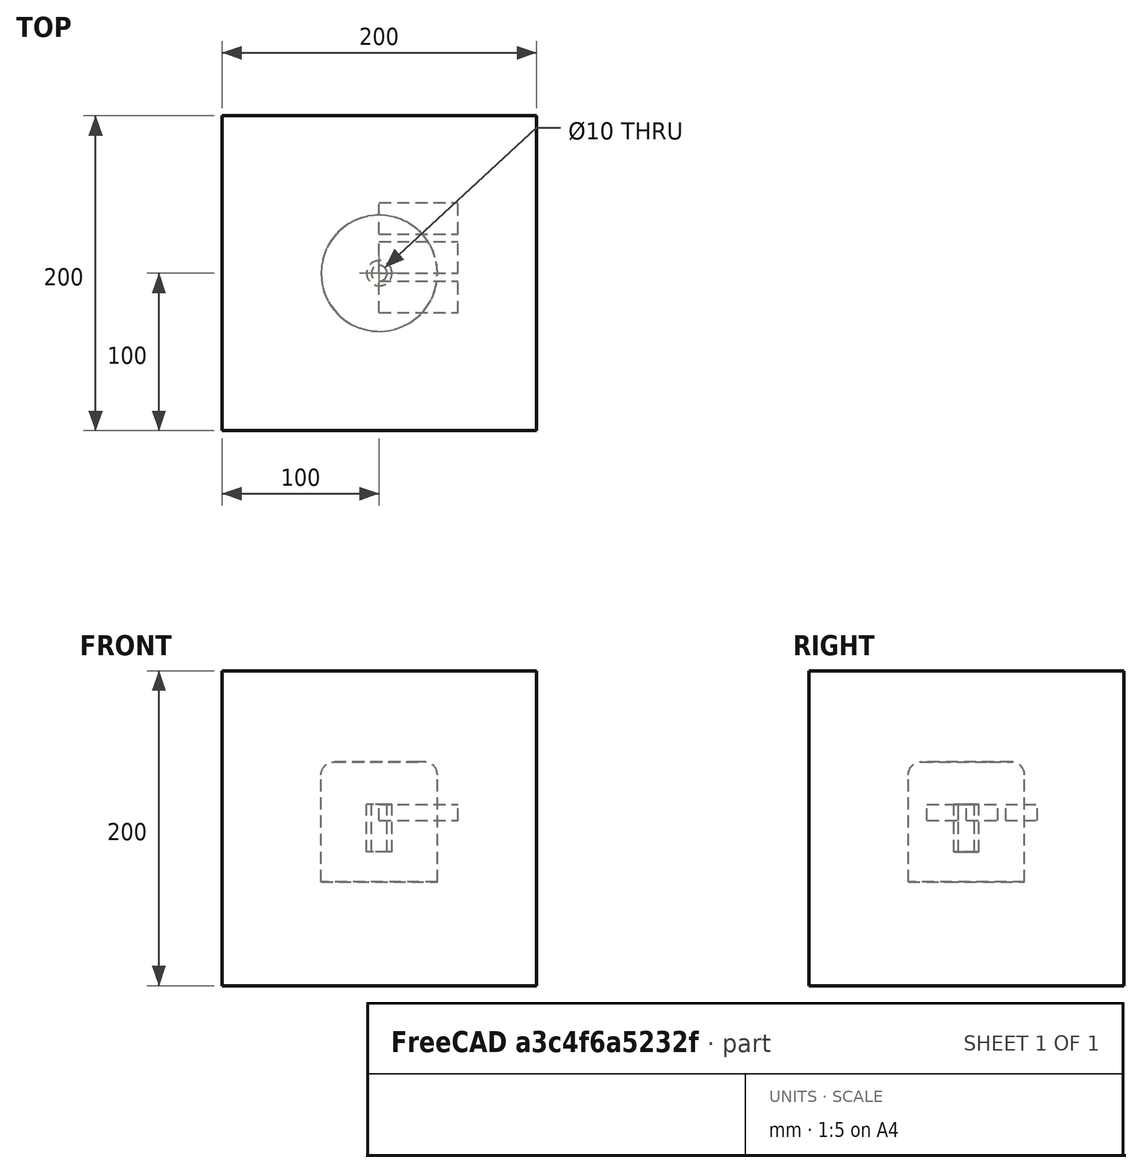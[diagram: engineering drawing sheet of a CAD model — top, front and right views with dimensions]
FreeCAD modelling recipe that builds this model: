
FCSTD DOCUMENT  (FreeCAD 0.21R33694 (Git))
Label: assemblyTest-A
License: All rights reserved
LicenseURL: http://en.wikipedia.org/wiki/All_rights_reserved
objects: App::DocumentObjectGroupPython×1254, Part::FeaturePython×5, App::Part×5, Part::Box×3, Part::Fuse×2
note: 10 computed .brp shape members not serialized (recipe doc carries the construction recipe); baked Part::Feature solids carry a one-line shape summary decoded from their .brp

FEATURE [App::DocumentObjectGroupPython] HALFPI  # scripted group (container) (typed FeaturePython)
  name = HALFPI
  value = pi/2.
FEATURE [App::DocumentObjectGroupPython] PI  # scripted group (container) (typed FeaturePython)
  name = PI
  value = 1.*pi
FEATURE [App::DocumentObjectGroupPython] TWOPI  # scripted group (container) (typed FeaturePython)
  name = TWOPI
  value = 2.*pi
FEATURE [App::DocumentObjectGroupPython] Variables  # scripted group (container) (typed FeaturePython)
FEATURE [App::DocumentObjectGroupPython] Quantities  # scripted group (container) (typed FeaturePython)
FEATURE [App::DocumentObjectGroupPython] Isotopes  # scripted group (container) (typed FeaturePython)
FEATURE [App::DocumentObjectGroupPython] Elements  # scripted group (container) (typed FeaturePython)
FEATURE [App::DocumentObjectGroupPython] G4Isotopes  # scripted group (container) (typed FeaturePython)
FEATURE [App::DocumentObjectGroupPython] H_element  # scripted group (container) (typed FeaturePython)
  Z = 1
  atom_value = 1.008
  formula = H
  name = H_element
FEATURE [App::DocumentObjectGroupPython] He_element  # scripted group (container) (typed FeaturePython)
  Z = 2
  atom_value = 4.0026
  formula = He
  name = He_element
FEATURE [App::DocumentObjectGroupPython] Li_element  # scripted group (container) (typed FeaturePython)
  Z = 3
  atom_value = 6.94
  formula = Li
  name = Li_element
FEATURE [App::DocumentObjectGroupPython] Be_element  # scripted group (container) (typed FeaturePython)
  Z = 4
  atom_value = 9.01218
  formula = Be
  name = Be_element
FEATURE [App::DocumentObjectGroupPython] B_element  # scripted group (container) (typed FeaturePython)
  Z = 5
  atom_value = 10.81
  formula = B
  name = B_element
FEATURE [App::DocumentObjectGroupPython] C_element  # scripted group (container) (typed FeaturePython)
  Z = 6
  atom_value = 12.011
  formula = C
  name = C_element
FEATURE [App::DocumentObjectGroupPython] N_element  # scripted group (container) (typed FeaturePython)
  Z = 7
  atom_value = 14.007
  formula = N
  name = N_element
FEATURE [App::DocumentObjectGroupPython] O_element  # scripted group (container) (typed FeaturePython)
  Z = 8
  atom_value = 15.999
  formula = O
  name = O_element
FEATURE [App::DocumentObjectGroupPython] F_element  # scripted group (container) (typed FeaturePython)
  Z = 9
  atom_value = 18.9984
  formula = F
  name = F_element
FEATURE [App::DocumentObjectGroupPython] Ne_element  # scripted group (container) (typed FeaturePython)
  Z = 10
  atom_value = 20.1797
  formula = Ne
  name = Ne_element
FEATURE [App::DocumentObjectGroupPython] Na_element  # scripted group (container) (typed FeaturePython)
  Z = 11
  atom_value = 22.9898
  formula = Na
  name = Na_element
FEATURE [App::DocumentObjectGroupPython] Mg_element  # scripted group (container) (typed FeaturePython)
  Z = 12
  atom_value = 24.305
  formula = Mg
  name = Mg_element
FEATURE [App::DocumentObjectGroupPython] Al_element  # scripted group (container) (typed FeaturePython)
  Z = 13
  atom_value = 26.9815
  formula = Al
  name = Al_element
FEATURE [App::DocumentObjectGroupPython] Si_element  # scripted group (container) (typed FeaturePython)
  Z = 14
  atom_value = 28.085
  formula = Si
  name = Si_element
FEATURE [App::DocumentObjectGroupPython] P_element  # scripted group (container) (typed FeaturePython)
  Z = 15
  atom_value = 30.9738
  formula = P
  name = P_element
FEATURE [App::DocumentObjectGroupPython] S_element  # scripted group (container) (typed FeaturePython)
  Z = 16
  atom_value = 32.06
  formula = S
  name = S_element
FEATURE [App::DocumentObjectGroupPython] Cl_element  # scripted group (container) (typed FeaturePython)
  Z = 17
  atom_value = 35.45
  formula = Cl
  name = Cl_element
FEATURE [App::DocumentObjectGroupPython] Ar_element  # scripted group (container) (typed FeaturePython)
  Z = 18
  atom_value = 39.95
  formula = Ar
  name = Ar_element
FEATURE [App::DocumentObjectGroupPython] K_element  # scripted group (container) (typed FeaturePython)
  Z = 19
  atom_value = 39.0983
  formula = K
  name = K_element
FEATURE [App::DocumentObjectGroupPython] Ca_element  # scripted group (container) (typed FeaturePython)
  Z = 20
  atom_value = 40.078
  formula = Ca
  name = Ca_element
FEATURE [App::DocumentObjectGroupPython] Sc_element  # scripted group (container) (typed FeaturePython)
  Z = 21
  atom_value = 44.9559
  formula = Sc
  name = Sc_element
FEATURE [App::DocumentObjectGroupPython] Ti_element  # scripted group (container) (typed FeaturePython)
  Z = 22
  atom_value = 47.867
  formula = Ti
  name = Ti_element
FEATURE [App::DocumentObjectGroupPython] V_element  # scripted group (container) (typed FeaturePython)
  Z = 23
  atom_value = 50.9415
  formula = V
  name = V_element
FEATURE [App::DocumentObjectGroupPython] Cr_element  # scripted group (container) (typed FeaturePython)
  Z = 24
  atom_value = 51.9961
  formula = Cr
  name = Cr_element
FEATURE [App::DocumentObjectGroupPython] Mn_element  # scripted group (container) (typed FeaturePython)
  Z = 25
  atom_value = 54.938
  formula = Mn
  name = Mn_element
FEATURE [App::DocumentObjectGroupPython] Fe_element  # scripted group (container) (typed FeaturePython)
  Z = 26
  atom_value = 55.845
  formula = Fe
  name = Fe_element
FEATURE [App::DocumentObjectGroupPython] Co_element  # scripted group (container) (typed FeaturePython)
  Z = 27
  atom_value = 58.9332
  formula = Co
  name = Co_element
FEATURE [App::DocumentObjectGroupPython] Ni_element  # scripted group (container) (typed FeaturePython)
  Z = 28
  atom_value = 58.6934
  formula = Ni
  name = Ni_element
FEATURE [App::DocumentObjectGroupPython] Cu_element  # scripted group (container) (typed FeaturePython)
  Z = 29
  atom_value = 63.546
  formula = Cu
  name = Cu_element
FEATURE [App::DocumentObjectGroupPython] Zn_element  # scripted group (container) (typed FeaturePython)
  Z = 30
  atom_value = 65.38
  formula = Zn
  name = Zn_element
FEATURE [App::DocumentObjectGroupPython] Ga_element  # scripted group (container) (typed FeaturePython)
  Z = 31
  atom_value = 69.723
  formula = Ga
  name = Ga_element
FEATURE [App::DocumentObjectGroupPython] Ge_element  # scripted group (container) (typed FeaturePython)
  Z = 32
  atom_value = 72.63
  formula = Ge
  name = Ge_element
FEATURE [App::DocumentObjectGroupPython] As_element  # scripted group (container) (typed FeaturePython)
  Z = 33
  atom_value = 74.9216
  formula = As
  name = As_element
FEATURE [App::DocumentObjectGroupPython] Se_element  # scripted group (container) (typed FeaturePython)
  Z = 34
  atom_value = 78.971
  formula = Se
  name = Se_element
FEATURE [App::DocumentObjectGroupPython] Br_element  # scripted group (container) (typed FeaturePython)
  Z = 35
  atom_value = 79.904
  formula = Br
  name = Br_element
FEATURE [App::DocumentObjectGroupPython] Kr_element  # scripted group (container) (typed FeaturePython)
  Z = 36
  atom_value = 83.798
  formula = Kr
  name = Kr_element
FEATURE [App::DocumentObjectGroupPython] Rb_element  # scripted group (container) (typed FeaturePython)
  Z = 37
  atom_value = 85.4678
  formula = Rb
  name = Rb_element
FEATURE [App::DocumentObjectGroupPython] Sr_element  # scripted group (container) (typed FeaturePython)
  Z = 38
  atom_value = 87.62
  formula = Sr
  name = Sr_element
FEATURE [App::DocumentObjectGroupPython] Y_element  # scripted group (container) (typed FeaturePython)
  Z = 39
  atom_value = 88.9058
  formula = Y
  name = Y_element
FEATURE [App::DocumentObjectGroupPython] Zr_element  # scripted group (container) (typed FeaturePython)
  Z = 40
  atom_value = 91.224
  formula = Zr
  name = Zr_element
FEATURE [App::DocumentObjectGroupPython] Nb_element  # scripted group (container) (typed FeaturePython)
  Z = 41
  atom_value = 92.9064
  formula = Nb
  name = Nb_element
FEATURE [App::DocumentObjectGroupPython] Mo_element  # scripted group (container) (typed FeaturePython)
  Z = 42
  atom_value = 95.95
  formula = Mo
  name = Mo_element
FEATURE [App::DocumentObjectGroupPython] Tc_element  # scripted group (container) (typed FeaturePython)
  Z = 43
  atom_value = 97
  formula = Tc
  name = Tc_element
FEATURE [App::DocumentObjectGroupPython] Ru_element  # scripted group (container) (typed FeaturePython)
  Z = 44
  atom_value = 101.07
  formula = Ru
  name = Ru_element
FEATURE [App::DocumentObjectGroupPython] Rh_element  # scripted group (container) (typed FeaturePython)
  Z = 45
  atom_value = 102.905
  formula = Rh
  name = Rh_element
FEATURE [App::DocumentObjectGroupPython] Pd_element  # scripted group (container) (typed FeaturePython)
  Z = 46
  atom_value = 106.42
  formula = Pd
  name = Pd_element
FEATURE [App::DocumentObjectGroupPython] Ag_element  # scripted group (container) (typed FeaturePython)
  Z = 47
  atom_value = 107.868
  formula = Ag
  name = Ag_element
FEATURE [App::DocumentObjectGroupPython] Cd_element  # scripted group (container) (typed FeaturePython)
  Z = 48
  atom_value = 112.414
  formula = Cd
  name = Cd_element
FEATURE [App::DocumentObjectGroupPython] In_element  # scripted group (container) (typed FeaturePython)
  Z = 49
  atom_value = 114.818
  formula = In
  name = In_element
FEATURE [App::DocumentObjectGroupPython] Sn_element  # scripted group (container) (typed FeaturePython)
  Z = 50
  atom_value = 118.71
  formula = Sn
  name = Sn_element
FEATURE [App::DocumentObjectGroupPython] Sb_element  # scripted group (container) (typed FeaturePython)
  Z = 51
  atom_value = 121.76
  formula = Sb
  name = Sb_element
FEATURE [App::DocumentObjectGroupPython] Te_element  # scripted group (container) (typed FeaturePython)
  Z = 52
  atom_value = 127.6
  formula = Te
  name = Te_element
FEATURE [App::DocumentObjectGroupPython] I_element  # scripted group (container) (typed FeaturePython)
  Z = 53
  atom_value = 126.904
  formula = I
  name = I_element
FEATURE [App::DocumentObjectGroupPython] Xe_element  # scripted group (container) (typed FeaturePython)
  Z = 54
  atom_value = 131.293
  formula = Xe
  name = Xe_element
FEATURE [App::DocumentObjectGroupPython] Cs_element  # scripted group (container) (typed FeaturePython)
  Z = 55
  atom_value = 132.905
  formula = Cs
  name = Cs_element
FEATURE [App::DocumentObjectGroupPython] Ba_element  # scripted group (container) (typed FeaturePython)
  Z = 56
  atom_value = 137.327
  formula = Ba
  name = Ba_element
FEATURE [App::DocumentObjectGroupPython] La_element  # scripted group (container) (typed FeaturePython)
  Z = 57
  atom_value = 138.905
  formula = La
  name = La_element
FEATURE [App::DocumentObjectGroupPython] Ce_element  # scripted group (container) (typed FeaturePython)
  Z = 58
  atom_value = 140.116
  formula = Ce
  name = Ce_element
FEATURE [App::DocumentObjectGroupPython] Pr_element  # scripted group (container) (typed FeaturePython)
  Z = 59
  atom_value = 140.908
  formula = Pr
  name = Pr_element
FEATURE [App::DocumentObjectGroupPython] Nd_element  # scripted group (container) (typed FeaturePython)
  Z = 60
  atom_value = 144.242
  formula = Nd
  name = Nd_element
FEATURE [App::DocumentObjectGroupPython] Pm_element  # scripted group (container) (typed FeaturePython)
  Z = 61
  atom_value = 145
  formula = Pm
  name = Pm_element
FEATURE [App::DocumentObjectGroupPython] Sm_element  # scripted group (container) (typed FeaturePython)
  Z = 62
  atom_value = 150.36
  formula = Sm
  name = Sm_element
FEATURE [App::DocumentObjectGroupPython] Eu_element  # scripted group (container) (typed FeaturePython)
  Z = 63
  atom_value = 151.964
  formula = Eu
  name = Eu_element
FEATURE [App::DocumentObjectGroupPython] Gd_element  # scripted group (container) (typed FeaturePython)
  Z = 64
  atom_value = 157.25
  formula = Gd
  name = Gd_element
FEATURE [App::DocumentObjectGroupPython] Tb_element  # scripted group (container) (typed FeaturePython)
  Z = 65
  atom_value = 158.925
  formula = Tb
  name = Tb_element
FEATURE [App::DocumentObjectGroupPython] Dy_element  # scripted group (container) (typed FeaturePython)
  Z = 66
  atom_value = 162.5
  formula = Dy
  name = Dy_element
FEATURE [App::DocumentObjectGroupPython] Ho_element  # scripted group (container) (typed FeaturePython)
  Z = 67
  atom_value = 164.93
  formula = Ho
  name = Ho_element
FEATURE [App::DocumentObjectGroupPython] Er_element  # scripted group (container) (typed FeaturePython)
  Z = 68
  atom_value = 167.259
  formula = Er
  name = Er_element
FEATURE [App::DocumentObjectGroupPython] Tm_element  # scripted group (container) (typed FeaturePython)
  Z = 69
  atom_value = 168.934
  formula = Tm
  name = Tm_element
FEATURE [App::DocumentObjectGroupPython] Yb_element  # scripted group (container) (typed FeaturePython)
  Z = 70
  atom_value = 173.045
  formula = Yb
  name = Yb_element
FEATURE [App::DocumentObjectGroupPython] Lu_element  # scripted group (container) (typed FeaturePython)
  Z = 71
  atom_value = 174.967
  formula = Lu
  name = Lu_element
FEATURE [App::DocumentObjectGroupPython] Hf_element  # scripted group (container) (typed FeaturePython)
  Z = 72
  atom_value = 178.49
  formula = Hf
  name = Hf_element
FEATURE [App::DocumentObjectGroupPython] Ta_element  # scripted group (container) (typed FeaturePython)
  Z = 73
  atom_value = 180.948
  formula = Ta
  name = Ta_element
FEATURE [App::DocumentObjectGroupPython] W_element  # scripted group (container) (typed FeaturePython)
  Z = 74
  atom_value = 183.84
  formula = W
  name = W_element
FEATURE [App::DocumentObjectGroupPython] Re_element  # scripted group (container) (typed FeaturePython)
  Z = 75
  atom_value = 186.207
  formula = Re
  name = Re_element
FEATURE [App::DocumentObjectGroupPython] Os_element  # scripted group (container) (typed FeaturePython)
  Z = 76
  atom_value = 190.23
  formula = Os
  name = Os_element
FEATURE [App::DocumentObjectGroupPython] Ir_element  # scripted group (container) (typed FeaturePython)
  Z = 77
  atom_value = 192.217
  formula = Ir
  name = Ir_element
FEATURE [App::DocumentObjectGroupPython] Pt_element  # scripted group (container) (typed FeaturePython)
  Z = 78
  atom_value = 195.084
  formula = Pt
  name = Pt_element
FEATURE [App::DocumentObjectGroupPython] Au_element  # scripted group (container) (typed FeaturePython)
  Z = 79
  atom_value = 196.967
  formula = Au
  name = Au_element
FEATURE [App::DocumentObjectGroupPython] Hg_element  # scripted group (container) (typed FeaturePython)
  Z = 80
  atom_value = 200.592
  formula = Hg
  name = Hg_element
FEATURE [App::DocumentObjectGroupPython] Tl_element  # scripted group (container) (typed FeaturePython)
  Z = 81
  atom_value = 204.38
  formula = Tl
  name = Tl_element
FEATURE [App::DocumentObjectGroupPython] Pb_element  # scripted group (container) (typed FeaturePython)
  Z = 82
  atom_value = 207.2
  formula = Pb
  name = Pb_element
FEATURE [App::DocumentObjectGroupPython] Bi_element  # scripted group (container) (typed FeaturePython)
  Z = 83
  atom_value = 208.98
  formula = Bi
  name = Bi_element
FEATURE [App::DocumentObjectGroupPython] Po_element  # scripted group (container) (typed FeaturePython)
  Z = 84
  atom_value = 209
  formula = Po
  name = Po_element
FEATURE [App::DocumentObjectGroupPython] At_element  # scripted group (container) (typed FeaturePython)
  Z = 85
  atom_value = 210
  formula = At
  name = At_element
FEATURE [App::DocumentObjectGroupPython] Rn_element  # scripted group (container) (typed FeaturePython)
  Z = 86
  atom_value = 222
  formula = Rn
  name = Rn_element
FEATURE [App::DocumentObjectGroupPython] Fr_element  # scripted group (container) (typed FeaturePython)
  Z = 87
  atom_value = 223
  formula = Fr
  name = Fr_element
FEATURE [App::DocumentObjectGroupPython] Ra_element  # scripted group (container) (typed FeaturePython)
  Z = 88
  atom_value = 226
  formula = Ra
  name = Ra_element
FEATURE [App::DocumentObjectGroupPython] Ac_element  # scripted group (container) (typed FeaturePython)
  Z = 89
  atom_value = 227
  formula = Ac
  name = Ac_element
FEATURE [App::DocumentObjectGroupPython] Th_element  # scripted group (container) (typed FeaturePython)
  Z = 90
  atom_value = 232.038
  formula = Th
  name = Th_element
FEATURE [App::DocumentObjectGroupPython] Pa_element  # scripted group (container) (typed FeaturePython)
  Z = 91
  atom_value = 231.036
  formula = Pa
  name = Pa_element
FEATURE [App::DocumentObjectGroupPython] U_element  # scripted group (container) (typed FeaturePython)
  Z = 92
  atom_value = 238.029
  formula = U
  name = U_element
FEATURE [App::DocumentObjectGroupPython] Np_element  # scripted group (container) (typed FeaturePython)
  Z = 93
  atom_value = 237
  formula = Np
  name = Np_element
FEATURE [App::DocumentObjectGroupPython] Pu_element  # scripted group (container) (typed FeaturePython)
  Z = 94
  atom_value = 244
  formula = Pu
  name = Pu_element
FEATURE [App::DocumentObjectGroupPython] Am_element  # scripted group (container) (typed FeaturePython)
  Z = 95
  atom_value = 243
  formula = Am
  name = Am_element
FEATURE [App::DocumentObjectGroupPython] Cm_element  # scripted group (container) (typed FeaturePython)
  Z = 96
  atom_value = 247
  formula = Cm
  name = Cm_element
FEATURE [App::DocumentObjectGroupPython] Bk_element  # scripted group (container) (typed FeaturePython)
  Z = 97
  atom_value = 247
  formula = Bk
  name = Bk_element
FEATURE [App::DocumentObjectGroupPython] Cf_element  # scripted group (container) (typed FeaturePython)
  Z = 98
  atom_value = 251
  formula = Cf
  name = Cf_element
FEATURE [App::DocumentObjectGroupPython] G4Elements  # scripted group (container) (typed FeaturePython)
  Group = -> [H_element,He_element,Li_element,Be_element,B_element,C_element,N_element,O_element,F_element,Ne_element,Na_element,Mg_element,Al_element,Si_element,P_element,S_element,Cl_element,Ar_element,K_element,Ca_element,Sc_element,Ti_element,V_element,Cr_element,Mn_element,Fe_element,Co_element,Ni_element,Cu_element,Zn_element,Ga_element,Ge_element,As_element,Se_element,Br_element,Kr_element,Rb_element,+61 more]
FEATURE [Part::FeaturePython] GDMLBox_WorldBox  # WARN: FeaturePython — macro-defined, semantics opaque (R4)
  lunit = 2
  material = 5
  x = 200
  y = 200
  z = 200
FEATURE [App::DocumentObjectGroupPython] HALFPI001  # scripted group (container) (typed FeaturePython)
  name = HALFPI
  value = pi/2.
FEATURE [App::DocumentObjectGroupPython] PI001  # scripted group (container) (typed FeaturePython)
  name = PI
  value = 1.*pi
FEATURE [App::DocumentObjectGroupPython] TWOPI001  # scripted group (container) (typed FeaturePython)
  name = TWOPI
  value = 2.*pi
FEATURE [App::DocumentObjectGroupPython] HALFPI001001  # scripted group (container) (typed FeaturePython)
  name = HALFPI001
  value = pi/2.
FEATURE [App::DocumentObjectGroupPython] PI001001  # scripted group (container) (typed FeaturePython)
  name = PI001
  value = 1.*pi
FEATURE [App::DocumentObjectGroupPython] TWOPI001001  # scripted group (container) (typed FeaturePython)
  name = TWOPI001
  value = 2.*pi
FEATURE [App::DocumentObjectGroupPython] Constants  # scripted group (container) (typed FeaturePython)
  Group = -> [HALFPI,PI,TWOPI,HALFPI001,PI001,TWOPI001,HALFPI001001,PI001001,TWOPI001001]
FEATURE [Part::FeaturePython] GDMLTorus_Torus  # WARN: FeaturePython — macro-defined, semantics opaque (R4)
  aunit = deg
  deltaphi = 360
  lunit = 2
  material = 0
  rmax = 8
  rmin = 0
  rtor = 28.9
  startphi = 0
FEATURE [Part::FeaturePython] GDMLTube_Tube  # WARN: FeaturePython — macro-defined, semantics opaque (R4)
  aunit = 1
  deltaphi = 360
  lunit = 2
  material = 0
  rmax = 28.9
  rmin = 0
  startphi = 0
  z = 16
FEATURE [Part::FeaturePython] GDMLTube_Tube001  label="GDMLTube_T_1"  # WARN: FeaturePython — macro-defined, semantics opaque (R4)
  Placement = pos=(0,0,-34) rot=(0,0,-1;0.349066rad)
  aunit = 1
  deltaphi = 360
  lunit = 2
  material = 0
  rmax = 36.9
  rmin = 0
  startphi = 0
  z = 68
FEATURE [Part::Fuse] Union
  Base = -> GDMLTorus_Torus
  Placement = pos=(0,0,0) rot=(0,0,1;0.523599rad)
  Tool = -> GDMLTube_Tube
FEATURE [Part::Fuse] Union001  label="U1"
  Base = -> Union
  Placement = pos=(0,0,34) rot=(0,0,1;0rad)
  Tool = -> GDMLTube_Tube001
  material = 211
FEATURE [App::Part] Bool_Union001  label="Detector"
  Group = -> [GDMLTorus_Torus,GDMLTube_Tube,Union,GDMLTube_Tube001,Union001]
  Origin = -> Origin005
FEATURE [Part::FeaturePython] GDMLTube_Tube002  # WARN: FeaturePython — macro-defined, semantics opaque (R4)
  aunit = 1
  deltaphi = 360
  lunit = 2
  material = 109
  rmax = 8
  rmin = 5
  startphi = 0
  z = 30
FEATURE [App::Part] LV_Tube  label="Tube"
  Group = -> [GDMLTube_Tube002]
  Origin = -> Origin006
  Placement = pos=(57,0,0) rot=(0,1,0;1.5708rad)
FEATURE [App::Part] Part  label="DetectorAssembly"
  Group = -> [Bool_Union001,LV_Tube]
  Origin = -> Origin007
FEATURE [Part::Box] Box  label="Cube"
  AttacherType = Attacher::AttachEngine3D
  Height = 10
  Length = 50
  Placement = pos=(0,0,5) rot=(0,0,1;0rad)
  Width = 20
  material = 441
FEATURE [Part::Box] Box001  label="Cube001"
  AttacherType = Attacher::AttachEngine3D
  Height = 10
  Length = 50
  Placement = pos=(0,25,5) rot=(0,0,1;0rad)
  Width = 20
  material = 441
FEATURE [Part::Box] Box002  label="Cube002"
  AttacherType = Attacher::AttachEngine3D
  Height = 10
  Length = 50
  Placement = pos=(0,-25,5) rot=(0,0,1;0rad)
  Width = 20
  material = 261
FEATURE [App::Part] Part001  label="shieldAssembly"
  Group = -> [Box,Box001,Box002]
  Origin = -> Origin008
  Placement = pos=(0,0,58) rot=(0,0,1;0rad)
FEATURE [App::Part] worldVOL
  Group = -> [GDMLBox_WorldBox,Part,Part001]
  Origin = -> Origin
FEATURE [App::DocumentObjectGroupPython] H_element553  label="H_element : 0.246"  # scripted group (container) (typed FeaturePython)
  n = 0.101327
FEATURE [App::DocumentObjectGroupPython] C_element593  label="C_element : 0.974"  # scripted group (container) (typed FeaturePython)
  n = 0.7755
FEATURE [App::DocumentObjectGroupPython] N_element273  label="N_element : 0.828"  # scripted group (container) (typed FeaturePython)
  n = 0.035057
FEATURE [App::DocumentObjectGroupPython] O_element521  label="O_element : 0.966"  # scripted group (container) (typed FeaturePython)
  n = 0.0523159
FEATURE [App::DocumentObjectGroupPython] F_element077  label="F_element : 0.727"  # scripted group (container) (typed FeaturePython)
  n = 0.017422
FEATURE [App::DocumentObjectGroupPython] Ca_element057  label="Ca_element : 0.240"  # scripted group (container) (typed FeaturePython)
  n = 0.018378
FEATURE [App::DocumentObjectGroupPython] G4_A_150_TISSUE  label="G4_A-150_TISSUE"  # scripted group (container) (typed FeaturePython)
  Dunit = g/cm3
  Dvalue = 1.127
  Group = -> [H_element553,C_element593,N_element273,O_element521,F_element077,Ca_element057]
  conduct = 2
  density = 1
  expand = 3
  formula = G4_A-150_TISSUE
  name = G4_A-150_TISSUE
  specific = 4
FEATURE [App::DocumentObjectGroupPython] C_element594  label="C_element : 390"  # scripted group (container) (typed FeaturePython)
  n = 3
  ref = C_element
FEATURE [App::DocumentObjectGroupPython] H_element554  label="H_element : 358"  # scripted group (container) (typed FeaturePython)
  n = 6
  ref = H_element
FEATURE [App::DocumentObjectGroupPython] O_element522  label="O_element : 335"  # scripted group (container) (typed FeaturePython)
  n = 1
  ref = O_element
FEATURE [App::DocumentObjectGroupPython] G4_ACETONE  # scripted group (container) (typed FeaturePython)
  Dunit = g/cm3
  Dvalue = 0.7899
  Group = -> [C_element594,H_element554,O_element522]
  conduct = 2
  density = 1
  expand = 3
  formula = G4_ACETONE
  name = G4_ACETONE
  specific = 4
FEATURE [App::DocumentObjectGroupPython] C_element595  label="C_element : 391"  # scripted group (container) (typed FeaturePython)
  n = 2
  ref = C_element
FEATURE [App::DocumentObjectGroupPython] H_element555  label="H_element : 359"  # scripted group (container) (typed FeaturePython)
  n = 2
  ref = H_element
FEATURE [App::DocumentObjectGroupPython] G4_ACETYLENE  # scripted group (container) (typed FeaturePython)
  Dunit = g/cm3
  Dvalue = 0.0010967
  Group = -> [C_element595,H_element555]
  conduct = 2
  density = 1
  expand = 3
  formula = G4_ACETYLENE
  name = G4_ACETYLENE
  specific = 4
FEATURE [App::DocumentObjectGroupPython] C_element596  label="C_element : 392"  # scripted group (container) (typed FeaturePython)
  n = 5
  ref = C_element
FEATURE [App::DocumentObjectGroupPython] H_element556  label="H_element : 360"  # scripted group (container) (typed FeaturePython)
  n = 5
  ref = H_element
FEATURE [App::DocumentObjectGroupPython] N_element274  label="N_element : 154"  # scripted group (container) (typed FeaturePython)
  n = 5
  ref = N_element
FEATURE [App::DocumentObjectGroupPython] G4_ADENINE  # scripted group (container) (typed FeaturePython)
  Dunit = g/cm3
  Dvalue = 1.6
  Group = -> [C_element596,H_element556,N_element274]
  conduct = 2
  density = 1
  expand = 3
  formula = G4_ADENINE
  name = G4_ADENINE
  specific = 4
FEATURE [App::DocumentObjectGroupPython] H_element557  label="H_element : 0.247"  # scripted group (container) (typed FeaturePython)
  n = 0.114
FEATURE [App::DocumentObjectGroupPython] C_element597  label="C_element : 0.975"  # scripted group (container) (typed FeaturePython)
  n = 0.598
FEATURE [App::DocumentObjectGroupPython] N_element275  label="N_element : 0.829"  # scripted group (container) (typed FeaturePython)
  n = 0.007
FEATURE [App::DocumentObjectGroupPython] O_element523  label="O_element : 0.967"  # scripted group (container) (typed FeaturePython)
  n = 0.278
FEATURE [App::DocumentObjectGroupPython] Na_element081  label="Na_element : 0.142"  # scripted group (container) (typed FeaturePython)
  n = 0.001
FEATURE [App::DocumentObjectGroupPython] S_element093  label="S_element : 0.065"  # scripted group (container) (typed FeaturePython)
  n = 0.001
FEATURE [App::DocumentObjectGroupPython] Cl_element121  label="Cl_element : 0.627"  # scripted group (container) (typed FeaturePython)
  n = 0.001
FEATURE [App::DocumentObjectGroupPython] G4_ADIPOSE_TISSUE_ICRP  # scripted group (container) (typed FeaturePython)
  Dunit = g/cm3
  Dvalue = 0.95
  Group = -> [H_element557,C_element597,N_element275,O_element523,Na_element081,S_element093,Cl_element121]
  conduct = 2
  density = 1
  expand = 3
  formula = G4_ADIPOSE_TISSUE_ICRP
  name = G4_ADIPOSE_TISSUE_ICRP
  specific = 4
FEATURE [App::DocumentObjectGroupPython] C_element598  label="C_element : 0.976"  # scripted group (container) (typed FeaturePython)
  n = 0.000124
FEATURE [App::DocumentObjectGroupPython] N_element276  label="N_element : 0.830"  # scripted group (container) (typed FeaturePython)
  n = 0.755268
FEATURE [App::DocumentObjectGroupPython] O_element524  label="O_element : 0.968"  # scripted group (container) (typed FeaturePython)
  n = 0.231781
FEATURE [App::DocumentObjectGroupPython] Ar_element009  label="Ar_element : 0.016"  # scripted group (container) (typed FeaturePython)
  n = 0.012827
FEATURE [App::DocumentObjectGroupPython] G4_AIR  # scripted group (container) (typed FeaturePython)
  Dunit = g/cm3
  Dvalue = 0.00120479
  Group = -> [C_element598,N_element276,O_element524,Ar_element009]
  conduct = 2
  density = 1
  expand = 3
  formula = G4_AIR
  name = G4_AIR
  specific = 4
FEATURE [App::DocumentObjectGroupPython] C_element599  label="C_element : 393"  # scripted group (container) (typed FeaturePython)
  n = 3
  ref = C_element
FEATURE [App::DocumentObjectGroupPython] H_element558  label="H_element : 361"  # scripted group (container) (typed FeaturePython)
  n = 7
  ref = H_element
FEATURE [App::DocumentObjectGroupPython] N_element277  label="N_element : 155"  # scripted group (container) (typed FeaturePython)
  n = 1
  ref = N_element
FEATURE [App::DocumentObjectGroupPython] O_element525  label="O_element : 336"  # scripted group (container) (typed FeaturePython)
  n = 2
  ref = O_element
FEATURE [App::DocumentObjectGroupPython] G4_ALANINE  # scripted group (container) (typed FeaturePython)
  Dunit = g/cm3
  Dvalue = 1.42
  Group = -> [C_element599,H_element558,N_element277,O_element525]
  conduct = 2
  density = 1
  expand = 3
  formula = G4_ALANINE
  name = G4_ALANINE
  specific = 4
FEATURE [App::DocumentObjectGroupPython] Al_element017  label="Al_element : 007"  # scripted group (container) (typed FeaturePython)
  n = 2
  ref = Al_element
FEATURE [App::DocumentObjectGroupPython] O_element526  label="O_element : 337"  # scripted group (container) (typed FeaturePython)
  n = 3
  ref = O_element
FEATURE [App::DocumentObjectGroupPython] G4_ALUMINUM_OXIDE  # scripted group (container) (typed FeaturePython)
  Dunit = g/cm3
  Dvalue = 3.97
  Group = -> [Al_element017,O_element526]
  conduct = 2
  density = 1
  expand = 3
  formula = G4_ALUMINUM_OXIDE
  name = G4_ALUMINUM_OXIDE
  specific = 4
FEATURE [App::DocumentObjectGroupPython] H_element559  label="H_element : 0.248"  # scripted group (container) (typed FeaturePython)
  n = 0.10593
FEATURE [App::DocumentObjectGroupPython] C_element600  label="C_element : 0.977"  # scripted group (container) (typed FeaturePython)
  n = 0.788974
FEATURE [App::DocumentObjectGroupPython] O_element527  label="O_element : 0.969"  # scripted group (container) (typed FeaturePython)
  n = 0.105096
FEATURE [App::DocumentObjectGroupPython] G4_AMBER  # scripted group (container) (typed FeaturePython)
  Dunit = g/cm3
  Dvalue = 1.1
  Group = -> [H_element559,C_element600,O_element527]
  conduct = 2
  density = 1
  expand = 3
  formula = G4_AMBER
  name = G4_AMBER
  specific = 4
FEATURE [App::DocumentObjectGroupPython] N_element278  label="N_element : 156"  # scripted group (container) (typed FeaturePython)
  n = 1
  ref = N_element
FEATURE [App::DocumentObjectGroupPython] H_element560  label="H_element : 362"  # scripted group (container) (typed FeaturePython)
  n = 3
  ref = H_element
FEATURE [App::DocumentObjectGroupPython] G4_AMMONIA  # scripted group (container) (typed FeaturePython)
  Dunit = g/cm3
  Dvalue = 0.000826019
  Group = -> [N_element278,H_element560]
  conduct = 2
  density = 1
  expand = 3
  formula = G4_AMMONIA
  name = G4_AMMONIA
  specific = 4
FEATURE [App::DocumentObjectGroupPython] C_element601  label="C_element : 394"  # scripted group (container) (typed FeaturePython)
  n = 6
  ref = C_element
FEATURE [App::DocumentObjectGroupPython] H_element561  label="H_element : 363"  # scripted group (container) (typed FeaturePython)
  n = 7
  ref = H_element
FEATURE [App::DocumentObjectGroupPython] N_element279  label="N_element : 157"  # scripted group (container) (typed FeaturePython)
  n = 1
  ref = N_element
FEATURE [App::DocumentObjectGroupPython] G4_ANILINE  # scripted group (container) (typed FeaturePython)
  Dunit = g/cm3
  Dvalue = 1.0235
  Group = -> [C_element601,H_element561,N_element279]
  conduct = 2
  density = 1
  expand = 3
  formula = G4_ANILINE
  name = G4_ANILINE
  specific = 4
FEATURE [App::DocumentObjectGroupPython] C_element602  label="C_element : 395"  # scripted group (container) (typed FeaturePython)
  n = 14
  ref = C_element
FEATURE [App::DocumentObjectGroupPython] H_element562  label="H_element : 364"  # scripted group (container) (typed FeaturePython)
  n = 10
  ref = H_element
FEATURE [App::DocumentObjectGroupPython] G4_ANTHRACENE  # scripted group (container) (typed FeaturePython)
  Dunit = g/cm3
  Dvalue = 1.283
  Group = -> [C_element602,H_element562]
  conduct = 2
  density = 1
  expand = 3
  formula = G4_ANTHRACENE
  name = G4_ANTHRACENE
  specific = 4
FEATURE [App::DocumentObjectGroupPython] H_element563  label="H_element : 0.249"  # scripted group (container) (typed FeaturePython)
  n = 0.0654709
FEATURE [App::DocumentObjectGroupPython] C_element603  label="C_element : 0.978"  # scripted group (container) (typed FeaturePython)
  n = 0.536944
FEATURE [App::DocumentObjectGroupPython] N_element280  label="N_element : 0.831"  # scripted group (container) (typed FeaturePython)
  n = 0.0215
FEATURE [App::DocumentObjectGroupPython] O_element528  label="O_element : 0.970"  # scripted group (container) (typed FeaturePython)
  n = 0.032085
FEATURE [App::DocumentObjectGroupPython] F_element078  label="F_element : 0.728"  # scripted group (container) (typed FeaturePython)
  n = 0.167411
FEATURE [App::DocumentObjectGroupPython] Ca_element058  label="Ca_element : 0.241"  # scripted group (container) (typed FeaturePython)
  n = 0.176589
FEATURE [App::DocumentObjectGroupPython] G4_B_100_BONE  label="G4_B-100_BONE"  # scripted group (container) (typed FeaturePython)
  Dunit = g/cm3
  Dvalue = 1.45
  Group = -> [H_element563,C_element603,N_element280,O_element528,F_element078,Ca_element058]
  conduct = 2
  density = 1
  expand = 3
  formula = G4_B-100_BONE
  name = G4_B-100_BONE
  specific = 4
FEATURE [App::DocumentObjectGroupPython] H_element564  label="H_element : 0.250"  # scripted group (container) (typed FeaturePython)
  n = 0.057441
FEATURE [App::DocumentObjectGroupPython] C_element604  label="C_element : 0.979"  # scripted group (container) (typed FeaturePython)
  n = 0.774591
FEATURE [App::DocumentObjectGroupPython] O_element529  label="O_element : 0.971"  # scripted group (container) (typed FeaturePython)
  n = 0.167968
FEATURE [App::DocumentObjectGroupPython] G4_BAKELITE  # scripted group (container) (typed FeaturePython)
  Dunit = g/cm3
  Dvalue = 1.25
  Group = -> [H_element564,C_element604,O_element529]
  conduct = 2
  density = 1
  expand = 3
  formula = G4_BAKELITE
  name = G4_BAKELITE
  specific = 4
FEATURE [App::DocumentObjectGroupPython] Ba_element013  label="Ba_element : 012"  # scripted group (container) (typed FeaturePython)
  n = 1
  ref = Ba_element
FEATURE [App::DocumentObjectGroupPython] F_element079  label="F_element : 037"  # scripted group (container) (typed FeaturePython)
  n = 2
  ref = F_element
FEATURE [App::DocumentObjectGroupPython] G4_BARIUM_FLUORIDE  # scripted group (container) (typed FeaturePython)
  Dunit = g/cm3
  Dvalue = 4.89
  Group = -> [Ba_element013,F_element079]
  conduct = 2
  density = 1
  expand = 3
  formula = G4_BARIUM_FLUORIDE
  name = G4_BARIUM_FLUORIDE
  specific = 4
FEATURE [App::DocumentObjectGroupPython] Ba_element014  label="Ba_element : 013"  # scripted group (container) (typed FeaturePython)
  n = 1
  ref = Ba_element
FEATURE [App::DocumentObjectGroupPython] S_element094  label="S_element : 028"  # scripted group (container) (typed FeaturePython)
  n = 1
  ref = S_element
FEATURE [App::DocumentObjectGroupPython] O_element530  label="O_element : 338"  # scripted group (container) (typed FeaturePython)
  n = 4
  ref = O_element
FEATURE [App::DocumentObjectGroupPython] G4_BARIUM_SULFATE  # scripted group (container) (typed FeaturePython)
  Dunit = g/cm3
  Dvalue = 4.5
  Group = -> [Ba_element014,S_element094,O_element530]
  conduct = 2
  density = 1
  expand = 3
  formula = G4_BARIUM_SULFATE
  name = G4_BARIUM_SULFATE
  specific = 4
FEATURE [App::DocumentObjectGroupPython] C_element605  label="C_element : 396"  # scripted group (container) (typed FeaturePython)
  n = 6
  ref = C_element
FEATURE [App::DocumentObjectGroupPython] H_element565  label="H_element : 365"  # scripted group (container) (typed FeaturePython)
  n = 6
  ref = H_element
FEATURE [App::DocumentObjectGroupPython] G4_BENZENE  # scripted group (container) (typed FeaturePython)
  Dunit = g/cm3
  Dvalue = 0.87865
  Group = -> [C_element605,H_element565]
  conduct = 2
  density = 1
  expand = 3
  formula = G4_BENZENE
  name = G4_BENZENE
  specific = 4
FEATURE [App::DocumentObjectGroupPython] Be_element009  label="Be_element : 008"  # scripted group (container) (typed FeaturePython)
  n = 1
  ref = Be_element
FEATURE [App::DocumentObjectGroupPython] O_element531  label="O_element : 339"  # scripted group (container) (typed FeaturePython)
  n = 1
  ref = O_element
FEATURE [App::DocumentObjectGroupPython] G4_BERYLLIUM_OXIDE  # scripted group (container) (typed FeaturePython)
  Dunit = g/cm3
  Dvalue = 3.01
  Group = -> [Be_element009,O_element531]
  conduct = 2
  density = 1
  expand = 3
  formula = G4_BERYLLIUM_OXIDE
  name = G4_BERYLLIUM_OXIDE
  specific = 4
FEATURE [App::DocumentObjectGroupPython] Bi_element009  label="Bi_element : 009"  # scripted group (container) (typed FeaturePython)
  n = 4
  ref = Bi_element
FEATURE [App::DocumentObjectGroupPython] Ge_element009  label="Ge_element : 008"  # scripted group (container) (typed FeaturePython)
  n = 3
  ref = Ge_element
FEATURE [App::DocumentObjectGroupPython] O_element532  label="O_element : 340"  # scripted group (container) (typed FeaturePython)
  n = 12
  ref = O_element
FEATURE [App::DocumentObjectGroupPython] G4_BGO  # scripted group (container) (typed FeaturePython)
  Dunit = g/cm3
  Dvalue = 7.13
  Group = -> [Bi_element009,Ge_element009,O_element532]
  conduct = 2
  density = 1
  expand = 3
  formula = G4_BGO
  name = G4_BGO
  specific = 4
FEATURE [App::DocumentObjectGroupPython] H_element566  label="H_element : 0.251"  # scripted group (container) (typed FeaturePython)
  n = 0.102
FEATURE [App::DocumentObjectGroupPython] C_element606  label="C_element : 0.980"  # scripted group (container) (typed FeaturePython)
  n = 0.11
FEATURE [App::DocumentObjectGroupPython] N_element281  label="N_element : 0.832"  # scripted group (container) (typed FeaturePython)
  n = 0.033
FEATURE [App::DocumentObjectGroupPython] O_element533  label="O_element : 0.972"  # scripted group (container) (typed FeaturePython)
  n = 0.745
FEATURE [App::DocumentObjectGroupPython] Na_element082  label="Na_element : 0.143"  # scripted group (container) (typed FeaturePython)
  n = 0.001
FEATURE [App::DocumentObjectGroupPython] P_element077  label="P_element : 0.138"  # scripted group (container) (typed FeaturePython)
  n = 0.001
FEATURE [App::DocumentObjectGroupPython] S_element095  label="S_element : 0.066"  # scripted group (container) (typed FeaturePython)
  n = 0.002
FEATURE [App::DocumentObjectGroupPython] Cl_element122  label="Cl_element : 0.628"  # scripted group (container) (typed FeaturePython)
  n = 0.003
FEATURE [App::DocumentObjectGroupPython] K_element053  label="K_element : 0.044"  # scripted group (container) (typed FeaturePython)
  n = 0.002
FEATURE [App::DocumentObjectGroupPython] Fe_element033  label="Fe_element : 0.021"  # scripted group (container) (typed FeaturePython)
  n = 0.001
FEATURE [App::DocumentObjectGroupPython] G4_BLOOD_ICRP  # scripted group (container) (typed FeaturePython)
  Dunit = g/cm3
  Dvalue = 1.06
  Group = -> [H_element566,C_element606,N_element281,O_element533,Na_element082,P_element077,S_element095,Cl_element122,K_element053,Fe_element033]
  conduct = 2
  density = 1
  expand = 3
  formula = G4_BLOOD_ICRP
  name = G4_BLOOD_ICRP
  specific = 4
FEATURE [App::DocumentObjectGroupPython] H_element567  label="H_element : 0.252"  # scripted group (container) (typed FeaturePython)
  n = 0.064
FEATURE [App::DocumentObjectGroupPython] C_element607  label="C_element : 0.981"  # scripted group (container) (typed FeaturePython)
  n = 0.278
FEATURE [App::DocumentObjectGroupPython] N_element282  label="N_element : 0.833"  # scripted group (container) (typed FeaturePython)
  n = 0.027
FEATURE [App::DocumentObjectGroupPython] O_element534  label="O_element : 0.973"  # scripted group (container) (typed FeaturePython)
  n = 0.41
FEATURE [App::DocumentObjectGroupPython] Mg_element045  label="Mg_element : 0.150"  # scripted group (container) (typed FeaturePython)
  n = 0.002
FEATURE [App::DocumentObjectGroupPython] P_element078  label="P_element : 0.139"  # scripted group (container) (typed FeaturePython)
  n = 0.07
FEATURE [App::DocumentObjectGroupPython] S_element096  label="S_element : 0.067"  # scripted group (container) (typed FeaturePython)
  n = 0.002
FEATURE [App::DocumentObjectGroupPython] Ca_element059  label="Ca_element : 0.242"  # scripted group (container) (typed FeaturePython)
  n = 0.147
FEATURE [App::DocumentObjectGroupPython] G4_BONE_COMPACT_ICRU  # scripted group (container) (typed FeaturePython)
  Dunit = g/cm3
  Dvalue = 1.85
  Group = -> [H_element567,C_element607,N_element282,O_element534,Mg_element045,P_element078,S_element096,Ca_element059]
  conduct = 2
  density = 1
  expand = 3
  formula = G4_BONE_COMPACT_ICRU
  name = G4_BONE_COMPACT_ICRU
  specific = 4
FEATURE [App::DocumentObjectGroupPython] H_element568  label="H_element : 0.253"  # scripted group (container) (typed FeaturePython)
  n = 0.034
FEATURE [App::DocumentObjectGroupPython] C_element608  label="C_element : 0.982"  # scripted group (container) (typed FeaturePython)
  n = 0.155
FEATURE [App::DocumentObjectGroupPython] N_element283  label="N_element : 0.834"  # scripted group (container) (typed FeaturePython)
  n = 0.042
FEATURE [App::DocumentObjectGroupPython] O_element535  label="O_element : 0.974"  # scripted group (container) (typed FeaturePython)
  n = 0.435
FEATURE [App::DocumentObjectGroupPython] Na_element083  label="Na_element : 0.144"  # scripted group (container) (typed FeaturePython)
  n = 0.001
FEATURE [App::DocumentObjectGroupPython] Mg_element046  label="Mg_element : 0.151"  # scripted group (container) (typed FeaturePython)
  n = 0.002
FEATURE [App::DocumentObjectGroupPython] P_element079  label="P_element : 0.140"  # scripted group (container) (typed FeaturePython)
  n = 0.103
FEATURE [App::DocumentObjectGroupPython] S_element097  label="S_element : 0.068"  # scripted group (container) (typed FeaturePython)
  n = 0.003
FEATURE [App::DocumentObjectGroupPython] Ca_element060  label="Ca_element : 0.243"  # scripted group (container) (typed FeaturePython)
  n = 0.225
FEATURE [App::DocumentObjectGroupPython] G4_BONE_CORTICAL_ICRP  # scripted group (container) (typed FeaturePython)
  Dunit = g/cm3
  Dvalue = 1.92
  Group = -> [H_element568,C_element608,N_element283,O_element535,Na_element083,Mg_element046,P_element079,S_element097,Ca_element060]
  conduct = 2
  density = 1
  expand = 3
  formula = G4_BONE_CORTICAL_ICRP
  name = G4_BONE_CORTICAL_ICRP
  specific = 4
FEATURE [App::DocumentObjectGroupPython] B_element029  label="B_element : 023"  # scripted group (container) (typed FeaturePython)
  n = 4
  ref = B_element
FEATURE [App::DocumentObjectGroupPython] C_element609  label="C_element : 397"  # scripted group (container) (typed FeaturePython)
  n = 1
  ref = C_element
FEATURE [App::DocumentObjectGroupPython] G4_BORON_CARBIDE  # scripted group (container) (typed FeaturePython)
  Dunit = g/cm3
  Dvalue = 2.52
  Group = -> [B_element029,C_element609]
  conduct = 2
  density = 1
  expand = 3
  formula = G4_BORON_CARBIDE
  name = G4_BORON_CARBIDE
  specific = 4
FEATURE [App::DocumentObjectGroupPython] B_element030  label="B_element : 024"  # scripted group (container) (typed FeaturePython)
  n = 2
  ref = B_element
FEATURE [App::DocumentObjectGroupPython] O_element536  label="O_element : 341"  # scripted group (container) (typed FeaturePython)
  n = 3
  ref = O_element
FEATURE [App::DocumentObjectGroupPython] G4_BORON_OXIDE  # scripted group (container) (typed FeaturePython)
  Dunit = g/cm3
  Dvalue = 1.812
  Group = -> [B_element030,O_element536]
  conduct = 2
  density = 1
  expand = 3
  formula = G4_BORON_OXIDE
  name = G4_BORON_OXIDE
  specific = 4
FEATURE [App::DocumentObjectGroupPython] H_element569  label="H_element : 0.254"  # scripted group (container) (typed FeaturePython)
  n = 0.107
FEATURE [App::DocumentObjectGroupPython] C_element610  label="C_element : 0.983"  # scripted group (container) (typed FeaturePython)
  n = 0.145
FEATURE [App::DocumentObjectGroupPython] N_element284  label="N_element : 0.835"  # scripted group (container) (typed FeaturePython)
  n = 0.022
FEATURE [App::DocumentObjectGroupPython] O_element537  label="O_element : 0.975"  # scripted group (container) (typed FeaturePython)
  n = 0.712
FEATURE [App::DocumentObjectGroupPython] Na_element084  label="Na_element : 0.145"  # scripted group (container) (typed FeaturePython)
  n = 0.002
FEATURE [App::DocumentObjectGroupPython] P_element080  label="P_element : 0.141"  # scripted group (container) (typed FeaturePython)
  n = 0.004
FEATURE [App::DocumentObjectGroupPython] S_element098  label="S_element : 0.069"  # scripted group (container) (typed FeaturePython)
  n = 0.002
FEATURE [App::DocumentObjectGroupPython] Cl_element123  label="Cl_element : 0.629"  # scripted group (container) (typed FeaturePython)
  n = 0.003
FEATURE [App::DocumentObjectGroupPython] K_element054  label="K_element : 0.045"  # scripted group (container) (typed FeaturePython)
  n = 0.003
FEATURE [App::DocumentObjectGroupPython] G4_BRAIN_ICRP  # scripted group (container) (typed FeaturePython)
  Dunit = g/cm3
  Dvalue = 1.04
  Group = -> [H_element569,C_element610,N_element284,O_element537,Na_element084,P_element080,S_element098,Cl_element123,K_element054]
  conduct = 2
  density = 1
  expand = 3
  formula = G4_BRAIN_ICRP
  name = G4_BRAIN_ICRP
  specific = 4
FEATURE [App::DocumentObjectGroupPython] C_element611  label="C_element : 398"  # scripted group (container) (typed FeaturePython)
  n = 4
  ref = C_element
FEATURE [App::DocumentObjectGroupPython] H_element570  label="H_element : 366"  # scripted group (container) (typed FeaturePython)
  n = 10
  ref = H_element
FEATURE [App::DocumentObjectGroupPython] G4_BUTANE  # scripted group (container) (typed FeaturePython)
  Dunit = g/cm3
  Dvalue = 0.00249343
  Group = -> [C_element611,H_element570]
  conduct = 2
  density = 1
  expand = 3
  formula = G4_BUTANE
  name = G4_BUTANE
  specific = 4
FEATURE [App::DocumentObjectGroupPython] C_element612  label="C_element : 399"  # scripted group (container) (typed FeaturePython)
  n = 4
  ref = C_element
FEATURE [App::DocumentObjectGroupPython] H_element571  label="H_element : 367"  # scripted group (container) (typed FeaturePython)
  n = 10
  ref = H_element
FEATURE [App::DocumentObjectGroupPython] O_element538  label="O_element : 342"  # scripted group (container) (typed FeaturePython)
  n = 1
  ref = O_element
FEATURE [App::DocumentObjectGroupPython] G4_N_BUTYL_ALCOHOL  label="G4_N-BUTYL_ALCOHOL"  # scripted group (container) (typed FeaturePython)
  Dunit = g/cm3
  Dvalue = 0.8098
  Group = -> [C_element612,H_element571,O_element538]
  conduct = 2
  density = 1
  expand = 3
  formula = G4_N-BUTYL_ALCOHOL
  name = G4_N-BUTYL_ALCOHOL
  specific = 4
FEATURE [App::DocumentObjectGroupPython] H_element572  label="H_element : 0.255"  # scripted group (container) (typed FeaturePython)
  n = 0.02468
FEATURE [App::DocumentObjectGroupPython] C_element613  label="C_element : 0.984"  # scripted group (container) (typed FeaturePython)
  n = 0.501611
FEATURE [App::DocumentObjectGroupPython] O_element539  label="O_element : 0.976"  # scripted group (container) (typed FeaturePython)
  n = 0.004527
FEATURE [App::DocumentObjectGroupPython] F_element080  label="F_element : 0.729"  # scripted group (container) (typed FeaturePython)
  n = 0.465209
FEATURE [App::DocumentObjectGroupPython] Si_element029  label="Si_element : 0.390"  # scripted group (container) (typed FeaturePython)
  n = 0.003973
FEATURE [App::DocumentObjectGroupPython] G4_C_552  label="G4_C-552"  # scripted group (container) (typed FeaturePython)
  Dunit = g/cm3
  Dvalue = 1.76
  Group = -> [H_element572,C_element613,O_element539,F_element080,Si_element029]
  conduct = 2
  density = 1
  expand = 3
  formula = G4_C-552
  name = G4_C-552
  specific = 4
FEATURE [App::DocumentObjectGroupPython] Cd_element013  label="Cd_element : 012"  # scripted group (container) (typed FeaturePython)
  n = 1
  ref = Cd_element
FEATURE [App::DocumentObjectGroupPython] Te_element009  label="Te_element : 008"  # scripted group (container) (typed FeaturePython)
  n = 1
  ref = Te_element
FEATURE [App::DocumentObjectGroupPython] G4_CADMIUM_TELLURIDE  # scripted group (container) (typed FeaturePython)
  Dunit = g/cm3
  Dvalue = 6.2
  Group = -> [Cd_element013,Te_element009]
  conduct = 2
  density = 1
  expand = 3
  formula = G4_CADMIUM_TELLURIDE
  name = G4_CADMIUM_TELLURIDE
  specific = 4
FEATURE [App::DocumentObjectGroupPython] Cd_element014  label="Cd_element : 013"  # scripted group (container) (typed FeaturePython)
  n = 1
  ref = Cd_element
FEATURE [App::DocumentObjectGroupPython] W_element021  label="W_element : 020"  # scripted group (container) (typed FeaturePython)
  n = 1
  ref = W_element
FEATURE [App::DocumentObjectGroupPython] O_element540  label="O_element : 343"  # scripted group (container) (typed FeaturePython)
  n = 4
  ref = O_element
FEATURE [App::DocumentObjectGroupPython] G4_CADMIUM_TUNGSTATE  # scripted group (container) (typed FeaturePython)
  Dunit = g/cm3
  Dvalue = 7.9
  Group = -> [Cd_element014,W_element021,O_element540]
  conduct = 2
  density = 1
  expand = 3
  formula = G4_CADMIUM_TUNGSTATE
  name = G4_CADMIUM_TUNGSTATE
  specific = 4
FEATURE [App::DocumentObjectGroupPython] Ca_element061  label="Ca_element : 028"  # scripted group (container) (typed FeaturePython)
  n = 1
  ref = Ca_element
FEATURE [App::DocumentObjectGroupPython] C_element614  label="C_element : 400"  # scripted group (container) (typed FeaturePython)
  n = 1
  ref = C_element
FEATURE [App::DocumentObjectGroupPython] O_element541  label="O_element : 344"  # scripted group (container) (typed FeaturePython)
  n = 3
  ref = O_element
FEATURE [App::DocumentObjectGroupPython] G4_CALCIUM_CARBONATE  # scripted group (container) (typed FeaturePython)
  Dunit = g/cm3
  Dvalue = 2.8
  Group = -> [Ca_element061,C_element614,O_element541]
  conduct = 2
  density = 1
  expand = 3
  formula = G4_CALCIUM_CARBONATE
  name = G4_CALCIUM_CARBONATE
  specific = 4
FEATURE [App::DocumentObjectGroupPython] Ca_element062  label="Ca_element : 029"  # scripted group (container) (typed FeaturePython)
  n = 1
  ref = Ca_element
FEATURE [App::DocumentObjectGroupPython] F_element081  label="F_element : 038"  # scripted group (container) (typed FeaturePython)
  n = 2
  ref = F_element
FEATURE [App::DocumentObjectGroupPython] G4_CALCIUM_FLUORIDE  # scripted group (container) (typed FeaturePython)
  Dunit = g/cm3
  Dvalue = 3.18
  Group = -> [Ca_element062,F_element081]
  conduct = 2
  density = 1
  expand = 3
  formula = G4_CALCIUM_FLUORIDE
  name = G4_CALCIUM_FLUORIDE
  specific = 4
FEATURE [App::DocumentObjectGroupPython] Ca_element063  label="Ca_element : 030"  # scripted group (container) (typed FeaturePython)
  n = 1
  ref = Ca_element
FEATURE [App::DocumentObjectGroupPython] O_element542  label="O_element : 345"  # scripted group (container) (typed FeaturePython)
  n = 1
  ref = O_element
FEATURE [App::DocumentObjectGroupPython] G4_CALCIUM_OXIDE  # scripted group (container) (typed FeaturePython)
  Dunit = g/cm3
  Dvalue = 3.3
  Group = -> [Ca_element063,O_element542]
  conduct = 2
  density = 1
  expand = 3
  formula = G4_CALCIUM_OXIDE
  name = G4_CALCIUM_OXIDE
  specific = 4
FEATURE [App::DocumentObjectGroupPython] Ca_element064  label="Ca_element : 031"  # scripted group (container) (typed FeaturePython)
  n = 1
  ref = Ca_element
FEATURE [App::DocumentObjectGroupPython] S_element099  label="S_element : 029"  # scripted group (container) (typed FeaturePython)
  n = 1
  ref = S_element
FEATURE [App::DocumentObjectGroupPython] O_element543  label="O_element : 346"  # scripted group (container) (typed FeaturePython)
  n = 4
  ref = O_element
FEATURE [App::DocumentObjectGroupPython] G4_CALCIUM_SULFATE  # scripted group (container) (typed FeaturePython)
  Dunit = g/cm3
  Dvalue = 2.96
  Group = -> [Ca_element064,S_element099,O_element543]
  conduct = 2
  density = 1
  expand = 3
  formula = G4_CALCIUM_SULFATE
  name = G4_CALCIUM_SULFATE
  specific = 4
FEATURE [App::DocumentObjectGroupPython] Ca_element065  label="Ca_element : 032"  # scripted group (container) (typed FeaturePython)
  n = 1
  ref = Ca_element
FEATURE [App::DocumentObjectGroupPython] W_element022  label="W_element : 021"  # scripted group (container) (typed FeaturePython)
  n = 1
  ref = W_element
FEATURE [App::DocumentObjectGroupPython] O_element544  label="O_element : 347"  # scripted group (container) (typed FeaturePython)
  n = 4
  ref = O_element
FEATURE [App::DocumentObjectGroupPython] G4_CALCIUM_TUNGSTATE  # scripted group (container) (typed FeaturePython)
  Dunit = g/cm3
  Dvalue = 6.062
  Group = -> [Ca_element065,W_element022,O_element544]
  conduct = 2
  density = 1
  expand = 3
  formula = G4_CALCIUM_TUNGSTATE
  name = G4_CALCIUM_TUNGSTATE
  specific = 4
FEATURE [App::DocumentObjectGroupPython] C_element615  label="C_element : 401"  # scripted group (container) (typed FeaturePython)
  n = 1
  ref = C_element
FEATURE [App::DocumentObjectGroupPython] O_element545  label="O_element : 348"  # scripted group (container) (typed FeaturePython)
  n = 2
  ref = O_element
FEATURE [App::DocumentObjectGroupPython] G4_CARBON_DIOXIDE  # scripted group (container) (typed FeaturePython)
  Dunit = g/cm3
  Dvalue = 0.00184212
  Group = -> [C_element615,O_element545]
  conduct = 2
  density = 1
  expand = 3
  formula = G4_CARBON_DIOXIDE
  name = G4_CARBON_DIOXIDE
  specific = 4
FEATURE [App::DocumentObjectGroupPython] C_element616  label="C_element : 402"  # scripted group (container) (typed FeaturePython)
  n = 1
  ref = C_element
FEATURE [App::DocumentObjectGroupPython] Cl_element124  label="Cl_element : 061"  # scripted group (container) (typed FeaturePython)
  n = 4
  ref = Cl_element
FEATURE [App::DocumentObjectGroupPython] G4_CARBON_TETRACHLORIDE  # scripted group (container) (typed FeaturePython)
  Dunit = g/cm3
  Dvalue = 1.594
  Group = -> [C_element616,Cl_element124]
  conduct = 2
  density = 1
  expand = 3
  formula = G4_CARBON_TETRACHLORIDE
  name = G4_CARBON_TETRACHLORIDE
  specific = 4
FEATURE [App::DocumentObjectGroupPython] C_element617  label="C_element : 403"  # scripted group (container) (typed FeaturePython)
  n = 6
  ref = C_element
FEATURE [App::DocumentObjectGroupPython] H_element573  label="H_element : 368"  # scripted group (container) (typed FeaturePython)
  n = 10
  ref = H_element
FEATURE [App::DocumentObjectGroupPython] O_element546  label="O_element : 349"  # scripted group (container) (typed FeaturePython)
  n = 5
  ref = O_element
FEATURE [App::DocumentObjectGroupPython] G4_CELLULOSE_CELLOPHANE  # scripted group (container) (typed FeaturePython)
  Dunit = g/cm3
  Dvalue = 1.42
  Group = -> [C_element617,H_element573,O_element546]
  conduct = 2
  density = 1
  expand = 3
  formula = G4_CELLULOSE_CELLOPHANE
  name = G4_CELLULOSE_CELLOPHANE
  specific = 4
FEATURE [App::DocumentObjectGroupPython] H_element574  label="H_element : 0.256"  # scripted group (container) (typed FeaturePython)
  n = 0.067125
FEATURE [App::DocumentObjectGroupPython] C_element618  label="C_element : 0.985"  # scripted group (container) (typed FeaturePython)
  n = 0.545403
FEATURE [App::DocumentObjectGroupPython] O_element547  label="O_element : 0.977"  # scripted group (container) (typed FeaturePython)
  n = 0.387472
FEATURE [App::DocumentObjectGroupPython] G4_CELLULOSE_BUTYRATE  # scripted group (container) (typed FeaturePython)
  Dunit = g/cm3
  Dvalue = 1.2
  Group = -> [H_element574,C_element618,O_element547]
  conduct = 2
  density = 1
  expand = 3
  formula = G4_CELLULOSE_BUTYRATE
  name = G4_CELLULOSE_BUTYRATE
  specific = 4
FEATURE [App::DocumentObjectGroupPython] H_element575  label="H_element : 0.257"  # scripted group (container) (typed FeaturePython)
  n = 0.029216
FEATURE [App::DocumentObjectGroupPython] C_element619  label="C_element : 0.986"  # scripted group (container) (typed FeaturePython)
  n = 0.271296
FEATURE [App::DocumentObjectGroupPython] N_element285  label="N_element : 0.836"  # scripted group (container) (typed FeaturePython)
  n = 0.121276
FEATURE [App::DocumentObjectGroupPython] O_element548  label="O_element : 0.978"  # scripted group (container) (typed FeaturePython)
  n = 0.578212
FEATURE [App::DocumentObjectGroupPython] G4_CELLULOSE_NITRATE  # scripted group (container) (typed FeaturePython)
  Dunit = g/cm3
  Dvalue = 1.49
  Group = -> [H_element575,C_element619,N_element285,O_element548]
  conduct = 2
  density = 1
  expand = 3
  formula = G4_CELLULOSE_NITRATE
  name = G4_CELLULOSE_NITRATE
  specific = 4
FEATURE [App::DocumentObjectGroupPython] H_element576  label="H_element : 0.258"  # scripted group (container) (typed FeaturePython)
  n = 0.107596
FEATURE [App::DocumentObjectGroupPython] N_element286  label="N_element : 0.837"  # scripted group (container) (typed FeaturePython)
  n = 0.0008
FEATURE [App::DocumentObjectGroupPython] O_element549  label="O_element : 0.979"  # scripted group (container) (typed FeaturePython)
  n = 0.874976
FEATURE [App::DocumentObjectGroupPython] S_element100  label="S_element : 0.070"  # scripted group (container) (typed FeaturePython)
  n = 0.014627
FEATURE [App::DocumentObjectGroupPython] Ce_element009  label="Ce_element : 0.005"  # scripted group (container) (typed FeaturePython)
  n = 0.002001
FEATURE [App::DocumentObjectGroupPython] G4_CERIC_SULFATE  # scripted group (container) (typed FeaturePython)
  Dunit = g/cm3
  Dvalue = 1.03
  Group = -> [H_element576,N_element286,O_element549,S_element100,Ce_element009]
  conduct = 2
  density = 1
  expand = 3
  formula = G4_CERIC_SULFATE
  name = G4_CERIC_SULFATE
  specific = 4
FEATURE [App::DocumentObjectGroupPython] Cs_element013  label="Cs_element : 012"  # scripted group (container) (typed FeaturePython)
  n = 1
  ref = Cs_element
FEATURE [App::DocumentObjectGroupPython] F_element082  label="F_element : 039"  # scripted group (container) (typed FeaturePython)
  n = 1
  ref = F_element
FEATURE [App::DocumentObjectGroupPython] G4_CESIUM_FLUORIDE  # scripted group (container) (typed FeaturePython)
  Dunit = g/cm3
  Dvalue = 4.115
  Group = -> [Cs_element013,F_element082]
  conduct = 2
  density = 1
  expand = 3
  formula = G4_CESIUM_FLUORIDE
  name = G4_CESIUM_FLUORIDE
  specific = 4
FEATURE [App::DocumentObjectGroupPython] Cs_element014  label="Cs_element : 013"  # scripted group (container) (typed FeaturePython)
  n = 1
  ref = Cs_element
FEATURE [App::DocumentObjectGroupPython] I_element041  label="I_element : 026"  # scripted group (container) (typed FeaturePython)
  n = 1
  ref = I_element
FEATURE [App::DocumentObjectGroupPython] G4_CESIUM_IODIDE  # scripted group (container) (typed FeaturePython)
  Dunit = g/cm3
  Dvalue = 4.51
  Group = -> [Cs_element014,I_element041]
  conduct = 2
  density = 1
  expand = 3
  formula = G4_CESIUM_IODIDE
  name = G4_CESIUM_IODIDE
  specific = 4
FEATURE [App::DocumentObjectGroupPython] C_element620  label="C_element : 404"  # scripted group (container) (typed FeaturePython)
  n = 6
  ref = C_element
FEATURE [App::DocumentObjectGroupPython] H_element577  label="H_element : 369"  # scripted group (container) (typed FeaturePython)
  n = 5
  ref = H_element
FEATURE [App::DocumentObjectGroupPython] Cl_element125  label="Cl_element : 062"  # scripted group (container) (typed FeaturePython)
  n = 1
  ref = Cl_element
FEATURE [App::DocumentObjectGroupPython] G4_CHLOROBENZENE  # scripted group (container) (typed FeaturePython)
  Dunit = g/cm3
  Dvalue = 1.1058
  Group = -> [C_element620,H_element577,Cl_element125]
  conduct = 2
  density = 1
  expand = 3
  formula = G4_CHLOROBENZENE
  name = G4_CHLOROBENZENE
  specific = 4
FEATURE [App::DocumentObjectGroupPython] C_element621  label="C_element : 405"  # scripted group (container) (typed FeaturePython)
  n = 1
  ref = C_element
FEATURE [App::DocumentObjectGroupPython] H_element578  label="H_element : 370"  # scripted group (container) (typed FeaturePython)
  n = 1
  ref = H_element
FEATURE [App::DocumentObjectGroupPython] Cl_element126  label="Cl_element : 063"  # scripted group (container) (typed FeaturePython)
  n = 3
  ref = Cl_element
FEATURE [App::DocumentObjectGroupPython] G4_CHLOROFORM  # scripted group (container) (typed FeaturePython)
  Dunit = g/cm3
  Dvalue = 1.4832
  Group = -> [C_element621,H_element578,Cl_element126]
  conduct = 2
  density = 1
  expand = 3
  formula = G4_CHLOROFORM
  name = G4_CHLOROFORM
  specific = 4
FEATURE [App::DocumentObjectGroupPython] H_element579  label="H_element : 0.259"  # scripted group (container) (typed FeaturePython)
  n = 0.01
FEATURE [App::DocumentObjectGroupPython] C_element622  label="C_element : 0.987"  # scripted group (container) (typed FeaturePython)
  n = 0.001
FEATURE [App::DocumentObjectGroupPython] O_element550  label="O_element : 0.980"  # scripted group (container) (typed FeaturePython)
  n = 0.529107
FEATURE [App::DocumentObjectGroupPython] Na_element085  label="Na_element : 0.146"  # scripted group (container) (typed FeaturePython)
  n = 0.016
FEATURE [App::DocumentObjectGroupPython] Mg_element047  label="Mg_element : 0.152"  # scripted group (container) (typed FeaturePython)
  n = 0.002
FEATURE [App::DocumentObjectGroupPython] Al_element018  label="Al_element : 0.039"  # scripted group (container) (typed FeaturePython)
  n = 0.033872
FEATURE [App::DocumentObjectGroupPython] Si_element030  label="Si_element : 0.391"  # scripted group (container) (typed FeaturePython)
  n = 0.337021
FEATURE [App::DocumentObjectGroupPython] K_element055  label="K_element : 0.046"  # scripted group (container) (typed FeaturePython)
  n = 0.013
FEATURE [App::DocumentObjectGroupPython] Ca_element066  label="Ca_element : 0.244"  # scripted group (container) (typed FeaturePython)
  n = 0.044
FEATURE [App::DocumentObjectGroupPython] Fe_element034  label="Fe_element : 0.022"  # scripted group (container) (typed FeaturePython)
  n = 0.014
FEATURE [App::DocumentObjectGroupPython] G4_CONCRETE  # scripted group (container) (typed FeaturePython)
  Dunit = g/cm3
  Dvalue = 2.3
  Group = -> [H_element579,C_element622,O_element550,Na_element085,Mg_element047,Al_element018,Si_element030,K_element055,Ca_element066,Fe_element034]
  conduct = 2
  density = 1
  expand = 3
  formula = G4_CONCRETE
  name = G4_CONCRETE
  specific = 4
FEATURE [App::DocumentObjectGroupPython] C_element623  label="C_element : 406"  # scripted group (container) (typed FeaturePython)
  n = 6
  ref = C_element
FEATURE [App::DocumentObjectGroupPython] H_element580  label="H_element : 371"  # scripted group (container) (typed FeaturePython)
  n = 12
  ref = H_element
FEATURE [App::DocumentObjectGroupPython] G4_CYCLOHEXANE  # scripted group (container) (typed FeaturePython)
  Dunit = g/cm3
  Dvalue = 0.779
  Group = -> [C_element623,H_element580]
  conduct = 2
  density = 1
  expand = 3
  formula = G4_CYCLOHEXANE
  name = G4_CYCLOHEXANE
  specific = 4
FEATURE [App::DocumentObjectGroupPython] C_element624  label="C_element : 407"  # scripted group (container) (typed FeaturePython)
  n = 6
  ref = C_element
FEATURE [App::DocumentObjectGroupPython] H_element581  label="H_element : 372"  # scripted group (container) (typed FeaturePython)
  n = 4
  ref = H_element
FEATURE [App::DocumentObjectGroupPython] Cl_element127  label="Cl_element : 064"  # scripted group (container) (typed FeaturePython)
  n = 2
  ref = Cl_element
FEATURE [App::DocumentObjectGroupPython] G4_1_2_DICHLOROBENZENE  label="G4_1.2-DICHLOROBENZENE"  # scripted group (container) (typed FeaturePython)
  Dunit = g/cm3
  Dvalue = 1.3048
  Group = -> [C_element624,H_element581,Cl_element127]
  conduct = 2
  density = 1
  expand = 3
  formula = G4_1.2-DICHLOROBENZENE
  name = G4_1.2-DICHLOROBENZENE
  specific = 4
FEATURE [App::DocumentObjectGroupPython] C_element625  label="C_element : 408"  # scripted group (container) (typed FeaturePython)
  n = 4
  ref = C_element
FEATURE [App::DocumentObjectGroupPython] H_element582  label="H_element : 373"  # scripted group (container) (typed FeaturePython)
  n = 8
  ref = H_element
FEATURE [App::DocumentObjectGroupPython] O_element551  label="O_element : 350"  # scripted group (container) (typed FeaturePython)
  n = 1
  ref = O_element
FEATURE [App::DocumentObjectGroupPython] Cl_element128  label="Cl_element : 065"  # scripted group (container) (typed FeaturePython)
  n = 2
  ref = Cl_element
FEATURE [App::DocumentObjectGroupPython] G4_DICHLORODIETHYL_ETHER  # scripted group (container) (typed FeaturePython)
  Dunit = g/cm3
  Dvalue = 1.2199
  Group = -> [C_element625,H_element582,O_element551,Cl_element128]
  conduct = 2
  density = 1
  expand = 3
  formula = G4_DICHLORODIETHYL_ETHER
  name = G4_DICHLORODIETHYL_ETHER
  specific = 4
FEATURE [App::DocumentObjectGroupPython] C_element626  label="C_element : 409"  # scripted group (container) (typed FeaturePython)
  n = 2
  ref = C_element
FEATURE [App::DocumentObjectGroupPython] H_element583  label="H_element : 374"  # scripted group (container) (typed FeaturePython)
  n = 4
  ref = H_element
FEATURE [App::DocumentObjectGroupPython] Cl_element129  label="Cl_element : 066"  # scripted group (container) (typed FeaturePython)
  n = 2
  ref = Cl_element
FEATURE [App::DocumentObjectGroupPython] G4_1_2_DICHLOROETHANE  label="G4_1.2-DICHLOROETHANE"  # scripted group (container) (typed FeaturePython)
  Dunit = g/cm3
  Dvalue = 1.2351
  Group = -> [C_element626,H_element583,Cl_element129]
  conduct = 2
  density = 1
  expand = 3
  formula = G4_1.2-DICHLOROETHANE
  name = G4_1.2-DICHLOROETHANE
  specific = 4
FEATURE [App::DocumentObjectGroupPython] C_element627  label="C_element : 410"  # scripted group (container) (typed FeaturePython)
  n = 4
  ref = C_element
FEATURE [App::DocumentObjectGroupPython] H_element584  label="H_element : 375"  # scripted group (container) (typed FeaturePython)
  n = 10
  ref = H_element
FEATURE [App::DocumentObjectGroupPython] O_element552  label="O_element : 351"  # scripted group (container) (typed FeaturePython)
  n = 1
  ref = O_element
FEATURE [App::DocumentObjectGroupPython] G4_DIETHYL_ETHER  # scripted group (container) (typed FeaturePython)
  Dunit = g/cm3
  Dvalue = 0.71378
  Group = -> [C_element627,H_element584,O_element552]
  conduct = 2
  density = 1
  expand = 3
  formula = G4_DIETHYL_ETHER
  name = G4_DIETHYL_ETHER
  specific = 4
FEATURE [App::DocumentObjectGroupPython] C_element628  label="C_element : 411"  # scripted group (container) (typed FeaturePython)
  n = 3
  ref = C_element
FEATURE [App::DocumentObjectGroupPython] H_element585  label="H_element : 376"  # scripted group (container) (typed FeaturePython)
  n = 7
  ref = H_element
FEATURE [App::DocumentObjectGroupPython] N_element287  label="N_element : 158"  # scripted group (container) (typed FeaturePython)
  n = 1
  ref = N_element
FEATURE [App::DocumentObjectGroupPython] O_element553  label="O_element : 352"  # scripted group (container) (typed FeaturePython)
  n = 1
  ref = O_element
FEATURE [App::DocumentObjectGroupPython] G4_N_N_DIMETHYL_FORMAMIDE  label="G4_N.N-DIMETHYL_FORMAMIDE"  # scripted group (container) (typed FeaturePython)
  Dunit = g/cm3
  Dvalue = 0.9487
  Group = -> [C_element628,H_element585,N_element287,O_element553]
  conduct = 2
  density = 1
  expand = 3
  formula = G4_N.N-DIMETHYL_FORMAMIDE
  name = G4_N.N-DIMETHYL_FORMAMIDE
  specific = 4
FEATURE [App::DocumentObjectGroupPython] C_element629  label="C_element : 412"  # scripted group (container) (typed FeaturePython)
  n = 2
  ref = C_element
FEATURE [App::DocumentObjectGroupPython] H_element586  label="H_element : 377"  # scripted group (container) (typed FeaturePython)
  n = 6
  ref = H_element
FEATURE [App::DocumentObjectGroupPython] O_element554  label="O_element : 353"  # scripted group (container) (typed FeaturePython)
  n = 1
  ref = O_element
FEATURE [App::DocumentObjectGroupPython] S_element101  label="S_element : 030"  # scripted group (container) (typed FeaturePython)
  n = 1
  ref = S_element
FEATURE [App::DocumentObjectGroupPython] G4_DIMETHYL_SULFOXIDE  # scripted group (container) (typed FeaturePython)
  Dunit = g/cm3
  Dvalue = 1.1014
  Group = -> [C_element629,H_element586,O_element554,S_element101]
  conduct = 2
  density = 1
  expand = 3
  formula = G4_DIMETHYL_SULFOXIDE
  name = G4_DIMETHYL_SULFOXIDE
  specific = 4
FEATURE [App::DocumentObjectGroupPython] C_element630  label="C_element : 413"  # scripted group (container) (typed FeaturePython)
  n = 2
  ref = C_element
FEATURE [App::DocumentObjectGroupPython] H_element587  label="H_element : 378"  # scripted group (container) (typed FeaturePython)
  n = 6
  ref = H_element
FEATURE [App::DocumentObjectGroupPython] G4_ETHANE  # scripted group (container) (typed FeaturePython)
  Dunit = g/cm3
  Dvalue = 0.00125324
  Group = -> [C_element630,H_element587]
  conduct = 2
  density = 1
  expand = 3
  formula = G4_ETHANE
  name = G4_ETHANE
  specific = 4
FEATURE [App::DocumentObjectGroupPython] C_element631  label="C_element : 414"  # scripted group (container) (typed FeaturePython)
  n = 2
  ref = C_element
FEATURE [App::DocumentObjectGroupPython] H_element588  label="H_element : 379"  # scripted group (container) (typed FeaturePython)
  n = 6
  ref = H_element
FEATURE [App::DocumentObjectGroupPython] O_element555  label="O_element : 354"  # scripted group (container) (typed FeaturePython)
  n = 1
  ref = O_element
FEATURE [App::DocumentObjectGroupPython] G4_ETHYL_ALCOHOL  # scripted group (container) (typed FeaturePython)
  Dunit = g/cm3
  Dvalue = 0.7893
  Group = -> [C_element631,H_element588,O_element555]
  conduct = 2
  density = 1
  expand = 3
  formula = G4_ETHYL_ALCOHOL
  name = G4_ETHYL_ALCOHOL
  specific = 4
FEATURE [App::DocumentObjectGroupPython] H_element589  label="H_element : 0.260"  # scripted group (container) (typed FeaturePython)
  n = 0.090027
FEATURE [App::DocumentObjectGroupPython] C_element632  label="C_element : 0.988"  # scripted group (container) (typed FeaturePython)
  n = 0.585182
FEATURE [App::DocumentObjectGroupPython] O_element556  label="O_element : 0.981"  # scripted group (container) (typed FeaturePython)
  n = 0.324791
FEATURE [App::DocumentObjectGroupPython] G4_ETHYL_CELLULOSE  # scripted group (container) (typed FeaturePython)
  Dunit = g/cm3
  Dvalue = 1.13
  Group = -> [H_element589,C_element632,O_element556]
  conduct = 2
  density = 1
  expand = 3
  formula = G4_ETHYL_CELLULOSE
  name = G4_ETHYL_CELLULOSE
  specific = 4
FEATURE [App::DocumentObjectGroupPython] C_element633  label="C_element : 415"  # scripted group (container) (typed FeaturePython)
  n = 2
  ref = C_element
FEATURE [App::DocumentObjectGroupPython] H_element590  label="H_element : 380"  # scripted group (container) (typed FeaturePython)
  n = 4
  ref = H_element
FEATURE [App::DocumentObjectGroupPython] G4_ETHYLENE  # scripted group (container) (typed FeaturePython)
  Dunit = g/cm3
  Dvalue = 0.00117497
  Group = -> [C_element633,H_element590]
  conduct = 2
  density = 1
  expand = 3
  formula = G4_ETHYLENE
  name = G4_ETHYLENE
  specific = 4
FEATURE [App::DocumentObjectGroupPython] H_element591  label="H_element : 0.261"  # scripted group (container) (typed FeaturePython)
  n = 0.096
FEATURE [App::DocumentObjectGroupPython] C_element634  label="C_element : 0.989"  # scripted group (container) (typed FeaturePython)
  n = 0.195
FEATURE [App::DocumentObjectGroupPython] N_element288  label="N_element : 0.838"  # scripted group (container) (typed FeaturePython)
  n = 0.057
FEATURE [App::DocumentObjectGroupPython] O_element557  label="O_element : 0.982"  # scripted group (container) (typed FeaturePython)
  n = 0.646
FEATURE [App::DocumentObjectGroupPython] Na_element086  label="Na_element : 0.147"  # scripted group (container) (typed FeaturePython)
  n = 0.001
FEATURE [App::DocumentObjectGroupPython] P_element081  label="P_element : 0.142"  # scripted group (container) (typed FeaturePython)
  n = 0.001
FEATURE [App::DocumentObjectGroupPython] S_element102  label="S_element : 0.071"  # scripted group (container) (typed FeaturePython)
  n = 0.003
FEATURE [App::DocumentObjectGroupPython] Cl_element130  label="Cl_element : 0.630"  # scripted group (container) (typed FeaturePython)
  n = 0.001
FEATURE [App::DocumentObjectGroupPython] G4_EYE_LENS_ICRP  # scripted group (container) (typed FeaturePython)
  Dunit = g/cm3
  Dvalue = 1.07
  Group = -> [H_element591,C_element634,N_element288,O_element557,Na_element086,P_element081,S_element102,Cl_element130]
  conduct = 2
  density = 1
  expand = 3
  formula = G4_EYE_LENS_ICRP
  name = G4_EYE_LENS_ICRP
  specific = 4
FEATURE [App::DocumentObjectGroupPython] Fe_element035  label="Fe_element : 017"  # scripted group (container) (typed FeaturePython)
  n = 2
  ref = Fe_element
FEATURE [App::DocumentObjectGroupPython] O_element558  label="O_element : 355"  # scripted group (container) (typed FeaturePython)
  n = 3
  ref = O_element
FEATURE [App::DocumentObjectGroupPython] G4_FERRIC_OXIDE  # scripted group (container) (typed FeaturePython)
  Dunit = g/cm3
  Dvalue = 5.2
  Group = -> [Fe_element035,O_element558]
  conduct = 2
  density = 1
  expand = 3
  formula = G4_FERRIC_OXIDE
  name = G4_FERRIC_OXIDE
  specific = 4
FEATURE [App::DocumentObjectGroupPython] Fe_element036  label="Fe_element : 018"  # scripted group (container) (typed FeaturePython)
  n = 1
  ref = Fe_element
FEATURE [App::DocumentObjectGroupPython] B_element031  label="B_element : 025"  # scripted group (container) (typed FeaturePython)
  n = 1
  ref = B_element
FEATURE [App::DocumentObjectGroupPython] G4_FERROBORIDE  # scripted group (container) (typed FeaturePython)
  Dunit = g/cm3
  Dvalue = 7.15
  Group = -> [Fe_element036,B_element031]
  conduct = 2
  density = 1
  expand = 3
  formula = G4_FERROBORIDE
  name = G4_FERROBORIDE
  specific = 4
FEATURE [App::DocumentObjectGroupPython] Fe_element037  label="Fe_element : 019"  # scripted group (container) (typed FeaturePython)
  n = 1
  ref = Fe_element
FEATURE [App::DocumentObjectGroupPython] O_element559  label="O_element : 356"  # scripted group (container) (typed FeaturePython)
  n = 1
  ref = O_element
FEATURE [App::DocumentObjectGroupPython] G4_FERROUS_OXIDE  # scripted group (container) (typed FeaturePython)
  Dunit = g/cm3
  Dvalue = 5.7
  Group = -> [Fe_element037,O_element559]
  conduct = 2
  density = 1
  expand = 3
  formula = G4_FERROUS_OXIDE
  name = G4_FERROUS_OXIDE
  specific = 4
FEATURE [App::DocumentObjectGroupPython] H_element592  label="H_element : 0.262"  # scripted group (container) (typed FeaturePython)
  n = 0.108259
FEATURE [App::DocumentObjectGroupPython] N_element289  label="N_element : 0.839"  # scripted group (container) (typed FeaturePython)
  n = 2.7e-05
FEATURE [App::DocumentObjectGroupPython] O_element560  label="O_element : 0.983"  # scripted group (container) (typed FeaturePython)
  n = 0.878636
FEATURE [App::DocumentObjectGroupPython] Na_element087  label="Na_element : 0.148"  # scripted group (container) (typed FeaturePython)
  n = 2.2e-05
FEATURE [App::DocumentObjectGroupPython] S_element103  label="S_element : 0.072"  # scripted group (container) (typed FeaturePython)
  n = 0.012968
FEATURE [App::DocumentObjectGroupPython] Cl_element131  label="Cl_element : 0.631"  # scripted group (container) (typed FeaturePython)
  n = 3.4e-05
FEATURE [App::DocumentObjectGroupPython] Fe_element038  label="Fe_element : 0.023"  # scripted group (container) (typed FeaturePython)
  n = 5.4e-05
FEATURE [App::DocumentObjectGroupPython] G4_FERROUS_SULFATE  # scripted group (container) (typed FeaturePython)
  Dunit = g/cm3
  Dvalue = 1.024
  Group = -> [H_element592,N_element289,O_element560,Na_element087,S_element103,Cl_element131,Fe_element038]
  conduct = 2
  density = 1
  expand = 3
  formula = G4_FERROUS_SULFATE
  name = G4_FERROUS_SULFATE
  specific = 4
FEATURE [App::DocumentObjectGroupPython] C_element635  label="C_element : 0.990"  # scripted group (container) (typed FeaturePython)
  n = 0.099335
FEATURE [App::DocumentObjectGroupPython] F_element083  label="F_element : 0.730"  # scripted group (container) (typed FeaturePython)
  n = 0.314247
FEATURE [App::DocumentObjectGroupPython] Cl_element132  label="Cl_element : 0.632"  # scripted group (container) (typed FeaturePython)
  n = 0.586418
FEATURE [App::DocumentObjectGroupPython] G4_FREON_12  label="G4_FREON-12"  # scripted group (container) (typed FeaturePython)
  Dunit = g/cm3
  Dvalue = 1.12
  Group = -> [C_element635,F_element083,Cl_element132]
  conduct = 2
  density = 1
  expand = 3
  formula = G4_FREON-12
  name = G4_FREON-12
  specific = 4
FEATURE [App::DocumentObjectGroupPython] C_element636  label="C_element : 0.991"  # scripted group (container) (typed FeaturePython)
  n = 0.057245
FEATURE [App::DocumentObjectGroupPython] F_element084  label="F_element : 0.731"  # scripted group (container) (typed FeaturePython)
  n = 0.181096
FEATURE [App::DocumentObjectGroupPython] Br_element029  label="Br_element : 0.769"  # scripted group (container) (typed FeaturePython)
  n = 0.761659
FEATURE [App::DocumentObjectGroupPython] G4_FREON_12B2  label="G4_FREON-12B2"  # scripted group (container) (typed FeaturePython)
  Dunit = g/cm3
  Dvalue = 1.8
  Group = -> [C_element636,F_element084,Br_element029]
  conduct = 2
  density = 1
  expand = 3
  formula = G4_FREON-12B2
  name = G4_FREON-12B2
  specific = 4
FEATURE [App::DocumentObjectGroupPython] C_element637  label="C_element : 0.992"  # scripted group (container) (typed FeaturePython)
  n = 0.114983
FEATURE [App::DocumentObjectGroupPython] F_element085  label="F_element : 0.732"  # scripted group (container) (typed FeaturePython)
  n = 0.545621
FEATURE [App::DocumentObjectGroupPython] Cl_element133  label="Cl_element : 0.633"  # scripted group (container) (typed FeaturePython)
  n = 0.339396
FEATURE [App::DocumentObjectGroupPython] G4_FREON_13  label="G4_FREON-13"  # scripted group (container) (typed FeaturePython)
  Dunit = g/cm3
  Dvalue = 0.95
  Group = -> [C_element637,F_element085,Cl_element133]
  conduct = 2
  density = 1
  expand = 3
  formula = G4_FREON-13
  name = G4_FREON-13
  specific = 4
FEATURE [App::DocumentObjectGroupPython] C_element638  label="C_element : 416"  # scripted group (container) (typed FeaturePython)
  n = 1
  ref = C_element
FEATURE [App::DocumentObjectGroupPython] F_element086  label="F_element : 040"  # scripted group (container) (typed FeaturePython)
  n = 3
  ref = F_element
FEATURE [App::DocumentObjectGroupPython] Br_element030  label="Br_element : 016"  # scripted group (container) (typed FeaturePython)
  n = 1
  ref = Br_element
FEATURE [App::DocumentObjectGroupPython] G4_FREON_13B1  label="G4_FREON-13B1"  # scripted group (container) (typed FeaturePython)
  Dunit = g/cm3
  Dvalue = 1.5
  Group = -> [C_element638,F_element086,Br_element030]
  conduct = 2
  density = 1
  expand = 3
  formula = G4_FREON-13B1
  name = G4_FREON-13B1
  specific = 4
FEATURE [App::DocumentObjectGroupPython] C_element639  label="C_element : 0.993"  # scripted group (container) (typed FeaturePython)
  n = 0.061309
FEATURE [App::DocumentObjectGroupPython] F_element087  label="F_element : 0.733"  # scripted group (container) (typed FeaturePython)
  n = 0.290924
FEATURE [App::DocumentObjectGroupPython] I_element042  label="I_element : 0.657"  # scripted group (container) (typed FeaturePython)
  n = 0.647767
FEATURE [App::DocumentObjectGroupPython] G4_FREON_13I1  label="G4_FREON-13I1"  # scripted group (container) (typed FeaturePython)
  Dunit = g/cm3
  Dvalue = 1.8
  Group = -> [C_element639,F_element087,I_element042]
  conduct = 2
  density = 1
  expand = 3
  formula = G4_FREON-13I1
  name = G4_FREON-13I1
  specific = 4
FEATURE [App::DocumentObjectGroupPython] Gd_element009  label="Gd_element : 007"  # scripted group (container) (typed FeaturePython)
  n = 2
  ref = Gd_element
FEATURE [App::DocumentObjectGroupPython] O_element561  label="O_element : 357"  # scripted group (container) (typed FeaturePython)
  n = 2
  ref = O_element
FEATURE [App::DocumentObjectGroupPython] S_element104  label="S_element : 031"  # scripted group (container) (typed FeaturePython)
  n = 1
  ref = S_element
FEATURE [App::DocumentObjectGroupPython] G4_GADOLINIUM_OXYSULFIDE  # scripted group (container) (typed FeaturePython)
  Dunit = g/cm3
  Dvalue = 7.44
  Group = -> [Gd_element009,O_element561,S_element104]
  conduct = 2
  density = 1
  expand = 3
  formula = G4_GADOLINIUM_OXYSULFIDE
  name = G4_GADOLINIUM_OXYSULFIDE
  specific = 4
FEATURE [App::DocumentObjectGroupPython] Ga_element009  label="Ga_element : 008"  # scripted group (container) (typed FeaturePython)
  n = 1
  ref = Ga_element
FEATURE [App::DocumentObjectGroupPython] As_element013  label="As_element : 008"  # scripted group (container) (typed FeaturePython)
  n = 1
  ref = As_element
FEATURE [App::DocumentObjectGroupPython] G4_GALLIUM_ARSENIDE  # scripted group (container) (typed FeaturePython)
  Dunit = g/cm3
  Dvalue = 5.31
  Group = -> [Ga_element009,As_element013]
  conduct = 2
  density = 1
  expand = 3
  formula = G4_GALLIUM_ARSENIDE
  name = G4_GALLIUM_ARSENIDE
  specific = 4
FEATURE [App::DocumentObjectGroupPython] H_element593  label="H_element : 0.263"  # scripted group (container) (typed FeaturePython)
  n = 0.08118
FEATURE [App::DocumentObjectGroupPython] C_element640  label="C_element : 0.994"  # scripted group (container) (typed FeaturePython)
  n = 0.41606
FEATURE [App::DocumentObjectGroupPython] N_element290  label="N_element : 0.840"  # scripted group (container) (typed FeaturePython)
  n = 0.11124
FEATURE [App::DocumentObjectGroupPython] O_element562  label="O_element : 0.984"  # scripted group (container) (typed FeaturePython)
  n = 0.38064
FEATURE [App::DocumentObjectGroupPython] S_element105  label="S_element : 0.073"  # scripted group (container) (typed FeaturePython)
  n = 0.01088
FEATURE [App::DocumentObjectGroupPython] G4_GEL_PHOTO_EMULSION  # scripted group (container) (typed FeaturePython)
  Dunit = g/cm3
  Dvalue = 1.2914
  Group = -> [H_element593,C_element640,N_element290,O_element562,S_element105]
  conduct = 2
  density = 1
  expand = 3
  formula = G4_GEL_PHOTO_EMULSION
  name = G4_GEL_PHOTO_EMULSION
  specific = 4
FEATURE [App::DocumentObjectGroupPython] B_element032  label="B_element : 0.043"  # scripted group (container) (typed FeaturePython)
  n = 0.0400639
FEATURE [App::DocumentObjectGroupPython] O_element563  label="O_element : 0.985"  # scripted group (container) (typed FeaturePython)
  n = 0.539561
FEATURE [App::DocumentObjectGroupPython] Na_element088  label="Na_element : 0.149"  # scripted group (container) (typed FeaturePython)
  n = 0.0281909
FEATURE [App::DocumentObjectGroupPython] Al_element019  label="Al_element : 0.040"  # scripted group (container) (typed FeaturePython)
  n = 0.011644
FEATURE [App::DocumentObjectGroupPython] Si_element031  label="Si_element : 0.392"  # scripted group (container) (typed FeaturePython)
  n = 0.377219
FEATURE [App::DocumentObjectGroupPython] K_element056  label="K_element : 0.047"  # scripted group (container) (typed FeaturePython)
  n = 0.00332099
FEATURE [App::DocumentObjectGroupPython] G4_Pyrex_Glass  # scripted group (container) (typed FeaturePython)
  Dunit = g/cm3
  Dvalue = 2.23
  Group = -> [B_element032,O_element563,Na_element088,Al_element019,Si_element031,K_element056]
  conduct = 2
  density = 1
  expand = 3
  formula = G4_Pyrex_Glass
  name = G4_Pyrex_Glass
  specific = 4
FEATURE [App::DocumentObjectGroupPython] O_element564  label="O_element : 0.986"  # scripted group (container) (typed FeaturePython)
  n = 0.156453
FEATURE [App::DocumentObjectGroupPython] Si_element032  label="Si_element : 0.393"  # scripted group (container) (typed FeaturePython)
  n = 0.080866
FEATURE [App::DocumentObjectGroupPython] Ti_element017  label="Ti_element : 0.019"  # scripted group (container) (typed FeaturePython)
  n = 0.008092
FEATURE [App::DocumentObjectGroupPython] As_element014  label="As_element : 0.006"  # scripted group (container) (typed FeaturePython)
  n = 0.002651
FEATURE [App::DocumentObjectGroupPython] Pb_element025  label="Pb_element : 0.933"  # scripted group (container) (typed FeaturePython)
  n = 0.751938
FEATURE [App::DocumentObjectGroupPython] G4_GLASS_LEAD  # scripted group (container) (typed FeaturePython)
  Dunit = g/cm3
  Dvalue = 6.22
  Group = -> [O_element564,Si_element032,Ti_element017,As_element014,Pb_element025]
  conduct = 2
  density = 1
  expand = 3
  formula = G4_GLASS_LEAD
  name = G4_GLASS_LEAD
  specific = 4
FEATURE [App::DocumentObjectGroupPython] O_element565  label="O_element : 0.987"  # scripted group (container) (typed FeaturePython)
  n = 0.4598
FEATURE [App::DocumentObjectGroupPython] Na_element089  label="Na_element : 0.150"  # scripted group (container) (typed FeaturePython)
  n = 0.0964411
FEATURE [App::DocumentObjectGroupPython] Si_element033  label="Si_element : 0.394"  # scripted group (container) (typed FeaturePython)
  n = 0.336553
FEATURE [App::DocumentObjectGroupPython] Ca_element067  label="Ca_element : 0.245"  # scripted group (container) (typed FeaturePython)
  n = 0.107205
FEATURE [App::DocumentObjectGroupPython] G4_GLASS_PLATE  # scripted group (container) (typed FeaturePython)
  Dunit = g/cm3
  Dvalue = 2.4
  Group = -> [O_element565,Na_element089,Si_element033,Ca_element067]
  conduct = 2
  density = 1
  expand = 3
  formula = G4_GLASS_PLATE
  name = G4_GLASS_PLATE
  specific = 4
FEATURE [App::DocumentObjectGroupPython] C_element641  label="C_element : 417"  # scripted group (container) (typed FeaturePython)
  n = 5
  ref = C_element
FEATURE [App::DocumentObjectGroupPython] H_element594  label="H_element : 381"  # scripted group (container) (typed FeaturePython)
  n = 10
  ref = H_element
FEATURE [App::DocumentObjectGroupPython] N_element291  label="N_element : 159"  # scripted group (container) (typed FeaturePython)
  n = 2
  ref = N_element
FEATURE [App::DocumentObjectGroupPython] O_element566  label="O_element : 358"  # scripted group (container) (typed FeaturePython)
  n = 3
  ref = O_element
FEATURE [App::DocumentObjectGroupPython] G4_GLUTAMINE  # scripted group (container) (typed FeaturePython)
  Dunit = g/cm3
  Dvalue = 1.46
  Group = -> [C_element641,H_element594,N_element291,O_element566]
  conduct = 2
  density = 1
  expand = 3
  formula = G4_GLUTAMINE
  name = G4_GLUTAMINE
  specific = 4
FEATURE [App::DocumentObjectGroupPython] C_element642  label="C_element : 418"  # scripted group (container) (typed FeaturePython)
  n = 3
  ref = C_element
FEATURE [App::DocumentObjectGroupPython] H_element595  label="H_element : 382"  # scripted group (container) (typed FeaturePython)
  n = 8
  ref = H_element
FEATURE [App::DocumentObjectGroupPython] O_element567  label="O_element : 359"  # scripted group (container) (typed FeaturePython)
  n = 3
  ref = O_element
FEATURE [App::DocumentObjectGroupPython] G4_GLYCEROL  # scripted group (container) (typed FeaturePython)
  Dunit = g/cm3
  Dvalue = 1.2613
  Group = -> [C_element642,H_element595,O_element567]
  conduct = 2
  density = 1
  expand = 3
  formula = G4_GLYCEROL
  name = G4_GLYCEROL
  specific = 4
FEATURE [App::DocumentObjectGroupPython] C_element643  label="C_element : 419"  # scripted group (container) (typed FeaturePython)
  n = 5
  ref = C_element
FEATURE [App::DocumentObjectGroupPython] H_element596  label="H_element : 383"  # scripted group (container) (typed FeaturePython)
  n = 5
  ref = H_element
FEATURE [App::DocumentObjectGroupPython] N_element292  label="N_element : 160"  # scripted group (container) (typed FeaturePython)
  n = 5
  ref = N_element
FEATURE [App::DocumentObjectGroupPython] O_element568  label="O_element : 360"  # scripted group (container) (typed FeaturePython)
  n = 1
  ref = O_element
FEATURE [App::DocumentObjectGroupPython] G4_GUANINE  # scripted group (container) (typed FeaturePython)
  Dunit = g/cm3
  Dvalue = 2.2
  Group = -> [C_element643,H_element596,N_element292,O_element568]
  conduct = 2
  density = 1
  expand = 3
  formula = G4_GUANINE
  name = G4_GUANINE
  specific = 4
FEATURE [App::DocumentObjectGroupPython] Ca_element068  label="Ca_element : 033"  # scripted group (container) (typed FeaturePython)
  n = 1
  ref = Ca_element
FEATURE [App::DocumentObjectGroupPython] S_element106  label="S_element : 032"  # scripted group (container) (typed FeaturePython)
  n = 1
  ref = S_element
FEATURE [App::DocumentObjectGroupPython] O_element569  label="O_element : 361"  # scripted group (container) (typed FeaturePython)
  n = 6
  ref = O_element
FEATURE [App::DocumentObjectGroupPython] H_element597  label="H_element : 384"  # scripted group (container) (typed FeaturePython)
  n = 4
  ref = H_element
FEATURE [App::DocumentObjectGroupPython] G4_GYPSUM  # scripted group (container) (typed FeaturePython)
  Dunit = g/cm3
  Dvalue = 2.32
  Group = -> [Ca_element068,S_element106,O_element569,H_element597]
  conduct = 2
  density = 1
  expand = 3
  formula = G4_GYPSUM
  name = G4_GYPSUM
  specific = 4
FEATURE [App::DocumentObjectGroupPython] C_element644  label="C_element : 420"  # scripted group (container) (typed FeaturePython)
  n = 7
  ref = C_element
FEATURE [App::DocumentObjectGroupPython] H_element598  label="H_element : 385"  # scripted group (container) (typed FeaturePython)
  n = 16
  ref = H_element
FEATURE [App::DocumentObjectGroupPython] G4_N_HEPTANE  label="G4_N-HEPTANE"  # scripted group (container) (typed FeaturePython)
  Dunit = g/cm3
  Dvalue = 0.68376
  Group = -> [C_element644,H_element598]
  conduct = 2
  density = 1
  expand = 3
  formula = G4_N-HEPTANE
  name = G4_N-HEPTANE
  specific = 4
FEATURE [App::DocumentObjectGroupPython] C_element645  label="C_element : 421"  # scripted group (container) (typed FeaturePython)
  n = 6
  ref = C_element
FEATURE [App::DocumentObjectGroupPython] H_element599  label="H_element : 386"  # scripted group (container) (typed FeaturePython)
  n = 14
  ref = H_element
FEATURE [App::DocumentObjectGroupPython] G4_N_HEXANE  label="G4_N-HEXANE"  # scripted group (container) (typed FeaturePython)
  Dunit = g/cm3
  Dvalue = 0.6603
  Group = -> [C_element645,H_element599]
  conduct = 2
  density = 1
  expand = 3
  formula = G4_N-HEXANE
  name = G4_N-HEXANE
  specific = 4
FEATURE [App::DocumentObjectGroupPython] C_element646  label="C_element : 422"  # scripted group (container) (typed FeaturePython)
  n = 22
  ref = C_element
FEATURE [App::DocumentObjectGroupPython] H_element600  label="H_element : 387"  # scripted group (container) (typed FeaturePython)
  n = 10
  ref = H_element
FEATURE [App::DocumentObjectGroupPython] N_element293  label="N_element : 161"  # scripted group (container) (typed FeaturePython)
  n = 2
  ref = N_element
FEATURE [App::DocumentObjectGroupPython] O_element570  label="O_element : 362"  # scripted group (container) (typed FeaturePython)
  n = 5
  ref = O_element
FEATURE [App::DocumentObjectGroupPython] G4_KAPTON  # scripted group (container) (typed FeaturePython)
  Dunit = g/cm3
  Dvalue = 1.42
  Group = -> [C_element646,H_element600,N_element293,O_element570]
  conduct = 2
  density = 1
  expand = 3
  formula = G4_KAPTON
  name = G4_KAPTON
  specific = 4
FEATURE [App::DocumentObjectGroupPython] La_element013  label="La_element : 011"  # scripted group (container) (typed FeaturePython)
  n = 1
  ref = La_element
FEATURE [App::DocumentObjectGroupPython] Br_element031  label="Br_element : 017"  # scripted group (container) (typed FeaturePython)
  n = 1
  ref = Br_element
FEATURE [App::DocumentObjectGroupPython] O_element571  label="O_element : 363"  # scripted group (container) (typed FeaturePython)
  n = 1
  ref = O_element
FEATURE [App::DocumentObjectGroupPython] G4_LANTHANUM_OXYBROMIDE  # scripted group (container) (typed FeaturePython)
  Dunit = g/cm3
  Dvalue = 6.28
  Group = -> [La_element013,Br_element031,O_element571]
  conduct = 2
  density = 1
  expand = 3
  formula = G4_LANTHANUM_OXYBROMIDE
  name = G4_LANTHANUM_OXYBROMIDE
  specific = 4
FEATURE [App::DocumentObjectGroupPython] La_element014  label="La_element : 012"  # scripted group (container) (typed FeaturePython)
  n = 2
  ref = La_element
FEATURE [App::DocumentObjectGroupPython] O_element572  label="O_element : 364"  # scripted group (container) (typed FeaturePython)
  n = 2
  ref = O_element
FEATURE [App::DocumentObjectGroupPython] S_element107  label="S_element : 033"  # scripted group (container) (typed FeaturePython)
  n = 1
  ref = S_element
FEATURE [App::DocumentObjectGroupPython] G4_LANTHANUM_OXYSULFIDE  # scripted group (container) (typed FeaturePython)
  Dunit = g/cm3
  Dvalue = 5.86
  Group = -> [La_element014,O_element572,S_element107]
  conduct = 2
  density = 1
  expand = 3
  formula = G4_LANTHANUM_OXYSULFIDE
  name = G4_LANTHANUM_OXYSULFIDE
  specific = 4
FEATURE [App::DocumentObjectGroupPython] O_element573  label="O_element : 0.988"  # scripted group (container) (typed FeaturePython)
  n = 0.071682
FEATURE [App::DocumentObjectGroupPython] Pb_element026  label="Pb_element : 0.934"  # scripted group (container) (typed FeaturePython)
  n = 0.928318
FEATURE [App::DocumentObjectGroupPython] G4_LEAD_OXIDE  # scripted group (container) (typed FeaturePython)
  Dunit = g/cm3
  Dvalue = 9.53
  Group = -> [O_element573,Pb_element026]
  conduct = 2
  density = 1
  expand = 3
  formula = G4_LEAD_OXIDE
  name = G4_LEAD_OXIDE
  specific = 4
FEATURE [App::DocumentObjectGroupPython] Li_element033  label="Li_element : 031"  # scripted group (container) (typed FeaturePython)
  n = 1
  ref = Li_element
FEATURE [App::DocumentObjectGroupPython] N_element294  label="N_element : 162"  # scripted group (container) (typed FeaturePython)
  n = 1
  ref = N_element
FEATURE [App::DocumentObjectGroupPython] H_element601  label="H_element : 388"  # scripted group (container) (typed FeaturePython)
  n = 2
  ref = H_element
FEATURE [App::DocumentObjectGroupPython] G4_LITHIUM_AMIDE  # scripted group (container) (typed FeaturePython)
  Dunit = g/cm3
  Dvalue = 1.178
  Group = -> [Li_element033,N_element294,H_element601]
  conduct = 2
  density = 1
  expand = 3
  formula = G4_LITHIUM_AMIDE
  name = G4_LITHIUM_AMIDE
  specific = 4
FEATURE [App::DocumentObjectGroupPython] Li_element034  label="Li_element : 032"  # scripted group (container) (typed FeaturePython)
  n = 2
  ref = Li_element
FEATURE [App::DocumentObjectGroupPython] C_element647  label="C_element : 423"  # scripted group (container) (typed FeaturePython)
  n = 1
  ref = C_element
FEATURE [App::DocumentObjectGroupPython] O_element574  label="O_element : 365"  # scripted group (container) (typed FeaturePython)
  n = 3
  ref = O_element
FEATURE [App::DocumentObjectGroupPython] G4_LITHIUM_CARBONATE  # scripted group (container) (typed FeaturePython)
  Dunit = g/cm3
  Dvalue = 2.11
  Group = -> [Li_element034,C_element647,O_element574]
  conduct = 2
  density = 1
  expand = 3
  formula = G4_LITHIUM_CARBONATE
  name = G4_LITHIUM_CARBONATE
  specific = 4
FEATURE [App::DocumentObjectGroupPython] Li_element035  label="Li_element : 033"  # scripted group (container) (typed FeaturePython)
  n = 1
  ref = Li_element
FEATURE [App::DocumentObjectGroupPython] F_element088  label="F_element : 041"  # scripted group (container) (typed FeaturePython)
  n = 1
  ref = F_element
FEATURE [App::DocumentObjectGroupPython] G4_LITHIUM_FLUORIDE  # scripted group (container) (typed FeaturePython)
  Dunit = g/cm3
  Dvalue = 2.635
  Group = -> [Li_element035,F_element088]
  conduct = 2
  density = 1
  expand = 3
  formula = G4_LITHIUM_FLUORIDE
  name = G4_LITHIUM_FLUORIDE
  specific = 4
FEATURE [App::DocumentObjectGroupPython] Li_element036  label="Li_element : 034"  # scripted group (container) (typed FeaturePython)
  n = 1
  ref = Li_element
FEATURE [App::DocumentObjectGroupPython] H_element602  label="H_element : 389"  # scripted group (container) (typed FeaturePython)
  n = 1
  ref = H_element
FEATURE [App::DocumentObjectGroupPython] G4_LITHIUM_HYDRIDE  # scripted group (container) (typed FeaturePython)
  Dunit = g/cm3
  Dvalue = 0.82
  Group = -> [Li_element036,H_element602]
  conduct = 2
  density = 1
  expand = 3
  formula = G4_LITHIUM_HYDRIDE
  name = G4_LITHIUM_HYDRIDE
  specific = 4
FEATURE [App::DocumentObjectGroupPython] Li_element037  label="Li_element : 035"  # scripted group (container) (typed FeaturePython)
  n = 1
  ref = Li_element
FEATURE [App::DocumentObjectGroupPython] I_element043  label="I_element : 027"  # scripted group (container) (typed FeaturePython)
  n = 1
  ref = I_element
FEATURE [App::DocumentObjectGroupPython] G4_LITHIUM_IODIDE  # scripted group (container) (typed FeaturePython)
  Dunit = g/cm3
  Dvalue = 3.494
  Group = -> [Li_element037,I_element043]
  conduct = 2
  density = 1
  expand = 3
  formula = G4_LITHIUM_IODIDE
  name = G4_LITHIUM_IODIDE
  specific = 4
FEATURE [App::DocumentObjectGroupPython] Li_element038  label="Li_element : 036"  # scripted group (container) (typed FeaturePython)
  n = 2
  ref = Li_element
FEATURE [App::DocumentObjectGroupPython] O_element575  label="O_element : 366"  # scripted group (container) (typed FeaturePython)
  n = 1
  ref = O_element
FEATURE [App::DocumentObjectGroupPython] G4_LITHIUM_OXIDE  # scripted group (container) (typed FeaturePython)
  Dunit = g/cm3
  Dvalue = 2.013
  Group = -> [Li_element038,O_element575]
  conduct = 2
  density = 1
  expand = 3
  formula = G4_LITHIUM_OXIDE
  name = G4_LITHIUM_OXIDE
  specific = 4
FEATURE [App::DocumentObjectGroupPython] Li_element039  label="Li_element : 037"  # scripted group (container) (typed FeaturePython)
  n = 2
  ref = Li_element
FEATURE [App::DocumentObjectGroupPython] B_element033  label="B_element : 026"  # scripted group (container) (typed FeaturePython)
  n = 4
  ref = B_element
FEATURE [App::DocumentObjectGroupPython] O_element576  label="O_element : 367"  # scripted group (container) (typed FeaturePython)
  n = 7
  ref = O_element
FEATURE [App::DocumentObjectGroupPython] G4_LITHIUM_TETRABORATE  # scripted group (container) (typed FeaturePython)
  Dunit = g/cm3
  Dvalue = 2.44
  Group = -> [Li_element039,B_element033,O_element576]
  conduct = 2
  density = 1
  expand = 3
  formula = G4_LITHIUM_TETRABORATE
  name = G4_LITHIUM_TETRABORATE
  specific = 4
FEATURE [App::DocumentObjectGroupPython] H_element603  label="H_element : 0.264"  # scripted group (container) (typed FeaturePython)
  n = 0.105
FEATURE [App::DocumentObjectGroupPython] C_element648  label="C_element : 0.995"  # scripted group (container) (typed FeaturePython)
  n = 0.083
FEATURE [App::DocumentObjectGroupPython] N_element295  label="N_element : 0.841"  # scripted group (container) (typed FeaturePython)
  n = 0.023
FEATURE [App::DocumentObjectGroupPython] O_element577  label="O_element : 0.989"  # scripted group (container) (typed FeaturePython)
  n = 0.779
FEATURE [App::DocumentObjectGroupPython] Na_element090  label="Na_element : 0.151"  # scripted group (container) (typed FeaturePython)
  n = 0.002
FEATURE [App::DocumentObjectGroupPython] P_element082  label="P_element : 0.143"  # scripted group (container) (typed FeaturePython)
  n = 0.001
FEATURE [App::DocumentObjectGroupPython] S_element108  label="S_element : 0.074"  # scripted group (container) (typed FeaturePython)
  n = 0.002
FEATURE [App::DocumentObjectGroupPython] Cl_element134  label="Cl_element : 0.634"  # scripted group (container) (typed FeaturePython)
  n = 0.003
FEATURE [App::DocumentObjectGroupPython] K_element057  label="K_element : 0.048"  # scripted group (container) (typed FeaturePython)
  n = 0.002
FEATURE [App::DocumentObjectGroupPython] G4_LUNG_ICRP  # scripted group (container) (typed FeaturePython)
  Dunit = g/cm3
  Dvalue = 1.04
  Group = -> [H_element603,C_element648,N_element295,O_element577,Na_element090,P_element082,S_element108,Cl_element134,K_element057]
  conduct = 2
  density = 1
  expand = 3
  formula = G4_LUNG_ICRP
  name = G4_LUNG_ICRP
  specific = 4
FEATURE [App::DocumentObjectGroupPython] H_element604  label="H_element : 0.265"  # scripted group (container) (typed FeaturePython)
  n = 0.114318
FEATURE [App::DocumentObjectGroupPython] C_element649  label="C_element : 0.996"  # scripted group (container) (typed FeaturePython)
  n = 0.655824
FEATURE [App::DocumentObjectGroupPython] O_element578  label="O_element : 0.990"  # scripted group (container) (typed FeaturePython)
  n = 0.0921831
FEATURE [App::DocumentObjectGroupPython] Mg_element048  label="Mg_element : 0.153"  # scripted group (container) (typed FeaturePython)
  n = 0.134792
FEATURE [App::DocumentObjectGroupPython] Ca_element069  label="Ca_element : 0.246"  # scripted group (container) (typed FeaturePython)
  n = 0.002883
FEATURE [App::DocumentObjectGroupPython] G4_M3_WAX  # scripted group (container) (typed FeaturePython)
  Dunit = g/cm3
  Dvalue = 1.05
  Group = -> [H_element604,C_element649,O_element578,Mg_element048,Ca_element069]
  conduct = 2
  density = 1
  expand = 3
  formula = G4_M3_WAX
  name = G4_M3_WAX
  specific = 4
FEATURE [App::DocumentObjectGroupPython] Mg_element049  label="Mg_element : 020"  # scripted group (container) (typed FeaturePython)
  n = 1
  ref = Mg_element
FEATURE [App::DocumentObjectGroupPython] C_element650  label="C_element : 424"  # scripted group (container) (typed FeaturePython)
  n = 1
  ref = C_element
FEATURE [App::DocumentObjectGroupPython] O_element579  label="O_element : 368"  # scripted group (container) (typed FeaturePython)
  n = 3
  ref = O_element
FEATURE [App::DocumentObjectGroupPython] G4_MAGNESIUM_CARBONATE  # scripted group (container) (typed FeaturePython)
  Dunit = g/cm3
  Dvalue = 2.958
  Group = -> [Mg_element049,C_element650,O_element579]
  conduct = 2
  density = 1
  expand = 3
  formula = G4_MAGNESIUM_CARBONATE
  name = G4_MAGNESIUM_CARBONATE
  specific = 4
FEATURE [App::DocumentObjectGroupPython] Mg_element050  label="Mg_element : 021"  # scripted group (container) (typed FeaturePython)
  n = 1
  ref = Mg_element
FEATURE [App::DocumentObjectGroupPython] F_element089  label="F_element : 042"  # scripted group (container) (typed FeaturePython)
  n = 2
  ref = F_element
FEATURE [App::DocumentObjectGroupPython] G4_MAGNESIUM_FLUORIDE  # scripted group (container) (typed FeaturePython)
  Dunit = g/cm3
  Dvalue = 3
  Group = -> [Mg_element050,F_element089]
  conduct = 2
  density = 1
  expand = 3
  formula = G4_MAGNESIUM_FLUORIDE
  name = G4_MAGNESIUM_FLUORIDE
  specific = 4
FEATURE [App::DocumentObjectGroupPython] Mg_element051  label="Mg_element : 022"  # scripted group (container) (typed FeaturePython)
  n = 1
  ref = Mg_element
FEATURE [App::DocumentObjectGroupPython] O_element580  label="O_element : 369"  # scripted group (container) (typed FeaturePython)
  n = 1
  ref = O_element
FEATURE [App::DocumentObjectGroupPython] G4_MAGNESIUM_OXIDE  # scripted group (container) (typed FeaturePython)
  Dunit = g/cm3
  Dvalue = 3.58
  Group = -> [Mg_element051,O_element580]
  conduct = 2
  density = 1
  expand = 3
  formula = G4_MAGNESIUM_OXIDE
  name = G4_MAGNESIUM_OXIDE
  specific = 4
FEATURE [App::DocumentObjectGroupPython] Mg_element052  label="Mg_element : 023"  # scripted group (container) (typed FeaturePython)
  n = 1
  ref = Mg_element
FEATURE [App::DocumentObjectGroupPython] B_element034  label="B_element : 027"  # scripted group (container) (typed FeaturePython)
  n = 4
  ref = B_element
FEATURE [App::DocumentObjectGroupPython] O_element581  label="O_element : 370"  # scripted group (container) (typed FeaturePython)
  n = 7
  ref = O_element
FEATURE [App::DocumentObjectGroupPython] G4_MAGNESIUM_TETRABORATE  # scripted group (container) (typed FeaturePython)
  Dunit = g/cm3
  Dvalue = 2.53
  Group = -> [Mg_element052,B_element034,O_element581]
  conduct = 2
  density = 1
  expand = 3
  formula = G4_MAGNESIUM_TETRABORATE
  name = G4_MAGNESIUM_TETRABORATE
  specific = 4
FEATURE [App::DocumentObjectGroupPython] Hg_element009  label="Hg_element : 008"  # scripted group (container) (typed FeaturePython)
  n = 1
  ref = Hg_element
FEATURE [App::DocumentObjectGroupPython] I_element044  label="I_element : 028"  # scripted group (container) (typed FeaturePython)
  n = 2
  ref = I_element
FEATURE [App::DocumentObjectGroupPython] G4_MERCURIC_IODIDE  # scripted group (container) (typed FeaturePython)
  Dunit = g/cm3
  Dvalue = 6.36
  Group = -> [Hg_element009,I_element044]
  conduct = 2
  density = 1
  expand = 3
  formula = G4_MERCURIC_IODIDE
  name = G4_MERCURIC_IODIDE
  specific = 4
FEATURE [App::DocumentObjectGroupPython] C_element651  label="C_element : 425"  # scripted group (container) (typed FeaturePython)
  n = 1
  ref = C_element
FEATURE [App::DocumentObjectGroupPython] H_element605  label="H_element : 390"  # scripted group (container) (typed FeaturePython)
  n = 4
  ref = H_element
FEATURE [App::DocumentObjectGroupPython] G4_METHANE  # scripted group (container) (typed FeaturePython)
  Dunit = g/cm3
  Dvalue = 0.000667151
  Group = -> [C_element651,H_element605]
  conduct = 2
  density = 1
  expand = 3
  formula = G4_METHANE
  name = G4_METHANE
  specific = 4
FEATURE [App::DocumentObjectGroupPython] C_element652  label="C_element : 426"  # scripted group (container) (typed FeaturePython)
  n = 1
  ref = C_element
FEATURE [App::DocumentObjectGroupPython] H_element606  label="H_element : 391"  # scripted group (container) (typed FeaturePython)
  n = 4
  ref = H_element
FEATURE [App::DocumentObjectGroupPython] O_element582  label="O_element : 371"  # scripted group (container) (typed FeaturePython)
  n = 1
  ref = O_element
FEATURE [App::DocumentObjectGroupPython] G4_METHANOL  # scripted group (container) (typed FeaturePython)
  Dunit = g/cm3
  Dvalue = 0.7914
  Group = -> [C_element652,H_element606,O_element582]
  conduct = 2
  density = 1
  expand = 3
  formula = G4_METHANOL
  name = G4_METHANOL
  specific = 4
FEATURE [App::DocumentObjectGroupPython] H_element607  label="H_element : 0.266"  # scripted group (container) (typed FeaturePython)
  n = 0.13404
FEATURE [App::DocumentObjectGroupPython] C_element653  label="C_element : 0.997"  # scripted group (container) (typed FeaturePython)
  n = 0.77796
FEATURE [App::DocumentObjectGroupPython] O_element583  label="O_element : 0.991"  # scripted group (container) (typed FeaturePython)
  n = 0.03502
FEATURE [App::DocumentObjectGroupPython] Mg_element053  label="Mg_element : 0.154"  # scripted group (container) (typed FeaturePython)
  n = 0.038594
FEATURE [App::DocumentObjectGroupPython] Ti_element018  label="Ti_element : 0.020"  # scripted group (container) (typed FeaturePython)
  n = 0.014386
FEATURE [App::DocumentObjectGroupPython] G4_MIX_D_WAX  # scripted group (container) (typed FeaturePython)
  Dunit = g/cm3
  Dvalue = 0.99
  Group = -> [H_element607,C_element653,O_element583,Mg_element053,Ti_element018]
  conduct = 2
  density = 1
  expand = 3
  formula = G4_MIX_D_WAX
  name = G4_MIX_D_WAX
  specific = 4
FEATURE [App::DocumentObjectGroupPython] H_element608  label="H_element : 0.267"  # scripted group (container) (typed FeaturePython)
  n = 0.081192
FEATURE [App::DocumentObjectGroupPython] C_element654  label="C_element : 0.998"  # scripted group (container) (typed FeaturePython)
  n = 0.583442
FEATURE [App::DocumentObjectGroupPython] N_element296  label="N_element : 0.842"  # scripted group (container) (typed FeaturePython)
  n = 0.017798
FEATURE [App::DocumentObjectGroupPython] O_element584  label="O_element : 0.992"  # scripted group (container) (typed FeaturePython)
  n = 0.186381
FEATURE [App::DocumentObjectGroupPython] Mg_element054  label="Mg_element : 0.155"  # scripted group (container) (typed FeaturePython)
  n = 0.130287
FEATURE [App::DocumentObjectGroupPython] Cl_element135  label="Cl_element : 0.635"  # scripted group (container) (typed FeaturePython)
  n = 0.0009
FEATURE [App::DocumentObjectGroupPython] G4_MS20_TISSUE  # scripted group (container) (typed FeaturePython)
  Dunit = g/cm3
  Dvalue = 1
  Group = -> [H_element608,C_element654,N_element296,O_element584,Mg_element054,Cl_element135]
  conduct = 2
  density = 1
  expand = 3
  formula = G4_MS20_TISSUE
  name = G4_MS20_TISSUE
  specific = 4
FEATURE [App::DocumentObjectGroupPython] H_element609  label="H_element : 0.268"  # scripted group (container) (typed FeaturePython)
  n = 0.102
FEATURE [App::DocumentObjectGroupPython] C_element655  label="C_element : 0.999"  # scripted group (container) (typed FeaturePython)
  n = 0.143
FEATURE [App::DocumentObjectGroupPython] N_element297  label="N_element : 0.843"  # scripted group (container) (typed FeaturePython)
  n = 0.034
FEATURE [App::DocumentObjectGroupPython] O_element585  label="O_element : 0.993"  # scripted group (container) (typed FeaturePython)
  n = 0.71
FEATURE [App::DocumentObjectGroupPython] Na_element091  label="Na_element : 0.152"  # scripted group (container) (typed FeaturePython)
  n = 0.001
FEATURE [App::DocumentObjectGroupPython] P_element083  label="P_element : 0.144"  # scripted group (container) (typed FeaturePython)
  n = 0.002
FEATURE [App::DocumentObjectGroupPython] S_element109  label="S_element : 0.075"  # scripted group (container) (typed FeaturePython)
  n = 0.003
FEATURE [App::DocumentObjectGroupPython] Cl_element136  label="Cl_element : 0.636"  # scripted group (container) (typed FeaturePython)
  n = 0.001
FEATURE [App::DocumentObjectGroupPython] K_element058  label="K_element : 0.049"  # scripted group (container) (typed FeaturePython)
  n = 0.004
FEATURE [App::DocumentObjectGroupPython] G4_MUSCLE_SKELETAL_ICRP  # scripted group (container) (typed FeaturePython)
  Dunit = g/cm3
  Dvalue = 1.05
  Group = -> [H_element609,C_element655,N_element297,O_element585,Na_element091,P_element083,S_element109,Cl_element136,K_element058]
  conduct = 2
  density = 1
  expand = 3
  formula = G4_MUSCLE_SKELETAL_ICRP
  name = G4_MUSCLE_SKELETAL_ICRP
  specific = 4
FEATURE [App::DocumentObjectGroupPython] H_element610  label="H_element : 0.269"  # scripted group (container) (typed FeaturePython)
  n = 0.102102
FEATURE [App::DocumentObjectGroupPython] C_element656  label="C_element : 0.1000"  # scripted group (container) (typed FeaturePython)
  n = 0.123123
FEATURE [App::DocumentObjectGroupPython] N_element298  label="N_element : 0.844"  # scripted group (container) (typed FeaturePython)
  n = 0.035035
FEATURE [App::DocumentObjectGroupPython] O_element586  label="O_element : 0.994"  # scripted group (container) (typed FeaturePython)
  n = 0.72973
FEATURE [App::DocumentObjectGroupPython] Na_element092  label="Na_element : 0.153"  # scripted group (container) (typed FeaturePython)
  n = 0.001001
FEATURE [App::DocumentObjectGroupPython] P_element084  label="P_element : 0.145"  # scripted group (container) (typed FeaturePython)
  n = 0.002002
FEATURE [App::DocumentObjectGroupPython] S_element110  label="S_element : 0.076"  # scripted group (container) (typed FeaturePython)
  n = 0.004004
FEATURE [App::DocumentObjectGroupPython] K_element059  label="K_element : 0.050"  # scripted group (container) (typed FeaturePython)
  n = 0.003003
FEATURE [App::DocumentObjectGroupPython] G4_MUSCLE_STRIATED_ICRU  # scripted group (container) (typed FeaturePython)
  Dunit = g/cm3
  Dvalue = 1.04
  Group = -> [H_element610,C_element656,N_element298,O_element586,Na_element092,P_element084,S_element110,K_element059]
  conduct = 2
  density = 1
  expand = 3
  formula = G4_MUSCLE_STRIATED_ICRU
  name = G4_MUSCLE_STRIATED_ICRU
  specific = 4
FEATURE [App::DocumentObjectGroupPython] H_element611  label="H_element : 0.270"  # scripted group (container) (typed FeaturePython)
  n = 0.0982341
FEATURE [App::DocumentObjectGroupPython] C_element657  label="C_element : 0.1001"  # scripted group (container) (typed FeaturePython)
  n = 0.156214
FEATURE [App::DocumentObjectGroupPython] N_element299  label="N_element : 0.845"  # scripted group (container) (typed FeaturePython)
  n = 0.035451
FEATURE [App::DocumentObjectGroupPython] O_element587  label="O_element : 0.995"  # scripted group (container) (typed FeaturePython)
  n = 0.710101
FEATURE [App::DocumentObjectGroupPython] G4_MUSCLE_WITH_SUCROSE  # scripted group (container) (typed FeaturePython)
  Dunit = g/cm3
  Dvalue = 1.11
  Group = -> [H_element611,C_element657,N_element299,O_element587]
  conduct = 2
  density = 1
  expand = 3
  formula = G4_MUSCLE_WITH_SUCROSE
  name = G4_MUSCLE_WITH_SUCROSE
  specific = 4
FEATURE [App::DocumentObjectGroupPython] H_element612  label="H_element : 0.271"  # scripted group (container) (typed FeaturePython)
  n = 0.101969
FEATURE [App::DocumentObjectGroupPython] C_element658  label="C_element : 0.1002"  # scripted group (container) (typed FeaturePython)
  n = 0.120058
FEATURE [App::DocumentObjectGroupPython] N_element300  label="N_element : 0.846"  # scripted group (container) (typed FeaturePython)
  n = 0.035451
FEATURE [App::DocumentObjectGroupPython] O_element588  label="O_element : 0.996"  # scripted group (container) (typed FeaturePython)
  n = 0.742522
FEATURE [App::DocumentObjectGroupPython] G4_MUSCLE_WITHOUT_SUCROSE  # scripted group (container) (typed FeaturePython)
  Dunit = g/cm3
  Dvalue = 1.07
  Group = -> [H_element612,C_element658,N_element300,O_element588]
  conduct = 2
  density = 1
  expand = 3
  formula = G4_MUSCLE_WITHOUT_SUCROSE
  name = G4_MUSCLE_WITHOUT_SUCROSE
  specific = 4
FEATURE [App::DocumentObjectGroupPython] C_element659  label="C_element : 427"  # scripted group (container) (typed FeaturePython)
  n = 10
  ref = C_element
FEATURE [App::DocumentObjectGroupPython] H_element613  label="H_element : 392"  # scripted group (container) (typed FeaturePython)
  n = 8
  ref = H_element
FEATURE [App::DocumentObjectGroupPython] G4_NAPHTHALENE  # scripted group (container) (typed FeaturePython)
  Dunit = g/cm3
  Dvalue = 1.145
  Group = -> [C_element659,H_element613]
  conduct = 2
  density = 1
  expand = 3
  formula = G4_NAPHTHALENE
  name = G4_NAPHTHALENE
  specific = 4
FEATURE [App::DocumentObjectGroupPython] C_element660  label="C_element : 428"  # scripted group (container) (typed FeaturePython)
  n = 6
  ref = C_element
FEATURE [App::DocumentObjectGroupPython] H_element614  label="H_element : 393"  # scripted group (container) (typed FeaturePython)
  n = 5
  ref = H_element
FEATURE [App::DocumentObjectGroupPython] N_element301  label="N_element : 163"  # scripted group (container) (typed FeaturePython)
  n = 1
  ref = N_element
FEATURE [App::DocumentObjectGroupPython] O_element589  label="O_element : 372"  # scripted group (container) (typed FeaturePython)
  n = 2
  ref = O_element
FEATURE [App::DocumentObjectGroupPython] G4_NITROBENZENE  # scripted group (container) (typed FeaturePython)
  Dunit = g/cm3
  Dvalue = 1.19867
  Group = -> [C_element660,H_element614,N_element301,O_element589]
  conduct = 2
  density = 1
  expand = 3
  formula = G4_NITROBENZENE
  name = G4_NITROBENZENE
  specific = 4
FEATURE [App::DocumentObjectGroupPython] N_element302  label="N_element : 164"  # scripted group (container) (typed FeaturePython)
  n = 2
  ref = N_element
FEATURE [App::DocumentObjectGroupPython] O_element590  label="O_element : 373"  # scripted group (container) (typed FeaturePython)
  n = 1
  ref = O_element
FEATURE [App::DocumentObjectGroupPython] G4_NITROUS_OXIDE  # scripted group (container) (typed FeaturePython)
  Dunit = g/cm3
  Dvalue = 0.00183094
  Group = -> [N_element302,O_element590]
  conduct = 2
  density = 1
  expand = 3
  formula = G4_NITROUS_OXIDE
  name = G4_NITROUS_OXIDE
  specific = 4
FEATURE [App::DocumentObjectGroupPython] H_element615  label="H_element : 0.272"  # scripted group (container) (typed FeaturePython)
  n = 0.103509
FEATURE [App::DocumentObjectGroupPython] C_element661  label="C_element : 0.1003"  # scripted group (container) (typed FeaturePython)
  n = 0.648416
FEATURE [App::DocumentObjectGroupPython] N_element303  label="N_element : 0.847"  # scripted group (container) (typed FeaturePython)
  n = 0.0995361
FEATURE [App::DocumentObjectGroupPython] O_element591  label="O_element : 0.997"  # scripted group (container) (typed FeaturePython)
  n = 0.148539
FEATURE [App::DocumentObjectGroupPython] G4_NYLON_8062  label="G4_NYLON-8062"  # scripted group (container) (typed FeaturePython)
  Dunit = g/cm3
  Dvalue = 1.08
  Group = -> [H_element615,C_element661,N_element303,O_element591]
  conduct = 2
  density = 1
  expand = 3
  formula = G4_NYLON-8062
  name = G4_NYLON-8062
  specific = 4
FEATURE [App::DocumentObjectGroupPython] C_element662  label="C_element : 429"  # scripted group (container) (typed FeaturePython)
  n = 6
  ref = C_element
FEATURE [App::DocumentObjectGroupPython] H_element616  label="H_element : 394"  # scripted group (container) (typed FeaturePython)
  n = 11
  ref = H_element
FEATURE [App::DocumentObjectGroupPython] N_element304  label="N_element : 165"  # scripted group (container) (typed FeaturePython)
  n = 1
  ref = N_element
FEATURE [App::DocumentObjectGroupPython] O_element592  label="O_element : 374"  # scripted group (container) (typed FeaturePython)
  n = 1
  ref = O_element
FEATURE [App::DocumentObjectGroupPython] G4_NYLON_6_6  label="G4_NYLON-6-6"  # scripted group (container) (typed FeaturePython)
  Dunit = g/cm3
  Dvalue = 1.14
  Group = -> [C_element662,H_element616,N_element304,O_element592]
  conduct = 2
  density = 1
  expand = 3
  formula = G4_NYLON-6-6
  name = G4_NYLON-6-6
  specific = 4
FEATURE [App::DocumentObjectGroupPython] H_element617  label="H_element : 0.273"  # scripted group (container) (typed FeaturePython)
  n = 0.107062
FEATURE [App::DocumentObjectGroupPython] C_element663  label="C_element : 0.1004"  # scripted group (container) (typed FeaturePython)
  n = 0.680449
FEATURE [App::DocumentObjectGroupPython] N_element305  label="N_element : 0.848"  # scripted group (container) (typed FeaturePython)
  n = 0.099189
FEATURE [App::DocumentObjectGroupPython] O_element593  label="O_element : 0.998"  # scripted group (container) (typed FeaturePython)
  n = 0.1133
FEATURE [App::DocumentObjectGroupPython] G4_NYLON_6_10  label="G4_NYLON-6-10"  # scripted group (container) (typed FeaturePython)
  Dunit = g/cm3
  Dvalue = 1.14
  Group = -> [H_element617,C_element663,N_element305,O_element593]
  conduct = 2
  density = 1
  expand = 3
  formula = G4_NYLON-6-10
  name = G4_NYLON-6-10
  specific = 4
FEATURE [App::DocumentObjectGroupPython] H_element618  label="H_element : 0.274"  # scripted group (container) (typed FeaturePython)
  n = 0.115476
FEATURE [App::DocumentObjectGroupPython] C_element664  label="C_element : 0.1005"  # scripted group (container) (typed FeaturePython)
  n = 0.720818
FEATURE [App::DocumentObjectGroupPython] N_element306  label="N_element : 0.849"  # scripted group (container) (typed FeaturePython)
  n = 0.0764169
FEATURE [App::DocumentObjectGroupPython] O_element594  label="O_element : 0.999"  # scripted group (container) (typed FeaturePython)
  n = 0.0872889
FEATURE [App::DocumentObjectGroupPython] G4_NYLON_11_RILSAN  label="G4_NYLON-11_RILSAN"  # scripted group (container) (typed FeaturePython)
  Dunit = g/cm3
  Dvalue = 1.425
  Group = -> [H_element618,C_element664,N_element306,O_element594]
  conduct = 2
  density = 1
  expand = 3
  formula = G4_NYLON-11_RILSAN
  name = G4_NYLON-11_RILSAN
  specific = 4
FEATURE [App::DocumentObjectGroupPython] C_element665  label="C_element : 430"  # scripted group (container) (typed FeaturePython)
  n = 8
  ref = C_element
FEATURE [App::DocumentObjectGroupPython] H_element619  label="H_element : 395"  # scripted group (container) (typed FeaturePython)
  n = 18
  ref = H_element
FEATURE [App::DocumentObjectGroupPython] G4_OCTANE  # scripted group (container) (typed FeaturePython)
  Dunit = g/cm3
  Dvalue = 0.7026
  Group = -> [C_element665,H_element619]
  conduct = 2
  density = 1
  expand = 3
  formula = G4_OCTANE
  name = G4_OCTANE
  specific = 4
FEATURE [App::DocumentObjectGroupPython] C_element666  label="C_element : 431"  # scripted group (container) (typed FeaturePython)
  n = 25
  ref = C_element
FEATURE [App::DocumentObjectGroupPython] H_element620  label="H_element : 396"  # scripted group (container) (typed FeaturePython)
  n = 52
  ref = H_element
FEATURE [App::DocumentObjectGroupPython] G4_PARAFFIN  # scripted group (container) (typed FeaturePython)
  Dunit = g/cm3
  Dvalue = 0.93
  Group = -> [C_element666,H_element620]
  conduct = 2
  density = 1
  expand = 3
  formula = G4_PARAFFIN
  name = G4_PARAFFIN
  specific = 4
FEATURE [App::DocumentObjectGroupPython] C_element667  label="C_element : 432"  # scripted group (container) (typed FeaturePython)
  n = 5
  ref = C_element
FEATURE [App::DocumentObjectGroupPython] H_element621  label="H_element : 397"  # scripted group (container) (typed FeaturePython)
  n = 12
  ref = H_element
FEATURE [App::DocumentObjectGroupPython] G4_N_PENTANE  label="G4_N-PENTANE"  # scripted group (container) (typed FeaturePython)
  Dunit = g/cm3
  Dvalue = 0.6262
  Group = -> [C_element667,H_element621]
  conduct = 2
  density = 1
  expand = 3
  formula = G4_N-PENTANE
  name = G4_N-PENTANE
  specific = 4
FEATURE [App::DocumentObjectGroupPython] H_element622  label="H_element : 0.275"  # scripted group (container) (typed FeaturePython)
  n = 0.0141
FEATURE [App::DocumentObjectGroupPython] C_element668  label="C_element : 0.1006"  # scripted group (container) (typed FeaturePython)
  n = 0.072261
FEATURE [App::DocumentObjectGroupPython] N_element307  label="N_element : 0.850"  # scripted group (container) (typed FeaturePython)
  n = 0.01932
FEATURE [App::DocumentObjectGroupPython] O_element595  label="O_element : 0.1000"  # scripted group (container) (typed FeaturePython)
  n = 0.066101
FEATURE [App::DocumentObjectGroupPython] S_element111  label="S_element : 0.077"  # scripted group (container) (typed FeaturePython)
  n = 0.00189
FEATURE [App::DocumentObjectGroupPython] Br_element032  label="Br_element : 0.770"  # scripted group (container) (typed FeaturePython)
  n = 0.349103
FEATURE [App::DocumentObjectGroupPython] Ag_element025  label="Ag_element : 0.579"  # scripted group (container) (typed FeaturePython)
  n = 0.474105
FEATURE [App::DocumentObjectGroupPython] I_element045  label="I_element : 0.658"  # scripted group (container) (typed FeaturePython)
  n = 0.00312
FEATURE [App::DocumentObjectGroupPython] G4_PHOTO_EMULSION  # scripted group (container) (typed FeaturePython)
  Dunit = g/cm3
  Dvalue = 3.815
  Group = -> [H_element622,C_element668,N_element307,O_element595,S_element111,Br_element032,Ag_element025,I_element045]
  conduct = 2
  density = 1
  expand = 3
  formula = G4_PHOTO_EMULSION
  name = G4_PHOTO_EMULSION
  specific = 4
FEATURE [App::DocumentObjectGroupPython] C_element669  label="C_element : 433"  # scripted group (container) (typed FeaturePython)
  n = 9
  ref = C_element
FEATURE [App::DocumentObjectGroupPython] H_element623  label="H_element : 398"  # scripted group (container) (typed FeaturePython)
  n = 10
  ref = H_element
FEATURE [App::DocumentObjectGroupPython] G4_PLASTIC_SC_VINYLTOLUENE  # scripted group (container) (typed FeaturePython)
  Dunit = g/cm3
  Dvalue = 1.032
  Group = -> [C_element669,H_element623]
  conduct = 2
  density = 1
  expand = 3
  formula = G4_PLASTIC_SC_VINYLTOLUENE
  name = G4_PLASTIC_SC_VINYLTOLUENE
  specific = 4
FEATURE [App::DocumentObjectGroupPython] Pu_element009  label="Pu_element : 008"  # scripted group (container) (typed FeaturePython)
  n = 1
  ref = Pu_element
FEATURE [App::DocumentObjectGroupPython] O_element596  label="O_element : 375"  # scripted group (container) (typed FeaturePython)
  n = 2
  ref = O_element
FEATURE [App::DocumentObjectGroupPython] G4_PLUTONIUM_DIOXIDE  # scripted group (container) (typed FeaturePython)
  Dunit = g/cm3
  Dvalue = 11.46
  Group = -> [Pu_element009,O_element596]
  conduct = 2
  density = 1
  expand = 3
  formula = G4_PLUTONIUM_DIOXIDE
  name = G4_PLUTONIUM_DIOXIDE
  specific = 4
FEATURE [App::DocumentObjectGroupPython] C_element670  label="C_element : 434"  # scripted group (container) (typed FeaturePython)
  n = 3
  ref = C_element
FEATURE [App::DocumentObjectGroupPython] H_element624  label="H_element : 399"  # scripted group (container) (typed FeaturePython)
  n = 3
  ref = H_element
FEATURE [App::DocumentObjectGroupPython] N_element308  label="N_element : 166"  # scripted group (container) (typed FeaturePython)
  n = 1
  ref = N_element
FEATURE [App::DocumentObjectGroupPython] G4_POLYACRYLONITRILE  # scripted group (container) (typed FeaturePython)
  Dunit = g/cm3
  Dvalue = 1.17
  Group = -> [C_element670,H_element624,N_element308]
  conduct = 2
  density = 1
  expand = 3
  formula = G4_POLYACRYLONITRILE
  name = G4_POLYACRYLONITRILE
  specific = 4
FEATURE [App::DocumentObjectGroupPython] C_element671  label="C_element : 435"  # scripted group (container) (typed FeaturePython)
  n = 16
  ref = C_element
FEATURE [App::DocumentObjectGroupPython] H_element625  label="H_element : 400"  # scripted group (container) (typed FeaturePython)
  n = 14
  ref = H_element
FEATURE [App::DocumentObjectGroupPython] O_element597  label="O_element : 376"  # scripted group (container) (typed FeaturePython)
  n = 3
  ref = O_element
FEATURE [App::DocumentObjectGroupPython] G4_POLYCARBONATE  # scripted group (container) (typed FeaturePython)
  Dunit = g/cm3
  Dvalue = 1.2
  Group = -> [C_element671,H_element625,O_element597]
  conduct = 2
  density = 1
  expand = 3
  formula = G4_POLYCARBONATE
  name = G4_POLYCARBONATE
  specific = 4
FEATURE [App::DocumentObjectGroupPython] C_element672  label="C_element : 436"  # scripted group (container) (typed FeaturePython)
  n = 8
  ref = C_element
FEATURE [App::DocumentObjectGroupPython] H_element626  label="H_element : 401"  # scripted group (container) (typed FeaturePython)
  n = 7
  ref = H_element
FEATURE [App::DocumentObjectGroupPython] Cl_element137  label="Cl_element : 067"  # scripted group (container) (typed FeaturePython)
  n = 1
  ref = Cl_element
FEATURE [App::DocumentObjectGroupPython] G4_POLYCHLOROSTYRENE  # scripted group (container) (typed FeaturePython)
  Dunit = g/cm3
  Dvalue = 1.3
  Group = -> [C_element672,H_element626,Cl_element137]
  conduct = 2
  density = 1
  expand = 3
  formula = G4_POLYCHLOROSTYRENE
  name = G4_POLYCHLOROSTYRENE
  specific = 4
FEATURE [App::DocumentObjectGroupPython] C_element673  label="C_element : 437"  # scripted group (container) (typed FeaturePython)
  n = 1
  ref = C_element
FEATURE [App::DocumentObjectGroupPython] H_element627  label="H_element : 402"  # scripted group (container) (typed FeaturePython)
  n = 2
  ref = H_element
FEATURE [App::DocumentObjectGroupPython] G4_POLYETHYLENE  # scripted group (container) (typed FeaturePython)
  Dunit = g/cm3
  Dvalue = 0.94
  Group = -> [C_element673,H_element627]
  conduct = 2
  density = 1
  expand = 3
  formula = G4_POLYETHYLENE
  name = G4_POLYETHYLENE
  specific = 4
FEATURE [App::DocumentObjectGroupPython] C_element674  label="C_element : 438"  # scripted group (container) (typed FeaturePython)
  n = 10
  ref = C_element
FEATURE [App::DocumentObjectGroupPython] H_element628  label="H_element : 403"  # scripted group (container) (typed FeaturePython)
  n = 8
  ref = H_element
FEATURE [App::DocumentObjectGroupPython] O_element598  label="O_element : 377"  # scripted group (container) (typed FeaturePython)
  n = 4
  ref = O_element
FEATURE [App::DocumentObjectGroupPython] G4_MYLAR  # scripted group (container) (typed FeaturePython)
  Dunit = g/cm3
  Dvalue = 1.4
  Group = -> [C_element674,H_element628,O_element598]
  conduct = 2
  density = 1
  expand = 3
  formula = G4_MYLAR
  name = G4_MYLAR
  specific = 4
FEATURE [App::DocumentObjectGroupPython] C_element675  label="C_element : 439"  # scripted group (container) (typed FeaturePython)
  n = 5
  ref = C_element
FEATURE [App::DocumentObjectGroupPython] H_element629  label="H_element : 404"  # scripted group (container) (typed FeaturePython)
  n = 8
  ref = H_element
FEATURE [App::DocumentObjectGroupPython] O_element599  label="O_element : 378"  # scripted group (container) (typed FeaturePython)
  n = 2
  ref = O_element
FEATURE [App::DocumentObjectGroupPython] G4_PLEXIGLASS  # scripted group (container) (typed FeaturePython)
  Dunit = g/cm3
  Dvalue = 1.19
  Group = -> [C_element675,H_element629,O_element599]
  conduct = 2
  density = 1
  expand = 3
  formula = G4_PLEXIGLASS
  name = G4_PLEXIGLASS
  specific = 4
FEATURE [App::DocumentObjectGroupPython] C_element676  label="C_element : 440"  # scripted group (container) (typed FeaturePython)
  n = 1
  ref = C_element
FEATURE [App::DocumentObjectGroupPython] H_element630  label="H_element : 405"  # scripted group (container) (typed FeaturePython)
  n = 2
  ref = H_element
FEATURE [App::DocumentObjectGroupPython] O_element600  label="O_element : 379"  # scripted group (container) (typed FeaturePython)
  n = 1
  ref = O_element
FEATURE [App::DocumentObjectGroupPython] G4_POLYOXYMETHYLENE  # scripted group (container) (typed FeaturePython)
  Dunit = g/cm3
  Dvalue = 1.425
  Group = -> [C_element676,H_element630,O_element600]
  conduct = 2
  density = 1
  expand = 3
  formula = G4_POLYOXYMETHYLENE
  name = G4_POLYOXYMETHYLENE
  specific = 4
FEATURE [App::DocumentObjectGroupPython] C_element677  label="C_element : 441"  # scripted group (container) (typed FeaturePython)
  n = 2
  ref = C_element
FEATURE [App::DocumentObjectGroupPython] H_element631  label="H_element : 406"  # scripted group (container) (typed FeaturePython)
  n = 4
  ref = H_element
FEATURE [App::DocumentObjectGroupPython] G4_POLYPROPYLENE  # scripted group (container) (typed FeaturePython)
  Dunit = g/cm3
  Dvalue = 0.9
  Group = -> [C_element677,H_element631]
  conduct = 2
  density = 1
  expand = 3
  formula = G4_POLYPROPYLENE
  name = G4_POLYPROPYLENE
  specific = 4
FEATURE [App::DocumentObjectGroupPython] C_element678  label="C_element : 442"  # scripted group (container) (typed FeaturePython)
  n = 8
  ref = C_element
FEATURE [App::DocumentObjectGroupPython] H_element632  label="H_element : 407"  # scripted group (container) (typed FeaturePython)
  n = 8
  ref = H_element
FEATURE [App::DocumentObjectGroupPython] G4_POLYSTYRENE  # scripted group (container) (typed FeaturePython)
  Dunit = g/cm3
  Dvalue = 1.06
  Group = -> [C_element678,H_element632]
  conduct = 2
  density = 1
  expand = 3
  formula = G4_POLYSTYRENE
  name = G4_POLYSTYRENE
  specific = 4
FEATURE [App::DocumentObjectGroupPython] C_element679  label="C_element : 443"  # scripted group (container) (typed FeaturePython)
  n = 2
  ref = C_element
FEATURE [App::DocumentObjectGroupPython] F_element090  label="F_element : 043"  # scripted group (container) (typed FeaturePython)
  n = 4
  ref = F_element
FEATURE [App::DocumentObjectGroupPython] G4_TEFLON  # scripted group (container) (typed FeaturePython)
  Dunit = g/cm3
  Dvalue = 2.2
  Group = -> [C_element679,F_element090]
  conduct = 2
  density = 1
  expand = 3
  formula = G4_TEFLON
  name = G4_TEFLON
  specific = 4
FEATURE [App::DocumentObjectGroupPython] C_element680  label="C_element : 444"  # scripted group (container) (typed FeaturePython)
  n = 2
  ref = C_element
FEATURE [App::DocumentObjectGroupPython] F_element091  label="F_element : 044"  # scripted group (container) (typed FeaturePython)
  n = 3
  ref = F_element
FEATURE [App::DocumentObjectGroupPython] Cl_element138  label="Cl_element : 068"  # scripted group (container) (typed FeaturePython)
  n = 1
  ref = Cl_element
FEATURE [App::DocumentObjectGroupPython] G4_POLYTRIFLUOROCHLOROETHYLENE  # scripted group (container) (typed FeaturePython)
  Dunit = g/cm3
  Dvalue = 2.1
  Group = -> [C_element680,F_element091,Cl_element138]
  conduct = 2
  density = 1
  expand = 3
  formula = G4_POLYTRIFLUOROCHLOROETHYLENE
  name = G4_POLYTRIFLUOROCHLOROETHYLENE
  specific = 4
FEATURE [App::DocumentObjectGroupPython] C_element681  label="C_element : 445"  # scripted group (container) (typed FeaturePython)
  n = 4
  ref = C_element
FEATURE [App::DocumentObjectGroupPython] H_element633  label="H_element : 408"  # scripted group (container) (typed FeaturePython)
  n = 6
  ref = H_element
FEATURE [App::DocumentObjectGroupPython] O_element601  label="O_element : 380"  # scripted group (container) (typed FeaturePython)
  n = 2
  ref = O_element
FEATURE [App::DocumentObjectGroupPython] G4_POLYVINYL_ACETATE  # scripted group (container) (typed FeaturePython)
  Dunit = g/cm3
  Dvalue = 1.19
  Group = -> [C_element681,H_element633,O_element601]
  conduct = 2
  density = 1
  expand = 3
  formula = G4_POLYVINYL_ACETATE
  name = G4_POLYVINYL_ACETATE
  specific = 4
FEATURE [App::DocumentObjectGroupPython] C_element682  label="C_element : 446"  # scripted group (container) (typed FeaturePython)
  n = 2
  ref = C_element
FEATURE [App::DocumentObjectGroupPython] H_element634  label="H_element : 409"  # scripted group (container) (typed FeaturePython)
  n = 4
  ref = H_element
FEATURE [App::DocumentObjectGroupPython] O_element602  label="O_element : 381"  # scripted group (container) (typed FeaturePython)
  n = 1
  ref = O_element
FEATURE [App::DocumentObjectGroupPython] G4_POLYVINYL_ALCOHOL  # scripted group (container) (typed FeaturePython)
  Dunit = g/cm3
  Dvalue = 1.3
  Group = -> [C_element682,H_element634,O_element602]
  conduct = 2
  density = 1
  expand = 3
  formula = G4_POLYVINYL_ALCOHOL
  name = G4_POLYVINYL_ALCOHOL
  specific = 4
FEATURE [App::DocumentObjectGroupPython] C_element683  label="C_element : 447"  # scripted group (container) (typed FeaturePython)
  n = 8
  ref = C_element
FEATURE [App::DocumentObjectGroupPython] H_element635  label="H_element : 410"  # scripted group (container) (typed FeaturePython)
  n = 14
  ref = H_element
FEATURE [App::DocumentObjectGroupPython] O_element603  label="O_element : 382"  # scripted group (container) (typed FeaturePython)
  n = 2
  ref = O_element
FEATURE [App::DocumentObjectGroupPython] G4_POLYVINYL_BUTYRAL  # scripted group (container) (typed FeaturePython)
  Dunit = g/cm3
  Dvalue = 1.12
  Group = -> [C_element683,H_element635,O_element603]
  conduct = 2
  density = 1
  expand = 3
  formula = G4_POLYVINYL_BUTYRAL
  name = G4_POLYVINYL_BUTYRAL
  specific = 4
FEATURE [App::DocumentObjectGroupPython] C_element684  label="C_element : 448"  # scripted group (container) (typed FeaturePython)
  n = 2
  ref = C_element
FEATURE [App::DocumentObjectGroupPython] H_element636  label="H_element : 411"  # scripted group (container) (typed FeaturePython)
  n = 3
  ref = H_element
FEATURE [App::DocumentObjectGroupPython] Cl_element139  label="Cl_element : 069"  # scripted group (container) (typed FeaturePython)
  n = 1
  ref = Cl_element
FEATURE [App::DocumentObjectGroupPython] G4_POLYVINYL_CHLORIDE  # scripted group (container) (typed FeaturePython)
  Dunit = g/cm3
  Dvalue = 1.3
  Group = -> [C_element684,H_element636,Cl_element139]
  conduct = 2
  density = 1
  expand = 3
  formula = G4_POLYVINYL_CHLORIDE
  name = G4_POLYVINYL_CHLORIDE
  specific = 4
FEATURE [App::DocumentObjectGroupPython] C_element685  label="C_element : 449"  # scripted group (container) (typed FeaturePython)
  n = 2
  ref = C_element
FEATURE [App::DocumentObjectGroupPython] H_element637  label="H_element : 412"  # scripted group (container) (typed FeaturePython)
  n = 2
  ref = H_element
FEATURE [App::DocumentObjectGroupPython] Cl_element140  label="Cl_element : 070"  # scripted group (container) (typed FeaturePython)
  n = 2
  ref = Cl_element
FEATURE [App::DocumentObjectGroupPython] G4_POLYVINYLIDENE_CHLORIDE  # scripted group (container) (typed FeaturePython)
  Dunit = g/cm3
  Dvalue = 1.7
  Group = -> [C_element685,H_element637,Cl_element140]
  conduct = 2
  density = 1
  expand = 3
  formula = G4_POLYVINYLIDENE_CHLORIDE
  name = G4_POLYVINYLIDENE_CHLORIDE
  specific = 4
FEATURE [App::DocumentObjectGroupPython] C_element686  label="C_element : 450"  # scripted group (container) (typed FeaturePython)
  n = 2
  ref = C_element
FEATURE [App::DocumentObjectGroupPython] H_element638  label="H_element : 413"  # scripted group (container) (typed FeaturePython)
  n = 2
  ref = H_element
FEATURE [App::DocumentObjectGroupPython] F_element092  label="F_element : 045"  # scripted group (container) (typed FeaturePython)
  n = 2
  ref = F_element
FEATURE [App::DocumentObjectGroupPython] G4_POLYVINYLIDENE_FLUORIDE  # scripted group (container) (typed FeaturePython)
  Dunit = g/cm3
  Dvalue = 1.76
  Group = -> [C_element686,H_element638,F_element092]
  conduct = 2
  density = 1
  expand = 3
  formula = G4_POLYVINYLIDENE_FLUORIDE
  name = G4_POLYVINYLIDENE_FLUORIDE
  specific = 4
FEATURE [App::DocumentObjectGroupPython] C_element687  label="C_element : 451"  # scripted group (container) (typed FeaturePython)
  n = 6
  ref = C_element
FEATURE [App::DocumentObjectGroupPython] H_element639  label="H_element : 414"  # scripted group (container) (typed FeaturePython)
  n = 9
  ref = H_element
FEATURE [App::DocumentObjectGroupPython] N_element309  label="N_element : 167"  # scripted group (container) (typed FeaturePython)
  n = 1
  ref = N_element
FEATURE [App::DocumentObjectGroupPython] O_element604  label="O_element : 383"  # scripted group (container) (typed FeaturePython)
  n = 1
  ref = O_element
FEATURE [App::DocumentObjectGroupPython] G4_POLYVINYL_PYRROLIDONE  # scripted group (container) (typed FeaturePython)
  Dunit = g/cm3
  Dvalue = 1.25
  Group = -> [C_element687,H_element639,N_element309,O_element604]
  conduct = 2
  density = 1
  expand = 3
  formula = G4_POLYVINYL_PYRROLIDONE
  name = G4_POLYVINYL_PYRROLIDONE
  specific = 4
FEATURE [App::DocumentObjectGroupPython] K_element060  label="K_element : 011"  # scripted group (container) (typed FeaturePython)
  n = 1
  ref = K_element
FEATURE [App::DocumentObjectGroupPython] I_element046  label="I_element : 029"  # scripted group (container) (typed FeaturePython)
  n = 1
  ref = I_element
FEATURE [App::DocumentObjectGroupPython] G4_POTASSIUM_IODIDE  # scripted group (container) (typed FeaturePython)
  Dunit = g/cm3
  Dvalue = 3.13
  Group = -> [K_element060,I_element046]
  conduct = 2
  density = 1
  expand = 3
  formula = G4_POTASSIUM_IODIDE
  name = G4_POTASSIUM_IODIDE
  specific = 4
FEATURE [App::DocumentObjectGroupPython] K_element061  label="K_element : 012"  # scripted group (container) (typed FeaturePython)
  n = 2
  ref = K_element
FEATURE [App::DocumentObjectGroupPython] O_element605  label="O_element : 384"  # scripted group (container) (typed FeaturePython)
  n = 1
  ref = O_element
FEATURE [App::DocumentObjectGroupPython] G4_POTASSIUM_OXIDE  # scripted group (container) (typed FeaturePython)
  Dunit = g/cm3
  Dvalue = 2.32
  Group = -> [K_element061,O_element605]
  conduct = 2
  density = 1
  expand = 3
  formula = G4_POTASSIUM_OXIDE
  name = G4_POTASSIUM_OXIDE
  specific = 4
FEATURE [App::DocumentObjectGroupPython] C_element688  label="C_element : 452"  # scripted group (container) (typed FeaturePython)
  n = 3
  ref = C_element
FEATURE [App::DocumentObjectGroupPython] H_element640  label="H_element : 415"  # scripted group (container) (typed FeaturePython)
  n = 8
  ref = H_element
FEATURE [App::DocumentObjectGroupPython] G4_PROPANE  # scripted group (container) (typed FeaturePython)
  Dunit = g/cm3
  Dvalue = 0.00187939
  Group = -> [C_element688,H_element640]
  conduct = 2
  density = 1
  expand = 3
  formula = G4_PROPANE
  name = G4_PROPANE
  specific = 4
FEATURE [App::DocumentObjectGroupPython] C_element689  label="C_element : 453"  # scripted group (container) (typed FeaturePython)
  n = 3
  ref = C_element
FEATURE [App::DocumentObjectGroupPython] H_element641  label="H_element : 416"  # scripted group (container) (typed FeaturePython)
  n = 8
  ref = H_element
FEATURE [App::DocumentObjectGroupPython] G4_lPROPANE  # scripted group (container) (typed FeaturePython)
  Dunit = g/cm3
  Dvalue = 0.43
  Group = -> [C_element689,H_element641]
  conduct = 2
  density = 1
  expand = 3
  formula = G4_lPROPANE
  name = G4_lPROPANE
  specific = 4
FEATURE [App::DocumentObjectGroupPython] C_element690  label="C_element : 454"  # scripted group (container) (typed FeaturePython)
  n = 3
  ref = C_element
FEATURE [App::DocumentObjectGroupPython] H_element642  label="H_element : 417"  # scripted group (container) (typed FeaturePython)
  n = 8
  ref = H_element
FEATURE [App::DocumentObjectGroupPython] O_element606  label="O_element : 385"  # scripted group (container) (typed FeaturePython)
  n = 1
  ref = O_element
FEATURE [App::DocumentObjectGroupPython] G4_N_PROPYL_ALCOHOL  label="G4_N-PROPYL_ALCOHOL"  # scripted group (container) (typed FeaturePython)
  Dunit = g/cm3
  Dvalue = 0.8035
  Group = -> [C_element690,H_element642,O_element606]
  conduct = 2
  density = 1
  expand = 3
  formula = G4_N-PROPYL_ALCOHOL
  name = G4_N-PROPYL_ALCOHOL
  specific = 4
FEATURE [App::DocumentObjectGroupPython] C_element691  label="C_element : 455"  # scripted group (container) (typed FeaturePython)
  n = 5
  ref = C_element
FEATURE [App::DocumentObjectGroupPython] H_element643  label="H_element : 418"  # scripted group (container) (typed FeaturePython)
  n = 5
  ref = H_element
FEATURE [App::DocumentObjectGroupPython] N_element310  label="N_element : 168"  # scripted group (container) (typed FeaturePython)
  n = 1
  ref = N_element
FEATURE [App::DocumentObjectGroupPython] G4_PYRIDINE  # scripted group (container) (typed FeaturePython)
  Dunit = g/cm3
  Dvalue = 0.9819
  Group = -> [C_element691,H_element643,N_element310]
  conduct = 2
  density = 1
  expand = 3
  formula = G4_PYRIDINE
  name = G4_PYRIDINE
  specific = 4
FEATURE [App::DocumentObjectGroupPython] H_element644  label="H_element : 0.276"  # scripted group (container) (typed FeaturePython)
  n = 0.143711
FEATURE [App::DocumentObjectGroupPython] C_element692  label="C_element : 0.1007"  # scripted group (container) (typed FeaturePython)
  n = 0.856289
FEATURE [App::DocumentObjectGroupPython] G4_RUBBER_BUTYL  # scripted group (container) (typed FeaturePython)
  Dunit = g/cm3
  Dvalue = 0.92
  Group = -> [H_element644,C_element692]
  conduct = 2
  density = 1
  expand = 3
  formula = G4_RUBBER_BUTYL
  name = G4_RUBBER_BUTYL
  specific = 4
FEATURE [App::DocumentObjectGroupPython] H_element645  label="H_element : 0.277"  # scripted group (container) (typed FeaturePython)
  n = 0.118371
FEATURE [App::DocumentObjectGroupPython] C_element693  label="C_element : 0.1008"  # scripted group (container) (typed FeaturePython)
  n = 0.881629
FEATURE [App::DocumentObjectGroupPython] G4_RUBBER_NATURAL  # scripted group (container) (typed FeaturePython)
  Dunit = g/cm3
  Dvalue = 0.92
  Group = -> [H_element645,C_element693]
  conduct = 2
  density = 1
  expand = 3
  formula = G4_RUBBER_NATURAL
  name = G4_RUBBER_NATURAL
  specific = 4
FEATURE [App::DocumentObjectGroupPython] H_element646  label="H_element : 0.278"  # scripted group (container) (typed FeaturePython)
  n = 0.05692
FEATURE [App::DocumentObjectGroupPython] C_element694  label="C_element : 0.1009"  # scripted group (container) (typed FeaturePython)
  n = 0.542646
FEATURE [App::DocumentObjectGroupPython] Cl_element141  label="Cl_element : 0.637"  # scripted group (container) (typed FeaturePython)
  n = 0.400434
FEATURE [App::DocumentObjectGroupPython] G4_RUBBER_NEOPRENE  # scripted group (container) (typed FeaturePython)
  Dunit = g/cm3
  Dvalue = 1.23
  Group = -> [H_element646,C_element694,Cl_element141]
  conduct = 2
  density = 1
  expand = 3
  formula = G4_RUBBER_NEOPRENE
  name = G4_RUBBER_NEOPRENE
  specific = 4
FEATURE [App::DocumentObjectGroupPython] Si_element034  label="Si_element : 008"  # scripted group (container) (typed FeaturePython)
  n = 1
  ref = Si_element
FEATURE [App::DocumentObjectGroupPython] O_element607  label="O_element : 386"  # scripted group (container) (typed FeaturePython)
  n = 2
  ref = O_element
FEATURE [App::DocumentObjectGroupPython] G4_SILICON_DIOXIDE  # scripted group (container) (typed FeaturePython)
  Dunit = g/cm3
  Dvalue = 2.32
  Group = -> [Si_element034,O_element607]
  conduct = 2
  density = 1
  expand = 3
  formula = G4_SILICON_DIOXIDE
  name = G4_SILICON_DIOXIDE
  specific = 4
FEATURE [App::DocumentObjectGroupPython] Ag_element026  label="Ag_element : 016"  # scripted group (container) (typed FeaturePython)
  n = 1
  ref = Ag_element
FEATURE [App::DocumentObjectGroupPython] Br_element033  label="Br_element : 018"  # scripted group (container) (typed FeaturePython)
  n = 1
  ref = Br_element
FEATURE [App::DocumentObjectGroupPython] G4_SILVER_BROMIDE  # scripted group (container) (typed FeaturePython)
  Dunit = g/cm3
  Dvalue = 6.473
  Group = -> [Ag_element026,Br_element033]
  conduct = 2
  density = 1
  expand = 3
  formula = G4_SILVER_BROMIDE
  name = G4_SILVER_BROMIDE
  specific = 4
FEATURE [App::DocumentObjectGroupPython] Ag_element027  label="Ag_element : 017"  # scripted group (container) (typed FeaturePython)
  n = 1
  ref = Ag_element
FEATURE [App::DocumentObjectGroupPython] Cl_element142  label="Cl_element : 071"  # scripted group (container) (typed FeaturePython)
  n = 1
  ref = Cl_element
FEATURE [App::DocumentObjectGroupPython] G4_SILVER_CHLORIDE  # scripted group (container) (typed FeaturePython)
  Dunit = g/cm3
  Dvalue = 5.56
  Group = -> [Ag_element027,Cl_element142]
  conduct = 2
  density = 1
  expand = 3
  formula = G4_SILVER_CHLORIDE
  name = G4_SILVER_CHLORIDE
  specific = 4
FEATURE [App::DocumentObjectGroupPython] Br_element034  label="Br_element : 0.771"  # scripted group (container) (typed FeaturePython)
  n = 0.422895
FEATURE [App::DocumentObjectGroupPython] Ag_element028  label="Ag_element : 0.580"  # scripted group (container) (typed FeaturePython)
  n = 0.573748
FEATURE [App::DocumentObjectGroupPython] I_element047  label="I_element : 0.659"  # scripted group (container) (typed FeaturePython)
  n = 0.003357
FEATURE [App::DocumentObjectGroupPython] G4_SILVER_HALIDES  # scripted group (container) (typed FeaturePython)
  Dunit = g/cm3
  Dvalue = 6.47
  Group = -> [Br_element034,Ag_element028,I_element047]
  conduct = 2
  density = 1
  expand = 3
  formula = G4_SILVER_HALIDES
  name = G4_SILVER_HALIDES
  specific = 4
FEATURE [App::DocumentObjectGroupPython] Ag_element029  label="Ag_element : 018"  # scripted group (container) (typed FeaturePython)
  n = 1
  ref = Ag_element
FEATURE [App::DocumentObjectGroupPython] I_element048  label="I_element : 030"  # scripted group (container) (typed FeaturePython)
  n = 1
  ref = I_element
FEATURE [App::DocumentObjectGroupPython] G4_SILVER_IODIDE  # scripted group (container) (typed FeaturePython)
  Dunit = g/cm3
  Dvalue = 6.01
  Group = -> [Ag_element029,I_element048]
  conduct = 2
  density = 1
  expand = 3
  formula = G4_SILVER_IODIDE
  name = G4_SILVER_IODIDE
  specific = 4
FEATURE [App::DocumentObjectGroupPython] H_element647  label="H_element : 0.279"  # scripted group (container) (typed FeaturePython)
  n = 0.1
FEATURE [App::DocumentObjectGroupPython] C_element695  label="C_element : 0.1010"  # scripted group (container) (typed FeaturePython)
  n = 0.204
FEATURE [App::DocumentObjectGroupPython] N_element311  label="N_element : 0.851"  # scripted group (container) (typed FeaturePython)
  n = 0.042
FEATURE [App::DocumentObjectGroupPython] O_element608  label="O_element : 0.1001"  # scripted group (container) (typed FeaturePython)
  n = 0.645
FEATURE [App::DocumentObjectGroupPython] Na_element093  label="Na_element : 0.154"  # scripted group (container) (typed FeaturePython)
  n = 0.002
FEATURE [App::DocumentObjectGroupPython] P_element085  label="P_element : 0.146"  # scripted group (container) (typed FeaturePython)
  n = 0.001
FEATURE [App::DocumentObjectGroupPython] S_element112  label="S_element : 0.078"  # scripted group (container) (typed FeaturePython)
  n = 0.002
FEATURE [App::DocumentObjectGroupPython] Cl_element143  label="Cl_element : 0.638"  # scripted group (container) (typed FeaturePython)
  n = 0.003
FEATURE [App::DocumentObjectGroupPython] K_element062  label="K_element : 0.051"  # scripted group (container) (typed FeaturePython)
  n = 0.001
FEATURE [App::DocumentObjectGroupPython] G4_SKIN_ICRP  # scripted group (container) (typed FeaturePython)
  Dunit = g/cm3
  Dvalue = 1.09
  Group = -> [H_element647,C_element695,N_element311,O_element608,Na_element093,P_element085,S_element112,Cl_element143,K_element062]
  conduct = 2
  density = 1
  expand = 3
  formula = G4_SKIN_ICRP
  name = G4_SKIN_ICRP
  specific = 4
FEATURE [App::DocumentObjectGroupPython] Na_element094  label="Na_element : 019"  # scripted group (container) (typed FeaturePython)
  n = 2
  ref = Na_element
FEATURE [App::DocumentObjectGroupPython] C_element696  label="C_element : 456"  # scripted group (container) (typed FeaturePython)
  n = 1
  ref = C_element
FEATURE [App::DocumentObjectGroupPython] O_element609  label="O_element : 387"  # scripted group (container) (typed FeaturePython)
  n = 3
  ref = O_element
FEATURE [App::DocumentObjectGroupPython] G4_SODIUM_CARBONATE  # scripted group (container) (typed FeaturePython)
  Dunit = g/cm3
  Dvalue = 2.532
  Group = -> [Na_element094,C_element696,O_element609]
  conduct = 2
  density = 1
  expand = 3
  formula = G4_SODIUM_CARBONATE
  name = G4_SODIUM_CARBONATE
  specific = 4
FEATURE [App::DocumentObjectGroupPython] Na_element095  label="Na_element : 020"  # scripted group (container) (typed FeaturePython)
  n = 1
  ref = Na_element
FEATURE [App::DocumentObjectGroupPython] I_element049  label="I_element : 031"  # scripted group (container) (typed FeaturePython)
  n = 1
  ref = I_element
FEATURE [App::DocumentObjectGroupPython] G4_SODIUM_IODIDE  # scripted group (container) (typed FeaturePython)
  Dunit = g/cm3
  Dvalue = 3.667
  Group = -> [Na_element095,I_element049]
  conduct = 2
  density = 1
  expand = 3
  formula = G4_SODIUM_IODIDE
  name = G4_SODIUM_IODIDE
  specific = 4
FEATURE [App::DocumentObjectGroupPython] Na_element096  label="Na_element : 021"  # scripted group (container) (typed FeaturePython)
  n = 2
  ref = Na_element
FEATURE [App::DocumentObjectGroupPython] O_element610  label="O_element : 388"  # scripted group (container) (typed FeaturePython)
  n = 1
  ref = O_element
FEATURE [App::DocumentObjectGroupPython] G4_SODIUM_MONOXIDE  # scripted group (container) (typed FeaturePython)
  Dunit = g/cm3
  Dvalue = 2.27
  Group = -> [Na_element096,O_element610]
  conduct = 2
  density = 1
  expand = 3
  formula = G4_SODIUM_MONOXIDE
  name = G4_SODIUM_MONOXIDE
  specific = 4
FEATURE [App::DocumentObjectGroupPython] Na_element097  label="Na_element : 022"  # scripted group (container) (typed FeaturePython)
  n = 1
  ref = Na_element
FEATURE [App::DocumentObjectGroupPython] N_element312  label="N_element : 169"  # scripted group (container) (typed FeaturePython)
  n = 1
  ref = N_element
FEATURE [App::DocumentObjectGroupPython] O_element611  label="O_element : 389"  # scripted group (container) (typed FeaturePython)
  n = 3
  ref = O_element
FEATURE [App::DocumentObjectGroupPython] G4_SODIUM_NITRATE  # scripted group (container) (typed FeaturePython)
  Dunit = g/cm3
  Dvalue = 2.261
  Group = -> [Na_element097,N_element312,O_element611]
  conduct = 2
  density = 1
  expand = 3
  formula = G4_SODIUM_NITRATE
  name = G4_SODIUM_NITRATE
  specific = 4
FEATURE [App::DocumentObjectGroupPython] C_element697  label="C_element : 457"  # scripted group (container) (typed FeaturePython)
  n = 14
  ref = C_element
FEATURE [App::DocumentObjectGroupPython] H_element648  label="H_element : 419"  # scripted group (container) (typed FeaturePython)
  n = 12
  ref = H_element
FEATURE [App::DocumentObjectGroupPython] G4_STILBENE  # scripted group (container) (typed FeaturePython)
  Dunit = g/cm3
  Dvalue = 0.9707
  Group = -> [C_element697,H_element648]
  conduct = 2
  density = 1
  expand = 3
  formula = G4_STILBENE
  name = G4_STILBENE
  specific = 4
FEATURE [App::DocumentObjectGroupPython] C_element698  label="C_element : 458"  # scripted group (container) (typed FeaturePython)
  n = 12
  ref = C_element
FEATURE [App::DocumentObjectGroupPython] H_element649  label="H_element : 420"  # scripted group (container) (typed FeaturePython)
  n = 22
  ref = H_element
FEATURE [App::DocumentObjectGroupPython] O_element612  label="O_element : 390"  # scripted group (container) (typed FeaturePython)
  n = 11
  ref = O_element
FEATURE [App::DocumentObjectGroupPython] G4_SUCROSE  # scripted group (container) (typed FeaturePython)
  Dunit = g/cm3
  Dvalue = 1.5805
  Group = -> [C_element698,H_element649,O_element612]
  conduct = 2
  density = 1
  expand = 3
  formula = G4_SUCROSE
  name = G4_SUCROSE
  specific = 4
FEATURE [App::DocumentObjectGroupPython] C_element699  label="C_element : 459"  # scripted group (container) (typed FeaturePython)
  n = 18
  ref = C_element
FEATURE [App::DocumentObjectGroupPython] H_element650  label="H_element : 421"  # scripted group (container) (typed FeaturePython)
  n = 14
  ref = H_element
FEATURE [App::DocumentObjectGroupPython] G4_TERPHENYL  # scripted group (container) (typed FeaturePython)
  Dunit = g/cm3
  Dvalue = 1.24
  Group = -> [C_element699,H_element650]
  conduct = 2
  density = 1
  expand = 3
  formula = G4_TERPHENYL
  name = G4_TERPHENYL
  specific = 4
FEATURE [App::DocumentObjectGroupPython] H_element651  label="H_element : 0.280"  # scripted group (container) (typed FeaturePython)
  n = 0.106
FEATURE [App::DocumentObjectGroupPython] C_element700  label="C_element : 0.1011"  # scripted group (container) (typed FeaturePython)
  n = 0.099
FEATURE [App::DocumentObjectGroupPython] N_element313  label="N_element : 0.852"  # scripted group (container) (typed FeaturePython)
  n = 0.02
FEATURE [App::DocumentObjectGroupPython] O_element613  label="O_element : 0.1002"  # scripted group (container) (typed FeaturePython)
  n = 0.766
FEATURE [App::DocumentObjectGroupPython] Na_element098  label="Na_element : 0.155"  # scripted group (container) (typed FeaturePython)
  n = 0.002
FEATURE [App::DocumentObjectGroupPython] P_element086  label="P_element : 0.147"  # scripted group (container) (typed FeaturePython)
  n = 0.001
FEATURE [App::DocumentObjectGroupPython] S_element113  label="S_element : 0.079"  # scripted group (container) (typed FeaturePython)
  n = 0.002
FEATURE [App::DocumentObjectGroupPython] Cl_element144  label="Cl_element : 0.639"  # scripted group (container) (typed FeaturePython)
  n = 0.002
FEATURE [App::DocumentObjectGroupPython] K_element063  label="K_element : 0.052"  # scripted group (container) (typed FeaturePython)
  n = 0.002
FEATURE [App::DocumentObjectGroupPython] G4_TESTIS_ICRP  # scripted group (container) (typed FeaturePython)
  Dunit = g/cm3
  Dvalue = 1.04
  Group = -> [H_element651,C_element700,N_element313,O_element613,Na_element098,P_element086,S_element113,Cl_element144,K_element063]
  conduct = 2
  density = 1
  expand = 3
  formula = G4_TESTIS_ICRP
  name = G4_TESTIS_ICRP
  specific = 4
FEATURE [App::DocumentObjectGroupPython] C_element701  label="C_element : 460"  # scripted group (container) (typed FeaturePython)
  n = 2
  ref = C_element
FEATURE [App::DocumentObjectGroupPython] Cl_element145  label="Cl_element : 072"  # scripted group (container) (typed FeaturePython)
  n = 4
  ref = Cl_element
FEATURE [App::DocumentObjectGroupPython] G4_TETRACHLOROETHYLENE  # scripted group (container) (typed FeaturePython)
  Dunit = g/cm3
  Dvalue = 1.625
  Group = -> [C_element701,Cl_element145]
  conduct = 2
  density = 1
  expand = 3
  formula = G4_TETRACHLOROETHYLENE
  name = G4_TETRACHLOROETHYLENE
  specific = 4
FEATURE [App::DocumentObjectGroupPython] Tl_element009  label="Tl_element : 008"  # scripted group (container) (typed FeaturePython)
  n = 1
  ref = Tl_element
FEATURE [App::DocumentObjectGroupPython] Cl_element146  label="Cl_element : 073"  # scripted group (container) (typed FeaturePython)
  n = 1
  ref = Cl_element
FEATURE [App::DocumentObjectGroupPython] G4_THALLIUM_CHLORIDE  # scripted group (container) (typed FeaturePython)
  Dunit = g/cm3
  Dvalue = 7.004
  Group = -> [Tl_element009,Cl_element146]
  conduct = 2
  density = 1
  expand = 3
  formula = G4_THALLIUM_CHLORIDE
  name = G4_THALLIUM_CHLORIDE
  specific = 4
FEATURE [App::DocumentObjectGroupPython] H_element652  label="H_element : 0.281"  # scripted group (container) (typed FeaturePython)
  n = 0.105
FEATURE [App::DocumentObjectGroupPython] C_element702  label="C_element : 0.1012"  # scripted group (container) (typed FeaturePython)
  n = 0.256
FEATURE [App::DocumentObjectGroupPython] N_element314  label="N_element : 0.853"  # scripted group (container) (typed FeaturePython)
  n = 0.027
FEATURE [App::DocumentObjectGroupPython] O_element614  label="O_element : 0.1003"  # scripted group (container) (typed FeaturePython)
  n = 0.602
FEATURE [App::DocumentObjectGroupPython] Na_element099  label="Na_element : 0.156"  # scripted group (container) (typed FeaturePython)
  n = 0.001
FEATURE [App::DocumentObjectGroupPython] P_element087  label="P_element : 0.148"  # scripted group (container) (typed FeaturePython)
  n = 0.002
FEATURE [App::DocumentObjectGroupPython] S_element114  label="S_element : 0.080"  # scripted group (container) (typed FeaturePython)
  n = 0.003
FEATURE [App::DocumentObjectGroupPython] Cl_element147  label="Cl_element : 0.640"  # scripted group (container) (typed FeaturePython)
  n = 0.002
FEATURE [App::DocumentObjectGroupPython] K_element064  label="K_element : 0.053"  # scripted group (container) (typed FeaturePython)
  n = 0.002
FEATURE [App::DocumentObjectGroupPython] G4_TISSUE_SOFT_ICRP  # scripted group (container) (typed FeaturePython)
  Dunit = g/cm3
  Dvalue = 1.03
  Group = -> [H_element652,C_element702,N_element314,O_element614,Na_element099,P_element087,S_element114,Cl_element147,K_element064]
  conduct = 2
  density = 1
  expand = 3
  formula = G4_TISSUE_SOFT_ICRP
  name = G4_TISSUE_SOFT_ICRP
  specific = 4
FEATURE [App::DocumentObjectGroupPython] H_element653  label="H_element : 0.282"  # scripted group (container) (typed FeaturePython)
  n = 0.101
FEATURE [App::DocumentObjectGroupPython] C_element703  label="C_element : 0.1013"  # scripted group (container) (typed FeaturePython)
  n = 0.111
FEATURE [App::DocumentObjectGroupPython] N_element315  label="N_element : 0.854"  # scripted group (container) (typed FeaturePython)
  n = 0.026
FEATURE [App::DocumentObjectGroupPython] O_element615  label="O_element : 0.1004"  # scripted group (container) (typed FeaturePython)
  n = 0.762
FEATURE [App::DocumentObjectGroupPython] G4_TISSUE_SOFT_ICRU_4  label="G4_TISSUE_SOFT_ICRU-4"  # scripted group (container) (typed FeaturePython)
  Dunit = g/cm3
  Dvalue = 1
  Group = -> [H_element653,C_element703,N_element315,O_element615]
  conduct = 2
  density = 1
  expand = 3
  formula = G4_TISSUE_SOFT_ICRU-4
  name = G4_TISSUE_SOFT_ICRU-4
  specific = 4
FEATURE [App::DocumentObjectGroupPython] H_element654  label="H_element : 0.283"  # scripted group (container) (typed FeaturePython)
  n = 0.101869
FEATURE [App::DocumentObjectGroupPython] C_element704  label="C_element : 0.1014"  # scripted group (container) (typed FeaturePython)
  n = 0.456179
FEATURE [App::DocumentObjectGroupPython] N_element316  label="N_element : 0.855"  # scripted group (container) (typed FeaturePython)
  n = 0.035172
FEATURE [App::DocumentObjectGroupPython] O_element616  label="O_element : 0.1005"  # scripted group (container) (typed FeaturePython)
  n = 0.40678
FEATURE [App::DocumentObjectGroupPython] G4_TISSUE_METHANE  label="G4_TISSUE-METHANE"  # scripted group (container) (typed FeaturePython)
  Dunit = g/cm3
  Dvalue = 0.00106409
  Group = -> [H_element654,C_element704,N_element316,O_element616]
  conduct = 2
  density = 1
  expand = 3
  formula = G4_TISSUE-METHANE
  name = G4_TISSUE-METHANE
  specific = 4
FEATURE [App::DocumentObjectGroupPython] H_element655  label="H_element : 0.284"  # scripted group (container) (typed FeaturePython)
  n = 0.102672
FEATURE [App::DocumentObjectGroupPython] C_element705  label="C_element : 0.1015"  # scripted group (container) (typed FeaturePython)
  n = 0.56894
FEATURE [App::DocumentObjectGroupPython] N_element317  label="N_element : 0.856"  # scripted group (container) (typed FeaturePython)
  n = 0.035022
FEATURE [App::DocumentObjectGroupPython] O_element617  label="O_element : 0.1006"  # scripted group (container) (typed FeaturePython)
  n = 0.293366
FEATURE [App::DocumentObjectGroupPython] G4_TISSUE_PROPANE  label="G4_TISSUE-PROPANE"  # scripted group (container) (typed FeaturePython)
  Dunit = g/cm3
  Dvalue = 0.00182628
  Group = -> [H_element655,C_element705,N_element317,O_element617]
  conduct = 2
  density = 1
  expand = 3
  formula = G4_TISSUE-PROPANE
  name = G4_TISSUE-PROPANE
  specific = 4
FEATURE [App::DocumentObjectGroupPython] Ti_element019  label="Ti_element : 008"  # scripted group (container) (typed FeaturePython)
  n = 1
  ref = Ti_element
FEATURE [App::DocumentObjectGroupPython] O_element618  label="O_element : 391"  # scripted group (container) (typed FeaturePython)
  n = 2
  ref = O_element
FEATURE [App::DocumentObjectGroupPython] G4_TITANIUM_DIOXIDE  # scripted group (container) (typed FeaturePython)
  Dunit = g/cm3
  Dvalue = 4.26
  Group = -> [Ti_element019,O_element618]
  conduct = 2
  density = 1
  expand = 3
  formula = G4_TITANIUM_DIOXIDE
  name = G4_TITANIUM_DIOXIDE
  specific = 4
FEATURE [App::DocumentObjectGroupPython] C_element706  label="C_element : 461"  # scripted group (container) (typed FeaturePython)
  n = 7
  ref = C_element
FEATURE [App::DocumentObjectGroupPython] H_element656  label="H_element : 422"  # scripted group (container) (typed FeaturePython)
  n = 8
  ref = H_element
FEATURE [App::DocumentObjectGroupPython] G4_TOLUENE  # scripted group (container) (typed FeaturePython)
  Dunit = g/cm3
  Dvalue = 0.8669
  Group = -> [C_element706,H_element656]
  conduct = 2
  density = 1
  expand = 3
  formula = G4_TOLUENE
  name = G4_TOLUENE
  specific = 4
FEATURE [App::DocumentObjectGroupPython] C_element707  label="C_element : 462"  # scripted group (container) (typed FeaturePython)
  n = 2
  ref = C_element
FEATURE [App::DocumentObjectGroupPython] H_element657  label="H_element : 423"  # scripted group (container) (typed FeaturePython)
  n = 1
  ref = H_element
FEATURE [App::DocumentObjectGroupPython] Cl_element148  label="Cl_element : 074"  # scripted group (container) (typed FeaturePython)
  n = 3
  ref = Cl_element
FEATURE [App::DocumentObjectGroupPython] G4_TRICHLOROETHYLENE  # scripted group (container) (typed FeaturePython)
  Dunit = g/cm3
  Dvalue = 1.46
  Group = -> [C_element707,H_element657,Cl_element148]
  conduct = 2
  density = 1
  expand = 3
  formula = G4_TRICHLOROETHYLENE
  name = G4_TRICHLOROETHYLENE
  specific = 4
FEATURE [App::DocumentObjectGroupPython] C_element708  label="C_element : 463"  # scripted group (container) (typed FeaturePython)
  n = 6
  ref = C_element
FEATURE [App::DocumentObjectGroupPython] H_element658  label="H_element : 424"  # scripted group (container) (typed FeaturePython)
  n = 15
  ref = H_element
FEATURE [App::DocumentObjectGroupPython] O_element619  label="O_element : 392"  # scripted group (container) (typed FeaturePython)
  n = 4
  ref = O_element
FEATURE [App::DocumentObjectGroupPython] P_element088  label="P_element : 032"  # scripted group (container) (typed FeaturePython)
  n = 1
  ref = P_element
FEATURE [App::DocumentObjectGroupPython] G4_TRIETHYL_PHOSPHATE  # scripted group (container) (typed FeaturePython)
  Dunit = g/cm3
  Dvalue = 1.07
  Group = -> [C_element708,H_element658,O_element619,P_element088]
  conduct = 2
  density = 1
  expand = 3
  formula = G4_TRIETHYL_PHOSPHATE
  name = G4_TRIETHYL_PHOSPHATE
  specific = 4
FEATURE [App::DocumentObjectGroupPython] W_element023  label="W_element : 022"  # scripted group (container) (typed FeaturePython)
  n = 1
  ref = W_element
FEATURE [App::DocumentObjectGroupPython] F_element093  label="F_element : 046"  # scripted group (container) (typed FeaturePython)
  n = 6
  ref = F_element
FEATURE [App::DocumentObjectGroupPython] G4_TUNGSTEN_HEXAFLUORIDE  # scripted group (container) (typed FeaturePython)
  Dunit = g/cm3
  Dvalue = 2.4
  Group = -> [W_element023,F_element093]
  conduct = 2
  density = 1
  expand = 3
  formula = G4_TUNGSTEN_HEXAFLUORIDE
  name = G4_TUNGSTEN_HEXAFLUORIDE
  specific = 4
FEATURE [App::DocumentObjectGroupPython] U_element017  label="U_element : 016"  # scripted group (container) (typed FeaturePython)
  n = 1
  ref = U_element
FEATURE [App::DocumentObjectGroupPython] C_element709  label="C_element : 464"  # scripted group (container) (typed FeaturePython)
  n = 2
  ref = C_element
FEATURE [App::DocumentObjectGroupPython] G4_URANIUM_DICARBIDE  # scripted group (container) (typed FeaturePython)
  Dunit = g/cm3
  Dvalue = 11.28
  Group = -> [U_element017,C_element709]
  conduct = 2
  density = 1
  expand = 3
  formula = G4_URANIUM_DICARBIDE
  name = G4_URANIUM_DICARBIDE
  specific = 4
FEATURE [App::DocumentObjectGroupPython] U_element018  label="U_element : 017"  # scripted group (container) (typed FeaturePython)
  n = 1
  ref = U_element
FEATURE [App::DocumentObjectGroupPython] C_element710  label="C_element : 465"  # scripted group (container) (typed FeaturePython)
  n = 1
  ref = C_element
FEATURE [App::DocumentObjectGroupPython] G4_URANIUM_MONOCARBIDE  # scripted group (container) (typed FeaturePython)
  Dunit = g/cm3
  Dvalue = 13.63
  Group = -> [U_element018,C_element710]
  conduct = 2
  density = 1
  expand = 3
  formula = G4_URANIUM_MONOCARBIDE
  name = G4_URANIUM_MONOCARBIDE
  specific = 4
FEATURE [App::DocumentObjectGroupPython] U_element019  label="U_element : 018"  # scripted group (container) (typed FeaturePython)
  n = 1
  ref = U_element
FEATURE [App::DocumentObjectGroupPython] O_element620  label="O_element : 393"  # scripted group (container) (typed FeaturePython)
  n = 2
  ref = O_element
FEATURE [App::DocumentObjectGroupPython] G4_URANIUM_OXIDE  # scripted group (container) (typed FeaturePython)
  Dunit = g/cm3
  Dvalue = 10.96
  Group = -> [U_element019,O_element620]
  conduct = 2
  density = 1
  expand = 3
  formula = G4_URANIUM_OXIDE
  name = G4_URANIUM_OXIDE
  specific = 4
FEATURE [App::DocumentObjectGroupPython] C_element711  label="C_element : 466"  # scripted group (container) (typed FeaturePython)
  n = 1
  ref = C_element
FEATURE [App::DocumentObjectGroupPython] H_element659  label="H_element : 425"  # scripted group (container) (typed FeaturePython)
  n = 4
  ref = H_element
FEATURE [App::DocumentObjectGroupPython] N_element318  label="N_element : 170"  # scripted group (container) (typed FeaturePython)
  n = 2
  ref = N_element
FEATURE [App::DocumentObjectGroupPython] O_element621  label="O_element : 394"  # scripted group (container) (typed FeaturePython)
  n = 1
  ref = O_element
FEATURE [App::DocumentObjectGroupPython] G4_UREA  # scripted group (container) (typed FeaturePython)
  Dunit = g/cm3
  Dvalue = 1.323
  Group = -> [C_element711,H_element659,N_element318,O_element621]
  conduct = 2
  density = 1
  expand = 3
  formula = G4_UREA
  name = G4_UREA
  specific = 4
FEATURE [App::DocumentObjectGroupPython] C_element712  label="C_element : 467"  # scripted group (container) (typed FeaturePython)
  n = 5
  ref = C_element
FEATURE [App::DocumentObjectGroupPython] H_element660  label="H_element : 426"  # scripted group (container) (typed FeaturePython)
  n = 11
  ref = H_element
FEATURE [App::DocumentObjectGroupPython] N_element319  label="N_element : 171"  # scripted group (container) (typed FeaturePython)
  n = 1
  ref = N_element
FEATURE [App::DocumentObjectGroupPython] O_element622  label="O_element : 395"  # scripted group (container) (typed FeaturePython)
  n = 2
  ref = O_element
FEATURE [App::DocumentObjectGroupPython] G4_VALINE  # scripted group (container) (typed FeaturePython)
  Dunit = g/cm3
  Dvalue = 1.23
  Group = -> [C_element712,H_element660,N_element319,O_element622]
  conduct = 2
  density = 1
  expand = 3
  formula = G4_VALINE
  name = G4_VALINE
  specific = 4
FEATURE [App::DocumentObjectGroupPython] H_element661  label="H_element : 0.285"  # scripted group (container) (typed FeaturePython)
  n = 0.009417
FEATURE [App::DocumentObjectGroupPython] C_element713  label="C_element : 0.1016"  # scripted group (container) (typed FeaturePython)
  n = 0.280555
FEATURE [App::DocumentObjectGroupPython] F_element094  label="F_element : 0.734"  # scripted group (container) (typed FeaturePython)
  n = 0.710028
FEATURE [App::DocumentObjectGroupPython] G4_VITON  # scripted group (container) (typed FeaturePython)
  Dunit = g/cm3
  Dvalue = 1.8
  Group = -> [H_element661,C_element713,F_element094]
  conduct = 2
  density = 1
  expand = 3
  formula = G4_VITON
  name = G4_VITON
  specific = 4
FEATURE [App::DocumentObjectGroupPython] H_element662  label="H_element : 427"  # scripted group (container) (typed FeaturePython)
  n = 2
  ref = H_element
FEATURE [App::DocumentObjectGroupPython] O_element623  label="O_element : 396"  # scripted group (container) (typed FeaturePython)
  n = 1
  ref = O_element
FEATURE [App::DocumentObjectGroupPython] G4_WATER  # scripted group (container) (typed FeaturePython)
  Dunit = g/cm3
  Dvalue = 1
  Group = -> [H_element662,O_element623]
  conduct = 2
  density = 1
  expand = 3
  formula = G4_WATER
  name = G4_WATER
  specific = 4
FEATURE [App::DocumentObjectGroupPython] H_element663  label="H_element : 428"  # scripted group (container) (typed FeaturePython)
  n = 2
  ref = H_element
FEATURE [App::DocumentObjectGroupPython] O_element624  label="O_element : 397"  # scripted group (container) (typed FeaturePython)
  n = 1
  ref = O_element
FEATURE [App::DocumentObjectGroupPython] G4_WATER_VAPOR  # scripted group (container) (typed FeaturePython)
  Dunit = g/cm3
  Dvalue = 0.000756182
  Group = -> [H_element663,O_element624]
  conduct = 2
  density = 1
  expand = 3
  formula = G4_WATER_VAPOR
  name = G4_WATER_VAPOR
  specific = 4
FEATURE [App::DocumentObjectGroupPython] C_element714  label="C_element : 468"  # scripted group (container) (typed FeaturePython)
  n = 8
  ref = C_element
FEATURE [App::DocumentObjectGroupPython] H_element664  label="H_element : 429"  # scripted group (container) (typed FeaturePython)
  n = 10
  ref = H_element
FEATURE [App::DocumentObjectGroupPython] G4_XYLENE  # scripted group (container) (typed FeaturePython)
  Dunit = g/cm3
  Dvalue = 0.87
  Group = -> [C_element714,H_element664]
  conduct = 2
  density = 1
  expand = 3
  formula = G4_XYLENE
  name = G4_XYLENE
  specific = 4
FEATURE [App::DocumentObjectGroupPython] C_element715  label="C_element : 469"  # scripted group (container) (typed FeaturePython)
  n = 1
  ref = C_element
FEATURE [App::DocumentObjectGroupPython] G4_GRAPHITE  # scripted group (container) (typed FeaturePython)
  Dunit = g/cm3
  Dvalue = 2.21
  Group = -> [C_element715]
  conduct = 2
  density = 1
  expand = 3
  formula = G4_GRAPHITE
  name = G4_GRAPHITE
  specific = 4
FEATURE [App::DocumentObjectGroupPython] NIST  # scripted group (container) (typed FeaturePython)
  Group = -> [G4_A_150_TISSUE,G4_ACETONE,G4_ACETYLENE,G4_ADENINE,G4_ADIPOSE_TISSUE_ICRP,G4_AIR,G4_ALANINE,G4_ALUMINUM_OXIDE,G4_AMBER,G4_AMMONIA,G4_ANILINE,G4_ANTHRACENE,G4_B_100_BONE,G4_BAKELITE,G4_BARIUM_FLUORIDE,G4_BARIUM_SULFATE,G4_BENZENE,G4_BERYLLIUM_OXIDE,G4_BGO,G4_BLOOD_ICRP,G4_BONE_COMPACT_ICRU,G4_BONE_CORTICAL_ICRP,G4_BORON_CARBIDE,G4_BORON_OXIDE,G4_BRAIN_ICRP,G4_BUTANE,G4_N_BUTYL_ALCOHOL,G4_C_552,+152 more]
FEATURE [App::DocumentObjectGroupPython] H_element665  label="H_element : 430"  # scripted group (container) (typed FeaturePython)
  n = 1
  ref = H_element
FEATURE [App::DocumentObjectGroupPython] G4_H  # scripted group (container) (typed FeaturePython)
  Dunit = g/cm3
  Dvalue = 8.3748e-05
  Group = -> [H_element665]
  conduct = 2
  density = 1
  expand = 3
  formula = H
  name = G4_H
  specific = 4
FEATURE [App::DocumentObjectGroupPython] He_element005  label="He_element : 004"  # scripted group (container) (typed FeaturePython)
  n = 1
  ref = He_element
FEATURE [App::DocumentObjectGroupPython] G4_He  # scripted group (container) (typed FeaturePython)
  Dunit = g/cm3
  Dvalue = 0.000166322
  Group = -> [He_element005]
  conduct = 2
  density = 1
  expand = 3
  formula = He
  name = G4_He
  specific = 4
FEATURE [App::DocumentObjectGroupPython] Li_element040  label="Li_element : 038"  # scripted group (container) (typed FeaturePython)
  n = 1
  ref = Li_element
FEATURE [App::DocumentObjectGroupPython] G4_Li  # scripted group (container) (typed FeaturePython)
  Dunit = g/cm3
  Dvalue = 0.534
  Group = -> [Li_element040]
  conduct = 2
  density = 1
  expand = 3
  formula = Li
  name = G4_Li
  specific = 4
FEATURE [App::DocumentObjectGroupPython] Be_element010  label="Be_element : 009"  # scripted group (container) (typed FeaturePython)
  n = 1
  ref = Be_element
FEATURE [App::DocumentObjectGroupPython] G4_Be  # scripted group (container) (typed FeaturePython)
  Dunit = g/cm3
  Dvalue = 1.848
  Group = -> [Be_element010]
  conduct = 2
  density = 1
  expand = 3
  formula = Be
  name = G4_Be
  specific = 4
FEATURE [App::DocumentObjectGroupPython] B_element035  label="B_element : 028"  # scripted group (container) (typed FeaturePython)
  n = 1
  ref = B_element
FEATURE [App::DocumentObjectGroupPython] G4_B  # scripted group (container) (typed FeaturePython)
  Dunit = g/cm3
  Dvalue = 2.37
  Group = -> [B_element035]
  conduct = 2
  density = 1
  expand = 3
  formula = B
  name = G4_B
  specific = 4
FEATURE [App::DocumentObjectGroupPython] C_element716  label="C_element : 470"  # scripted group (container) (typed FeaturePython)
  n = 1
  ref = C_element
FEATURE [App::DocumentObjectGroupPython] G4_C  # scripted group (container) (typed FeaturePython)
  Dunit = g/cm3
  Dvalue = 2
  Group = -> [C_element716]
  conduct = 2
  density = 1
  expand = 3
  formula = C
  name = G4_C
  specific = 4
FEATURE [App::DocumentObjectGroupPython] N_element320  label="N_element : 172"  # scripted group (container) (typed FeaturePython)
  n = 1
  ref = N_element
FEATURE [App::DocumentObjectGroupPython] G4_N  # scripted group (container) (typed FeaturePython)
  Dunit = g/cm3
  Dvalue = 0.0011652
  Group = -> [N_element320]
  conduct = 2
  density = 1
  expand = 3
  formula = N
  name = G4_N
  specific = 4
FEATURE [App::DocumentObjectGroupPython] O_element625  label="O_element : 398"  # scripted group (container) (typed FeaturePython)
  n = 1
  ref = O_element
FEATURE [App::DocumentObjectGroupPython] G4_O  # scripted group (container) (typed FeaturePython)
  Dunit = g/cm3
  Dvalue = 0.00133151
  Group = -> [O_element625]
  conduct = 2
  density = 1
  expand = 3
  formula = O
  name = G4_O
  specific = 4
FEATURE [App::DocumentObjectGroupPython] F_element095  label="F_element : 047"  # scripted group (container) (typed FeaturePython)
  n = 1
  ref = F_element
FEATURE [App::DocumentObjectGroupPython] G4_F  # scripted group (container) (typed FeaturePython)
  Dunit = g/cm3
  Dvalue = 0.00158029
  Group = -> [F_element095]
  conduct = 2
  density = 1
  expand = 3
  formula = F
  name = G4_F
  specific = 4
FEATURE [App::DocumentObjectGroupPython] Ne_element005  label="Ne_element : 004"  # scripted group (container) (typed FeaturePython)
  n = 1
  ref = Ne_element
FEATURE [App::DocumentObjectGroupPython] G4_Ne  # scripted group (container) (typed FeaturePython)
  Dunit = g/cm3
  Dvalue = 0.000838505
  Group = -> [Ne_element005]
  conduct = 2
  density = 1
  expand = 3
  formula = Ne
  name = G4_Ne
  specific = 4
FEATURE [App::DocumentObjectGroupPython] Na_element100  label="Na_element : 023"  # scripted group (container) (typed FeaturePython)
  n = 1
  ref = Na_element
FEATURE [App::DocumentObjectGroupPython] G4_Na  # scripted group (container) (typed FeaturePython)
  Dunit = g/cm3
  Dvalue = 0.971
  Group = -> [Na_element100]
  conduct = 2
  density = 1
  expand = 3
  formula = Na
  name = G4_Na
  specific = 4
FEATURE [App::DocumentObjectGroupPython] Mg_element055  label="Mg_element : 024"  # scripted group (container) (typed FeaturePython)
  n = 1
  ref = Mg_element
FEATURE [App::DocumentObjectGroupPython] G4_Mg  # scripted group (container) (typed FeaturePython)
  Dunit = g/cm3
  Dvalue = 1.74
  Group = -> [Mg_element055]
  conduct = 2
  density = 1
  expand = 3
  formula = Mg
  name = G4_Mg
  specific = 4
FEATURE [App::DocumentObjectGroupPython] Al_element020  label="Al_element : 008"  # scripted group (container) (typed FeaturePython)
  n = 1
  ref = Al_element
FEATURE [App::DocumentObjectGroupPython] G4_Al  # scripted group (container) (typed FeaturePython)
  Dunit = g/cm3
  Dvalue = 2.699
  Group = -> [Al_element020]
  conduct = 2
  density = 1
  expand = 3
  formula = Al
  name = G4_Al
  specific = 4
FEATURE [App::DocumentObjectGroupPython] Si_element035  label="Si_element : 009"  # scripted group (container) (typed FeaturePython)
  n = 1
  ref = Si_element
FEATURE [App::DocumentObjectGroupPython] G4_Si  # scripted group (container) (typed FeaturePython)
  Dunit = g/cm3
  Dvalue = 2.33
  Group = -> [Si_element035]
  conduct = 2
  density = 1
  expand = 3
  formula = Si
  name = G4_Si
  specific = 4
FEATURE [App::DocumentObjectGroupPython] P_element089  label="P_element : 033"  # scripted group (container) (typed FeaturePython)
  n = 1
  ref = P_element
FEATURE [App::DocumentObjectGroupPython] G4_P  # scripted group (container) (typed FeaturePython)
  Dunit = g/cm3
  Dvalue = 2.2
  Group = -> [P_element089]
  conduct = 2
  density = 1
  expand = 3
  formula = P
  name = G4_P
  specific = 4
FEATURE [App::DocumentObjectGroupPython] S_element115  label="S_element : 034"  # scripted group (container) (typed FeaturePython)
  n = 1
  ref = S_element
FEATURE [App::DocumentObjectGroupPython] G4_S  # scripted group (container) (typed FeaturePython)
  Dunit = g/cm3
  Dvalue = 2
  Group = -> [S_element115]
  conduct = 2
  density = 1
  expand = 3
  formula = S
  name = G4_S
  specific = 4
FEATURE [App::DocumentObjectGroupPython] Cl_element149  label="Cl_element : 075"  # scripted group (container) (typed FeaturePython)
  n = 1
  ref = Cl_element
FEATURE [App::DocumentObjectGroupPython] G4_Cl  # scripted group (container) (typed FeaturePython)
  Dunit = g/cm3
  Dvalue = 0.00299473
  Group = -> [Cl_element149]
  conduct = 2
  density = 1
  expand = 3
  formula = Cl
  name = G4_Cl
  specific = 4
FEATURE [App::DocumentObjectGroupPython] Ar_element010  label="Ar_element : 004"  # scripted group (container) (typed FeaturePython)
  n = 1
  ref = Ar_element
FEATURE [App::DocumentObjectGroupPython] G4_Ar  # scripted group (container) (typed FeaturePython)
  Dunit = g/cm3
  Dvalue = 0.00166201
  Group = -> [Ar_element010]
  conduct = 2
  density = 1
  expand = 3
  formula = Ar
  name = G4_Ar
  specific = 4
FEATURE [App::DocumentObjectGroupPython] K_element065  label="K_element : 013"  # scripted group (container) (typed FeaturePython)
  n = 1
  ref = K_element
FEATURE [App::DocumentObjectGroupPython] G4_K  # scripted group (container) (typed FeaturePython)
  Dunit = g/cm3
  Dvalue = 0.862
  Group = -> [K_element065]
  conduct = 2
  density = 1
  expand = 3
  formula = K
  name = G4_K
  specific = 4
FEATURE [App::DocumentObjectGroupPython] Ca_element070  label="Ca_element : 034"  # scripted group (container) (typed FeaturePython)
  n = 1
  ref = Ca_element
FEATURE [App::DocumentObjectGroupPython] G4_Ca  # scripted group (container) (typed FeaturePython)
  Dunit = g/cm3
  Dvalue = 1.55
  Group = -> [Ca_element070]
  conduct = 2
  density = 1
  expand = 3
  formula = Ca
  name = G4_Ca
  specific = 4
FEATURE [App::DocumentObjectGroupPython] Sc_element005  label="Sc_element : 004"  # scripted group (container) (typed FeaturePython)
  n = 1
  ref = Sc_element
FEATURE [App::DocumentObjectGroupPython] G4_Sc  # scripted group (container) (typed FeaturePython)
  Dunit = g/cm3
  Dvalue = 2.989
  Group = -> [Sc_element005]
  conduct = 2
  density = 1
  expand = 3
  formula = Sc
  name = G4_Sc
  specific = 4
FEATURE [App::DocumentObjectGroupPython] Ti_element020  label="Ti_element : 009"  # scripted group (container) (typed FeaturePython)
  n = 1
  ref = Ti_element
FEATURE [App::DocumentObjectGroupPython] G4_Ti  # scripted group (container) (typed FeaturePython)
  Dunit = g/cm3
  Dvalue = 4.54
  Group = -> [Ti_element020]
  conduct = 2
  density = 1
  expand = 3
  formula = Ti
  name = G4_Ti
  specific = 4
FEATURE [App::DocumentObjectGroupPython] V_element005  label="V_element : 004"  # scripted group (container) (typed FeaturePython)
  n = 1
  ref = V_element
FEATURE [App::DocumentObjectGroupPython] G4_V  # scripted group (container) (typed FeaturePython)
  Dunit = g/cm3
  Dvalue = 6.11
  Group = -> [V_element005]
  conduct = 2
  density = 1
  expand = 3
  formula = V
  name = G4_V
  specific = 4
FEATURE [App::DocumentObjectGroupPython] Cr_element009  label="Cr_element : 023"  # scripted group (container) (typed FeaturePython)
  n = 1
  ref = Cr_element
FEATURE [App::DocumentObjectGroupPython] G4_Cr  # scripted group (container) (typed FeaturePython)
  Dunit = g/cm3
  Dvalue = 7.18
  Group = -> [Cr_element009]
  conduct = 2
  density = 1
  expand = 3
  formula = Cr
  name = G4_Cr
  specific = 4
FEATURE [App::DocumentObjectGroupPython] Mn_element005  label="Mn_element : 004"  # scripted group (container) (typed FeaturePython)
  n = 1
  ref = Mn_element
FEATURE [App::DocumentObjectGroupPython] G4_Mn  # scripted group (container) (typed FeaturePython)
  Dunit = g/cm3
  Dvalue = 7.44
  Group = -> [Mn_element005]
  conduct = 2
  density = 1
  expand = 3
  formula = Mn
  name = G4_Mn
  specific = 4
FEATURE [App::DocumentObjectGroupPython] Fe_element039  label="Fe_element : 020"  # scripted group (container) (typed FeaturePython)
  n = 1
  ref = Fe_element
FEATURE [App::DocumentObjectGroupPython] G4_Fe  # scripted group (container) (typed FeaturePython)
  Dunit = g/cm3
  Dvalue = 7.874
  Group = -> [Fe_element039]
  conduct = 2
  density = 1
  expand = 3
  formula = Fe
  name = G4_Fe
  specific = 4
FEATURE [App::DocumentObjectGroupPython] Co_element005  label="Co_element : 004"  # scripted group (container) (typed FeaturePython)
  n = 1
  ref = Co_element
FEATURE [App::DocumentObjectGroupPython] G4_Co  # scripted group (container) (typed FeaturePython)
  Dunit = g/cm3
  Dvalue = 8.9
  Group = -> [Co_element005]
  conduct = 2
  density = 1
  expand = 3
  formula = Co
  name = G4_Co
  specific = 4
FEATURE [App::DocumentObjectGroupPython] Ni_element009  label="Ni_element : 013"  # scripted group (container) (typed FeaturePython)
  n = 1
  ref = Ni_element
FEATURE [App::DocumentObjectGroupPython] G4_Ni  # scripted group (container) (typed FeaturePython)
  Dunit = g/cm3
  Dvalue = 8.902
  Group = -> [Ni_element009]
  conduct = 2
  density = 1
  expand = 3
  formula = Ni
  name = G4_Ni
  specific = 4
FEATURE [App::DocumentObjectGroupPython] Cu_element013  label="Cu_element : 096"  # scripted group (container) (typed FeaturePython)
  n = 1
  ref = Cu_element
FEATURE [App::DocumentObjectGroupPython] G4_Cu  # scripted group (container) (typed FeaturePython)
  Dunit = g/cm3
  Dvalue = 8.96
  Group = -> [Cu_element013]
  conduct = 2
  density = 1
  expand = 3
  formula = Cu
  name = G4_Cu
  specific = 4
FEATURE [App::DocumentObjectGroupPython] Zn_element013  label="Zn_element : 042"  # scripted group (container) (typed FeaturePython)
  n = 1
  ref = Zn_element
FEATURE [App::DocumentObjectGroupPython] G4_Zn  # scripted group (container) (typed FeaturePython)
  Dunit = g/cm3
  Dvalue = 7.133
  Group = -> [Zn_element013]
  conduct = 2
  density = 1
  expand = 3
  formula = Zn
  name = G4_Zn
  specific = 4
FEATURE [App::DocumentObjectGroupPython] Ga_element010  label="Ga_element : 009"  # scripted group (container) (typed FeaturePython)
  n = 1
  ref = Ga_element
FEATURE [App::DocumentObjectGroupPython] G4_Ga  # scripted group (container) (typed FeaturePython)
  Dunit = g/cm3
  Dvalue = 5.904
  Group = -> [Ga_element010]
  conduct = 2
  density = 1
  expand = 3
  formula = Ga
  name = G4_Ga
  specific = 4
FEATURE [App::DocumentObjectGroupPython] Ge_element010  label="Ge_element : 009"  # scripted group (container) (typed FeaturePython)
  n = 1
  ref = Ge_element
FEATURE [App::DocumentObjectGroupPython] G4_Ge  # scripted group (container) (typed FeaturePython)
  Dunit = g/cm3
  Dvalue = 5.323
  Group = -> [Ge_element010]
  conduct = 2
  density = 1
  expand = 3
  formula = Ge
  name = G4_Ge
  specific = 4
FEATURE [App::DocumentObjectGroupPython] As_element015  label="As_element : 009"  # scripted group (container) (typed FeaturePython)
  n = 1
  ref = As_element
FEATURE [App::DocumentObjectGroupPython] G4_As  # scripted group (container) (typed FeaturePython)
  Dunit = g/cm3
  Dvalue = 5.73
  Group = -> [As_element015]
  conduct = 2
  density = 1
  expand = 3
  formula = As
  name = G4_As
  specific = 4
FEATURE [App::DocumentObjectGroupPython] Se_element005  label="Se_element : 004"  # scripted group (container) (typed FeaturePython)
  n = 1
  ref = Se_element
FEATURE [App::DocumentObjectGroupPython] G4_Se  # scripted group (container) (typed FeaturePython)
  Dunit = g/cm3
  Dvalue = 4.5
  Group = -> [Se_element005]
  conduct = 2
  density = 1
  expand = 3
  formula = Se
  name = G4_Se
  specific = 4
FEATURE [App::DocumentObjectGroupPython] Br_element035  label="Br_element : 019"  # scripted group (container) (typed FeaturePython)
  n = 1
  ref = Br_element
FEATURE [App::DocumentObjectGroupPython] G4_Br  # scripted group (container) (typed FeaturePython)
  Dunit = g/cm3
  Dvalue = 0.0070721
  Group = -> [Br_element035]
  conduct = 2
  density = 1
  expand = 3
  formula = Br
  name = G4_Br
  specific = 4
FEATURE [App::DocumentObjectGroupPython] Kr_element005  label="Kr_element : 004"  # scripted group (container) (typed FeaturePython)
  n = 1
  ref = Kr_element
FEATURE [App::DocumentObjectGroupPython] G4_Kr  # scripted group (container) (typed FeaturePython)
  Dunit = g/cm3
  Dvalue = 0.00347832
  Group = -> [Kr_element005]
  conduct = 2
  density = 1
  expand = 3
  formula = Kr
  name = G4_Kr
  specific = 4
FEATURE [App::DocumentObjectGroupPython] Rb_element005  label="Rb_element : 004"  # scripted group (container) (typed FeaturePython)
  n = 1
  ref = Rb_element
FEATURE [App::DocumentObjectGroupPython] G4_Rb  # scripted group (container) (typed FeaturePython)
  Dunit = g/cm3
  Dvalue = 1.532
  Group = -> [Rb_element005]
  conduct = 2
  density = 1
  expand = 3
  formula = Rb
  name = G4_Rb
  specific = 4
FEATURE [App::DocumentObjectGroupPython] Sr_element005  label="Sr_element : 004"  # scripted group (container) (typed FeaturePython)
  n = 1
  ref = Sr_element
FEATURE [App::DocumentObjectGroupPython] G4_Sr  # scripted group (container) (typed FeaturePython)
  Dunit = g/cm3
  Dvalue = 2.54
  Group = -> [Sr_element005]
  conduct = 2
  density = 1
  expand = 3
  formula = Sr
  name = G4_Sr
  specific = 4
FEATURE [App::DocumentObjectGroupPython] Y_element005  label="Y_element : 004"  # scripted group (container) (typed FeaturePython)
  n = 1
  ref = Y_element
FEATURE [App::DocumentObjectGroupPython] G4_Y  # scripted group (container) (typed FeaturePython)
  Dunit = g/cm3
  Dvalue = 4.469
  Group = -> [Y_element005]
  conduct = 2
  density = 1
  expand = 3
  formula = Y
  name = G4_Y
  specific = 4
FEATURE [App::DocumentObjectGroupPython] Zr_element005  label="Zr_element : 004"  # scripted group (container) (typed FeaturePython)
  n = 1
  ref = Zr_element
FEATURE [App::DocumentObjectGroupPython] G4_Zr  # scripted group (container) (typed FeaturePython)
  Dunit = g/cm3
  Dvalue = 6.506
  Group = -> [Zr_element005]
  conduct = 2
  density = 1
  expand = 3
  formula = Zr
  name = G4_Zr
  specific = 4
FEATURE [App::DocumentObjectGroupPython] Nb_element005  label="Nb_element : 004"  # scripted group (container) (typed FeaturePython)
  n = 1
  ref = Nb_element
FEATURE [App::DocumentObjectGroupPython] G4_Nb  # scripted group (container) (typed FeaturePython)
  Dunit = g/cm3
  Dvalue = 8.57
  Group = -> [Nb_element005]
  conduct = 2
  density = 1
  expand = 3
  formula = Nb
  name = G4_Nb
  specific = 4
FEATURE [App::DocumentObjectGroupPython] Mo_element005  label="Mo_element : 004"  # scripted group (container) (typed FeaturePython)
  n = 1
  ref = Mo_element
FEATURE [App::DocumentObjectGroupPython] G4_Mo  # scripted group (container) (typed FeaturePython)
  Dunit = g/cm3
  Dvalue = 10.22
  Group = -> [Mo_element005]
  conduct = 2
  density = 1
  expand = 3
  formula = Mo
  name = G4_Mo
  specific = 4
FEATURE [App::DocumentObjectGroupPython] Tc_element005  label="Tc_element : 004"  # scripted group (container) (typed FeaturePython)
  n = 1
  ref = Tc_element
FEATURE [App::DocumentObjectGroupPython] G4_Tc  # scripted group (container) (typed FeaturePython)
  Dunit = g/cm3
  Dvalue = 11.5
  Group = -> [Tc_element005]
  conduct = 2
  density = 1
  expand = 3
  formula = Tc
  name = G4_Tc
  specific = 4
FEATURE [App::DocumentObjectGroupPython] Ru_element005  label="Ru_element : 004"  # scripted group (container) (typed FeaturePython)
  n = 1
  ref = Ru_element
FEATURE [App::DocumentObjectGroupPython] G4_Ru  # scripted group (container) (typed FeaturePython)
  Dunit = g/cm3
  Dvalue = 12.41
  Group = -> [Ru_element005]
  conduct = 2
  density = 1
  expand = 3
  formula = Ru
  name = G4_Ru
  specific = 4
FEATURE [App::DocumentObjectGroupPython] Rh_element005  label="Rh_element : 004"  # scripted group (container) (typed FeaturePython)
  n = 1
  ref = Rh_element
FEATURE [App::DocumentObjectGroupPython] G4_Rh  # scripted group (container) (typed FeaturePython)
  Dunit = g/cm3
  Dvalue = 12.41
  Group = -> [Rh_element005]
  conduct = 2
  density = 1
  expand = 3
  formula = Rh
  name = G4_Rh
  specific = 4
FEATURE [App::DocumentObjectGroupPython] Pd_element005  label="Pd_element : 004"  # scripted group (container) (typed FeaturePython)
  n = 1
  ref = Pd_element
FEATURE [App::DocumentObjectGroupPython] G4_Pd  # scripted group (container) (typed FeaturePython)
  Dunit = g/cm3
  Dvalue = 12.02
  Group = -> [Pd_element005]
  conduct = 2
  density = 1
  expand = 3
  formula = Pd
  name = G4_Pd
  specific = 4
FEATURE [App::DocumentObjectGroupPython] Ag_element030  label="Ag_element : 019"  # scripted group (container) (typed FeaturePython)
  n = 1
  ref = Ag_element
FEATURE [App::DocumentObjectGroupPython] G4_Ag  # scripted group (container) (typed FeaturePython)
  Dunit = g/cm3
  Dvalue = 10.5
  Group = -> [Ag_element030]
  conduct = 2
  density = 1
  expand = 3
  formula = Ag
  name = G4_Ag
  specific = 4
FEATURE [App::DocumentObjectGroupPython] Cd_element015  label="Cd_element : 014"  # scripted group (container) (typed FeaturePython)
  n = 1
  ref = Cd_element
FEATURE [App::DocumentObjectGroupPython] G4_Cd  # scripted group (container) (typed FeaturePython)
  Dunit = g/cm3
  Dvalue = 8.65
  Group = -> [Cd_element015]
  conduct = 2
  density = 1
  expand = 3
  formula = Cd
  name = G4_Cd
  specific = 4
FEATURE [App::DocumentObjectGroupPython] In_element005  label="In_element : 004"  # scripted group (container) (typed FeaturePython)
  n = 1
  ref = In_element
FEATURE [App::DocumentObjectGroupPython] G4_In  # scripted group (container) (typed FeaturePython)
  Dunit = g/cm3
  Dvalue = 7.31
  Group = -> [In_element005]
  conduct = 2
  density = 1
  expand = 3
  formula = In
  name = G4_In
  specific = 4
FEATURE [App::DocumentObjectGroupPython] Sn_element005  label="Sn_element : 004"  # scripted group (container) (typed FeaturePython)
  n = 1
  ref = Sn_element
FEATURE [App::DocumentObjectGroupPython] G4_Sn  # scripted group (container) (typed FeaturePython)
  Dunit = g/cm3
  Dvalue = 7.31
  Group = -> [Sn_element005]
  conduct = 2
  density = 1
  expand = 3
  formula = Sn
  name = G4_Sn
  specific = 4
FEATURE [App::DocumentObjectGroupPython] Sb_element005  label="Sb_element : 004"  # scripted group (container) (typed FeaturePython)
  n = 1
  ref = Sb_element
FEATURE [App::DocumentObjectGroupPython] G4_Sb  # scripted group (container) (typed FeaturePython)
  Dunit = g/cm3
  Dvalue = 6.691
  Group = -> [Sb_element005]
  conduct = 2
  density = 1
  expand = 3
  formula = Sb
  name = G4_Sb
  specific = 4
FEATURE [App::DocumentObjectGroupPython] Te_element010  label="Te_element : 009"  # scripted group (container) (typed FeaturePython)
  n = 1
  ref = Te_element
FEATURE [App::DocumentObjectGroupPython] G4_Te  # scripted group (container) (typed FeaturePython)
  Dunit = g/cm3
  Dvalue = 6.24
  Group = -> [Te_element010]
  conduct = 2
  density = 1
  expand = 3
  formula = Te
  name = G4_Te
  specific = 4
FEATURE [App::DocumentObjectGroupPython] I_element050  label="I_element : 032"  # scripted group (container) (typed FeaturePython)
  n = 1
  ref = I_element
FEATURE [App::DocumentObjectGroupPython] G4_I  # scripted group (container) (typed FeaturePython)
  Dunit = g/cm3
  Dvalue = 4.93
  Group = -> [I_element050]
  conduct = 2
  density = 1
  expand = 3
  formula = I
  name = G4_I
  specific = 4
FEATURE [App::DocumentObjectGroupPython] Xe_element005  label="Xe_element : 004"  # scripted group (container) (typed FeaturePython)
  n = 1
  ref = Xe_element
FEATURE [App::DocumentObjectGroupPython] G4_Xe  # scripted group (container) (typed FeaturePython)
  Dunit = g/cm3
  Dvalue = 0.00548536
  Group = -> [Xe_element005]
  conduct = 2
  density = 1
  expand = 3
  formula = Xe
  name = G4_Xe
  specific = 4
FEATURE [App::DocumentObjectGroupPython] Cs_element015  label="Cs_element : 014"  # scripted group (container) (typed FeaturePython)
  n = 1
  ref = Cs_element
FEATURE [App::DocumentObjectGroupPython] G4_Cs  # scripted group (container) (typed FeaturePython)
  Dunit = g/cm3
  Dvalue = 1.873
  Group = -> [Cs_element015]
  conduct = 2
  density = 1
  expand = 3
  formula = Cs
  name = G4_Cs
  specific = 4
FEATURE [App::DocumentObjectGroupPython] Ba_element015  label="Ba_element : 014"  # scripted group (container) (typed FeaturePython)
  n = 1
  ref = Ba_element
FEATURE [App::DocumentObjectGroupPython] G4_Ba  # scripted group (container) (typed FeaturePython)
  Dunit = g/cm3
  Dvalue = 3.5
  Group = -> [Ba_element015]
  conduct = 2
  density = 1
  expand = 3
  formula = Ba
  name = G4_Ba
  specific = 4
FEATURE [App::DocumentObjectGroupPython] La_element015  label="La_element : 013"  # scripted group (container) (typed FeaturePython)
  n = 1
  ref = La_element
FEATURE [App::DocumentObjectGroupPython] G4_La  # scripted group (container) (typed FeaturePython)
  Dunit = g/cm3
  Dvalue = 6.154
  Group = -> [La_element015]
  conduct = 2
  density = 1
  expand = 3
  formula = La
  name = G4_La
  specific = 4
FEATURE [App::DocumentObjectGroupPython] Ce_element010  label="Ce_element : 004"  # scripted group (container) (typed FeaturePython)
  n = 1
  ref = Ce_element
FEATURE [App::DocumentObjectGroupPython] G4_Ce  # scripted group (container) (typed FeaturePython)
  Dunit = g/cm3
  Dvalue = 6.657
  Group = -> [Ce_element010]
  conduct = 2
  density = 1
  expand = 3
  formula = Ce
  name = G4_Ce
  specific = 4
FEATURE [App::DocumentObjectGroupPython] Pr_element005  label="Pr_element : 004"  # scripted group (container) (typed FeaturePython)
  n = 1
  ref = Pr_element
FEATURE [App::DocumentObjectGroupPython] G4_Pr  # scripted group (container) (typed FeaturePython)
  Dunit = g/cm3
  Dvalue = 6.71
  Group = -> [Pr_element005]
  conduct = 2
  density = 1
  expand = 3
  formula = Pr
  name = G4_Pr
  specific = 4
FEATURE [App::DocumentObjectGroupPython] Nd_element005  label="Nd_element : 004"  # scripted group (container) (typed FeaturePython)
  n = 1
  ref = Nd_element
FEATURE [App::DocumentObjectGroupPython] G4_Nd  # scripted group (container) (typed FeaturePython)
  Dunit = g/cm3
  Dvalue = 6.9
  Group = -> [Nd_element005]
  conduct = 2
  density = 1
  expand = 3
  formula = Nd
  name = G4_Nd
  specific = 4
FEATURE [App::DocumentObjectGroupPython] Pm_element005  label="Pm_element : 004"  # scripted group (container) (typed FeaturePython)
  n = 1
  ref = Pm_element
FEATURE [App::DocumentObjectGroupPython] G4_Pm  # scripted group (container) (typed FeaturePython)
  Dunit = g/cm3
  Dvalue = 7.22
  Group = -> [Pm_element005]
  conduct = 2
  density = 1
  expand = 3
  formula = Pm
  name = G4_Pm
  specific = 4
FEATURE [App::DocumentObjectGroupPython] Sm_element005  label="Sm_element : 004"  # scripted group (container) (typed FeaturePython)
  n = 1
  ref = Sm_element
FEATURE [App::DocumentObjectGroupPython] G4_Sm  # scripted group (container) (typed FeaturePython)
  Dunit = g/cm3
  Dvalue = 7.46
  Group = -> [Sm_element005]
  conduct = 2
  density = 1
  expand = 3
  formula = Sm
  name = G4_Sm
  specific = 4
FEATURE [App::DocumentObjectGroupPython] Eu_element005  label="Eu_element : 004"  # scripted group (container) (typed FeaturePython)
  n = 1
  ref = Eu_element
FEATURE [App::DocumentObjectGroupPython] G4_Eu  # scripted group (container) (typed FeaturePython)
  Dunit = g/cm3
  Dvalue = 5.243
  Group = -> [Eu_element005]
  conduct = 2
  density = 1
  expand = 3
  formula = Eu
  name = G4_Eu
  specific = 4
FEATURE [App::DocumentObjectGroupPython] Gd_element010  label="Gd_element : 008"  # scripted group (container) (typed FeaturePython)
  n = 1
  ref = Gd_element
FEATURE [App::DocumentObjectGroupPython] G4_Gd  # scripted group (container) (typed FeaturePython)
  Dunit = g/cm3
  Dvalue = 7.9004
  Group = -> [Gd_element010]
  conduct = 2
  density = 1
  expand = 3
  formula = Gd
  name = G4_Gd
  specific = 4
FEATURE [App::DocumentObjectGroupPython] Tb_element005  label="Tb_element : 004"  # scripted group (container) (typed FeaturePython)
  n = 1
  ref = Tb_element
FEATURE [App::DocumentObjectGroupPython] G4_Tb  # scripted group (container) (typed FeaturePython)
  Dunit = g/cm3
  Dvalue = 8.229
  Group = -> [Tb_element005]
  conduct = 2
  density = 1
  expand = 3
  formula = Tb
  name = G4_Tb
  specific = 4
FEATURE [App::DocumentObjectGroupPython] Dy_element005  label="Dy_element : 004"  # scripted group (container) (typed FeaturePython)
  n = 1
  ref = Dy_element
FEATURE [App::DocumentObjectGroupPython] G4_Dy  # scripted group (container) (typed FeaturePython)
  Dunit = g/cm3
  Dvalue = 8.55
  Group = -> [Dy_element005]
  conduct = 2
  density = 1
  expand = 3
  formula = Dy
  name = G4_Dy
  specific = 4
FEATURE [App::DocumentObjectGroupPython] Ho_element005  label="Ho_element : 004"  # scripted group (container) (typed FeaturePython)
  n = 1
  ref = Ho_element
FEATURE [App::DocumentObjectGroupPython] G4_Ho  # scripted group (container) (typed FeaturePython)
  Dunit = g/cm3
  Dvalue = 8.795
  Group = -> [Ho_element005]
  conduct = 2
  density = 1
  expand = 3
  formula = Ho
  name = G4_Ho
  specific = 4
FEATURE [App::DocumentObjectGroupPython] Er_element005  label="Er_element : 004"  # scripted group (container) (typed FeaturePython)
  n = 1
  ref = Er_element
FEATURE [App::DocumentObjectGroupPython] G4_Er  # scripted group (container) (typed FeaturePython)
  Dunit = g/cm3
  Dvalue = 9.066
  Group = -> [Er_element005]
  conduct = 2
  density = 1
  expand = 3
  formula = Er
  name = G4_Er
  specific = 4
FEATURE [App::DocumentObjectGroupPython] Tm_element005  label="Tm_element : 004"  # scripted group (container) (typed FeaturePython)
  n = 1
  ref = Tm_element
FEATURE [App::DocumentObjectGroupPython] G4_Tm  # scripted group (container) (typed FeaturePython)
  Dunit = g/cm3
  Dvalue = 9.321
  Group = -> [Tm_element005]
  conduct = 2
  density = 1
  expand = 3
  formula = Tm
  name = G4_Tm
  specific = 4
FEATURE [App::DocumentObjectGroupPython] Yb_element005  label="Yb_element : 004"  # scripted group (container) (typed FeaturePython)
  n = 1
  ref = Yb_element
FEATURE [App::DocumentObjectGroupPython] G4_Yb  # scripted group (container) (typed FeaturePython)
  Dunit = g/cm3
  Dvalue = 6.73
  Group = -> [Yb_element005]
  conduct = 2
  density = 1
  expand = 3
  formula = Yb
  name = G4_Yb
  specific = 4
FEATURE [App::DocumentObjectGroupPython] Lu_element005  label="Lu_element : 004"  # scripted group (container) (typed FeaturePython)
  n = 1
  ref = Lu_element
FEATURE [App::DocumentObjectGroupPython] G4_Lu  # scripted group (container) (typed FeaturePython)
  Dunit = g/cm3
  Dvalue = 9.84
  Group = -> [Lu_element005]
  conduct = 2
  density = 1
  expand = 3
  formula = Lu
  name = G4_Lu
  specific = 4
FEATURE [App::DocumentObjectGroupPython] Hf_element005  label="Hf_element : 004"  # scripted group (container) (typed FeaturePython)
  n = 1
  ref = Hf_element
FEATURE [App::DocumentObjectGroupPython] G4_Hf  # scripted group (container) (typed FeaturePython)
  Dunit = g/cm3
  Dvalue = 13.31
  Group = -> [Hf_element005]
  conduct = 2
  density = 1
  expand = 3
  formula = Hf
  name = G4_Hf
  specific = 4
FEATURE [App::DocumentObjectGroupPython] Ta_element005  label="Ta_element : 004"  # scripted group (container) (typed FeaturePython)
  n = 1
  ref = Ta_element
FEATURE [App::DocumentObjectGroupPython] G4_Ta  # scripted group (container) (typed FeaturePython)
  Dunit = g/cm3
  Dvalue = 16.654
  Group = -> [Ta_element005]
  conduct = 2
  density = 1
  expand = 3
  formula = Ta
  name = G4_Ta
  specific = 4
FEATURE [App::DocumentObjectGroupPython] W_element024  label="W_element : 023"  # scripted group (container) (typed FeaturePython)
  n = 1
  ref = W_element
FEATURE [App::DocumentObjectGroupPython] G4_W  # scripted group (container) (typed FeaturePython)
  Dunit = g/cm3
  Dvalue = 19.3
  Group = -> [W_element024]
  conduct = 2
  density = 1
  expand = 3
  formula = W
  name = G4_W
  specific = 4
FEATURE [App::DocumentObjectGroupPython] Re_element005  label="Re_element : 004"  # scripted group (container) (typed FeaturePython)
  n = 1
  ref = Re_element
FEATURE [App::DocumentObjectGroupPython] G4_Re  # scripted group (container) (typed FeaturePython)
  Dunit = g/cm3
  Dvalue = 21.02
  Group = -> [Re_element005]
  conduct = 2
  density = 1
  expand = 3
  formula = Re
  name = G4_Re
  specific = 4
FEATURE [App::DocumentObjectGroupPython] Os_element005  label="Os_element : 004"  # scripted group (container) (typed FeaturePython)
  n = 1
  ref = Os_element
FEATURE [App::DocumentObjectGroupPython] G4_Os  # scripted group (container) (typed FeaturePython)
  Dunit = g/cm3
  Dvalue = 22.57
  Group = -> [Os_element005]
  conduct = 2
  density = 1
  expand = 3
  formula = Os
  name = G4_Os
  specific = 4
FEATURE [App::DocumentObjectGroupPython] Ir_element005  label="Ir_element : 004"  # scripted group (container) (typed FeaturePython)
  n = 1
  ref = Ir_element
FEATURE [App::DocumentObjectGroupPython] G4_Ir  # scripted group (container) (typed FeaturePython)
  Dunit = g/cm3
  Dvalue = 22.42
  Group = -> [Ir_element005]
  conduct = 2
  density = 1
  expand = 3
  formula = Ir
  name = G4_Ir
  specific = 4
FEATURE [App::DocumentObjectGroupPython] Pt_element005  label="Pt_element : 004"  # scripted group (container) (typed FeaturePython)
  n = 1
  ref = Pt_element
FEATURE [App::DocumentObjectGroupPython] G4_Pt  # scripted group (container) (typed FeaturePython)
  Dunit = g/cm3
  Dvalue = 21.45
  Group = -> [Pt_element005]
  conduct = 2
  density = 1
  expand = 3
  formula = Pt
  name = G4_Pt
  specific = 4
FEATURE [App::DocumentObjectGroupPython] Au_element005  label="Au_element : 004"  # scripted group (container) (typed FeaturePython)
  n = 1
  ref = Au_element
FEATURE [App::DocumentObjectGroupPython] G4_Au  # scripted group (container) (typed FeaturePython)
  Dunit = g/cm3
  Dvalue = 19.32
  Group = -> [Au_element005]
  conduct = 2
  density = 1
  expand = 3
  formula = Au
  name = G4_Au
  specific = 4
FEATURE [App::DocumentObjectGroupPython] Hg_element010  label="Hg_element : 009"  # scripted group (container) (typed FeaturePython)
  n = 1
  ref = Hg_element
FEATURE [App::DocumentObjectGroupPython] G4_Hg  # scripted group (container) (typed FeaturePython)
  Dunit = g/cm3
  Dvalue = 13.546
  Group = -> [Hg_element010]
  conduct = 2
  density = 1
  expand = 3
  formula = Hg
  name = G4_Hg
  specific = 4
FEATURE [App::DocumentObjectGroupPython] Tl_element010  label="Tl_element : 009"  # scripted group (container) (typed FeaturePython)
  n = 1
  ref = Tl_element
FEATURE [App::DocumentObjectGroupPython] G4_Tl  # scripted group (container) (typed FeaturePython)
  Dunit = g/cm3
  Dvalue = 11.72
  Group = -> [Tl_element010]
  conduct = 2
  density = 1
  expand = 3
  formula = Tl
  name = G4_Tl
  specific = 4
FEATURE [App::DocumentObjectGroupPython] Pb_element027  label="Pb_element : 012"  # scripted group (container) (typed FeaturePython)
  n = 1
  ref = Pb_element
FEATURE [App::DocumentObjectGroupPython] G4_Pb  # scripted group (container) (typed FeaturePython)
  Dunit = g/cm3
  Dvalue = 11.35
  Group = -> [Pb_element027]
  conduct = 2
  density = 1
  expand = 3
  formula = Pb
  name = G4_Pb
  specific = 4
FEATURE [App::DocumentObjectGroupPython] Bi_element010  label="Bi_element : 010"  # scripted group (container) (typed FeaturePython)
  n = 1
  ref = Bi_element
FEATURE [App::DocumentObjectGroupPython] G4_Bi  # scripted group (container) (typed FeaturePython)
  Dunit = g/cm3
  Dvalue = 9.747
  Group = -> [Bi_element010]
  conduct = 2
  density = 1
  expand = 3
  formula = Bi
  name = G4_Bi
  specific = 4
FEATURE [App::DocumentObjectGroupPython] Po_element005  label="Po_element : 004"  # scripted group (container) (typed FeaturePython)
  n = 1
  ref = Po_element
FEATURE [App::DocumentObjectGroupPython] G4_Po  # scripted group (container) (typed FeaturePython)
  Dunit = g/cm3
  Dvalue = 9.32
  Group = -> [Po_element005]
  conduct = 2
  density = 1
  expand = 3
  formula = Po
  name = G4_Po
  specific = 4
FEATURE [App::DocumentObjectGroupPython] At_element005  label="At_element : 004"  # scripted group (container) (typed FeaturePython)
  n = 1
  ref = At_element
FEATURE [App::DocumentObjectGroupPython] G4_At  # scripted group (container) (typed FeaturePython)
  Dunit = g/cm3
  Dvalue = 9.32
  Group = -> [At_element005]
  conduct = 2
  density = 1
  expand = 3
  formula = At
  name = G4_At
  specific = 4
FEATURE [App::DocumentObjectGroupPython] Rn_element005  label="Rn_element : 004"  # scripted group (container) (typed FeaturePython)
  n = 1
  ref = Rn_element
FEATURE [App::DocumentObjectGroupPython] G4_Rn  # scripted group (container) (typed FeaturePython)
  Dunit = g/cm3
  Dvalue = 0.00900662
  Group = -> [Rn_element005]
  conduct = 2
  density = 1
  expand = 3
  formula = Rn
  name = G4_Rn
  specific = 4
FEATURE [App::DocumentObjectGroupPython] Fr_element005  label="Fr_element : 004"  # scripted group (container) (typed FeaturePython)
  n = 1
  ref = Fr_element
FEATURE [App::DocumentObjectGroupPython] G4_Fr  # scripted group (container) (typed FeaturePython)
  Dunit = g/cm3
  Dvalue = 1
  Group = -> [Fr_element005]
  conduct = 2
  density = 1
  expand = 3
  formula = Fr
  name = G4_Fr
  specific = 4
FEATURE [App::DocumentObjectGroupPython] Ra_element005  label="Ra_element : 004"  # scripted group (container) (typed FeaturePython)
  n = 1
  ref = Ra_element
FEATURE [App::DocumentObjectGroupPython] G4_Ra  # scripted group (container) (typed FeaturePython)
  Dunit = g/cm3
  Dvalue = 5
  Group = -> [Ra_element005]
  conduct = 2
  density = 1
  expand = 3
  formula = Ra
  name = G4_Ra
  specific = 4
FEATURE [App::DocumentObjectGroupPython] Ac_element005  label="Ac_element : 004"  # scripted group (container) (typed FeaturePython)
  n = 1
  ref = Ac_element
FEATURE [App::DocumentObjectGroupPython] G4_Ac  # scripted group (container) (typed FeaturePython)
  Dunit = g/cm3
  Dvalue = 10.07
  Group = -> [Ac_element005]
  conduct = 2
  density = 1
  expand = 3
  formula = Ac
  name = G4_Ac
  specific = 4
FEATURE [App::DocumentObjectGroupPython] Th_element005  label="Th_element : 004"  # scripted group (container) (typed FeaturePython)
  n = 1
  ref = Th_element
FEATURE [App::DocumentObjectGroupPython] G4_Th  # scripted group (container) (typed FeaturePython)
  Dunit = g/cm3
  Dvalue = 11.72
  Group = -> [Th_element005]
  conduct = 2
  density = 1
  expand = 3
  formula = Th
  name = G4_Th
  specific = 4
FEATURE [App::DocumentObjectGroupPython] Pa_element005  label="Pa_element : 004"  # scripted group (container) (typed FeaturePython)
  n = 1
  ref = Pa_element
FEATURE [App::DocumentObjectGroupPython] G4_Pa  # scripted group (container) (typed FeaturePython)
  Dunit = g/cm3
  Dvalue = 15.37
  Group = -> [Pa_element005]
  conduct = 2
  density = 1
  expand = 3
  formula = Pa
  name = G4_Pa
  specific = 4
FEATURE [App::DocumentObjectGroupPython] U_element020  label="U_element : 019"  # scripted group (container) (typed FeaturePython)
  n = 1
  ref = U_element
FEATURE [App::DocumentObjectGroupPython] G4_U  # scripted group (container) (typed FeaturePython)
  Dunit = g/cm3
  Dvalue = 18.95
  Group = -> [U_element020]
  conduct = 2
  density = 1
  expand = 3
  formula = U
  name = G4_U
  specific = 4
FEATURE [App::DocumentObjectGroupPython] Np_element005  label="Np_element : 004"  # scripted group (container) (typed FeaturePython)
  n = 1
  ref = Np_element
FEATURE [App::DocumentObjectGroupPython] G4_Np  # scripted group (container) (typed FeaturePython)
  Dunit = g/cm3
  Dvalue = 20.25
  Group = -> [Np_element005]
  conduct = 2
  density = 1
  expand = 3
  formula = Np
  name = G4_Np
  specific = 4
FEATURE [App::DocumentObjectGroupPython] Pu_element010  label="Pu_element : 009"  # scripted group (container) (typed FeaturePython)
  n = 1
  ref = Pu_element
FEATURE [App::DocumentObjectGroupPython] G4_Pu  # scripted group (container) (typed FeaturePython)
  Dunit = g/cm3
  Dvalue = 19.84
  Group = -> [Pu_element010]
  conduct = 2
  density = 1
  expand = 3
  formula = Pu
  name = G4_Pu
  specific = 4
FEATURE [App::DocumentObjectGroupPython] Am_element005  label="Am_element : 004"  # scripted group (container) (typed FeaturePython)
  n = 1
  ref = Am_element
FEATURE [App::DocumentObjectGroupPython] G4_Am  # scripted group (container) (typed FeaturePython)
  Dunit = g/cm3
  Dvalue = 13.67
  Group = -> [Am_element005]
  conduct = 2
  density = 1
  expand = 3
  formula = Am
  name = G4_Am
  specific = 4
FEATURE [App::DocumentObjectGroupPython] Cm_element005  label="Cm_element : 004"  # scripted group (container) (typed FeaturePython)
  n = 1
  ref = Cm_element
FEATURE [App::DocumentObjectGroupPython] G4_Cm  # scripted group (container) (typed FeaturePython)
  Dunit = g/cm3
  Dvalue = 13.51
  Group = -> [Cm_element005]
  conduct = 2
  density = 1
  expand = 3
  formula = Cm
  name = G4_Cm
  specific = 4
FEATURE [App::DocumentObjectGroupPython] Bk_element005  label="Bk_element : 004"  # scripted group (container) (typed FeaturePython)
  n = 1
  ref = Bk_element
FEATURE [App::DocumentObjectGroupPython] G4_Bk  # scripted group (container) (typed FeaturePython)
  Dunit = g/cm3
  Dvalue = 14
  Group = -> [Bk_element005]
  conduct = 2
  density = 1
  expand = 3
  formula = Bk
  name = G4_Bk
  specific = 4
FEATURE [App::DocumentObjectGroupPython] Cf_element005  label="Cf_element : 004"  # scripted group (container) (typed FeaturePython)
  n = 1
  ref = Cf_element
FEATURE [App::DocumentObjectGroupPython] G4_Cf  # scripted group (container) (typed FeaturePython)
  Dunit = g/cm3
  Dvalue = 10
  Group = -> [Cf_element005]
  conduct = 2
  density = 1
  expand = 3
  formula = Cf
  name = G4_Cf
  specific = 4
FEATURE [App::DocumentObjectGroupPython] Element  # scripted group (container) (typed FeaturePython)
  Group = -> [G4_H,G4_He,G4_Li,G4_Be,G4_B,G4_C,G4_N,G4_O,G4_F,G4_Ne,G4_Na,G4_Mg,G4_Al,G4_Si,G4_P,G4_S,G4_Cl,G4_Ar,G4_K,G4_Ca,G4_Sc,G4_Ti,G4_V,G4_Cr,G4_Mn,G4_Fe,G4_Co,G4_Ni,G4_Cu,G4_Zn,G4_Ga,G4_Ge,G4_As,G4_Se,G4_Br,G4_Kr,G4_Rb,G4_Sr,G4_Y,G4_Zr,G4_Nb,G4_Mo,G4_Tc,G4_Ru,G4_Rh,G4_Pd,G4_Ag,G4_Cd,G4_In,G4_Sn,G4_Sb,G4_Te,G4_I,G4_Xe,G4_Cs,G4_Ba,G4_La,G4_Ce,G4_Pr,G4_Nd,G4_Pm,G4_Sm,G4_Eu,G4_Gd,G4_Tb,G4_Dy,G4_Ho,G4_Er,+30 more]
FEATURE [App::DocumentObjectGroupPython] H_element666  label="H_element : 431"  # scripted group (container) (typed FeaturePython)
  n = 2
  ref = H_element
FEATURE [App::DocumentObjectGroupPython] G4_lH2  # scripted group (container) (typed FeaturePython)
  Dunit = g/cm3
  Dvalue = 0.0708
  Group = -> [H_element666]
  conduct = 2
  density = 1
  expand = 3
  formula = G4_lH2
  name = G4_lH2
  specific = 4
FEATURE [App::DocumentObjectGroupPython] N_element321  label="N_element : 173"  # scripted group (container) (typed FeaturePython)
  n = 2
  ref = N_element
FEATURE [App::DocumentObjectGroupPython] G4_lN2  # scripted group (container) (typed FeaturePython)
  Dunit = g/cm3
  Dvalue = 0.807
  Group = -> [N_element321]
  conduct = 2
  density = 1
  expand = 3
  formula = G4_lN2
  name = G4_lN2
  specific = 4
FEATURE [App::DocumentObjectGroupPython] O_element626  label="O_element : 399"  # scripted group (container) (typed FeaturePython)
  n = 2
  ref = O_element
FEATURE [App::DocumentObjectGroupPython] G4_lO2  # scripted group (container) (typed FeaturePython)
  Dunit = g/cm3
  Dvalue = 1.141
  Group = -> [O_element626]
  conduct = 2
  density = 1
  expand = 3
  formula = G4_lO2
  name = G4_lO2
  specific = 4
FEATURE [App::DocumentObjectGroupPython] Ar003  label="Ar : 004"  # scripted group (container) (typed FeaturePython)
  n = 1
  ref = Ar
FEATURE [App::DocumentObjectGroupPython] G4_lAr  # scripted group (container) (typed FeaturePython)
  Dunit = g/cm3
  Dvalue = 1.396
  Group = -> [Ar003]
  conduct = 2
  density = 1
  expand = 3
  formula = G4_lAr
  name = G4_lAr
  specific = 4
FEATURE [App::DocumentObjectGroupPython] Br003  label="Br : 004"  # scripted group (container) (typed FeaturePython)
  n = 1
  ref = Br
FEATURE [App::DocumentObjectGroupPython] G4_lBr  # scripted group (container) (typed FeaturePython)
  Dunit = g/cm3
  Dvalue = 3.1028
  Group = -> [Br003]
  conduct = 2
  density = 1
  expand = 3
  formula = G4_lBr
  name = G4_lBr
  specific = 4
FEATURE [App::DocumentObjectGroupPython] Kr003  label="Kr : 004"  # scripted group (container) (typed FeaturePython)
  n = 1
  ref = Kr
FEATURE [App::DocumentObjectGroupPython] G4_lKr  # scripted group (container) (typed FeaturePython)
  Dunit = g/cm3
  Dvalue = 2.418
  Group = -> [Kr003]
  conduct = 2
  density = 1
  expand = 3
  formula = G4_lKr
  name = G4_lKr
  specific = 4
FEATURE [App::DocumentObjectGroupPython] Xe003  label="Xe : 004"  # scripted group (container) (typed FeaturePython)
  n = 1
  ref = Xe
FEATURE [App::DocumentObjectGroupPython] G4_lXe  # scripted group (container) (typed FeaturePython)
  Dunit = g/cm3
  Dvalue = 2.953
  Group = -> [Xe003]
  conduct = 2
  density = 1
  expand = 3
  formula = G4_lXe
  name = G4_lXe
  specific = 4
FEATURE [App::DocumentObjectGroupPython] O_element627  label="O_element : 400"  # scripted group (container) (typed FeaturePython)
  n = 4
  ref = O_element
FEATURE [App::DocumentObjectGroupPython] Pb_element028  label="Pb_element : 013"  # scripted group (container) (typed FeaturePython)
  n = 1
  ref = Pb_element
FEATURE [App::DocumentObjectGroupPython] W_element025  label="W_element : 024"  # scripted group (container) (typed FeaturePython)
  n = 1
  ref = W_element
FEATURE [App::DocumentObjectGroupPython] G4_PbWO4  # scripted group (container) (typed FeaturePython)
  Dunit = g/cm3
  Dvalue = 8.28
  Group = -> [O_element627,Pb_element028,W_element025]
  conduct = 2
  density = 1
  expand = 3
  formula = G4_PbWO4
  name = G4_PbWO4
  specific = 4
FEATURE [App::DocumentObjectGroupPython] alactic003  label="alactic : 004"  # scripted group (container) (typed FeaturePython)
  n = 1
  ref = alactic
FEATURE [App::DocumentObjectGroupPython] G4_Galactic  # scripted group (container) (typed FeaturePython)
  Dunit = g/cm3
  Dvalue = 0
  Group = -> [alactic003]
  conduct = 2
  density = 1
  expand = 3
  formula = G4_Galactic
  name = G4_Galactic
  specific = 4
FEATURE [App::DocumentObjectGroupPython] RAPHITE_POROUS003  label="RAPHITE_POROUS : 004"  # scripted group (container) (typed FeaturePython)
  n = 1
  ref = RAPHITE_POROUS
FEATURE [App::DocumentObjectGroupPython] G4_GRAPHITE_POROUS  # scripted group (container) (typed FeaturePython)
  Dunit = g/cm3
  Dvalue = 1.7
  Group = -> [RAPHITE_POROUS003]
  conduct = 2
  density = 1
  expand = 3
  formula = G4_GRAPHITE_POROUS
  name = G4_GRAPHITE_POROUS
  specific = 4
FEATURE [App::DocumentObjectGroupPython] H_element667  label="H_element : 0.286"  # scripted group (container) (typed FeaturePython)
  n = 0.080538
FEATURE [App::DocumentObjectGroupPython] C_element717  label="C_element : 0.1017"  # scripted group (container) (typed FeaturePython)
  n = 0.599848
FEATURE [App::DocumentObjectGroupPython] O_element628  label="O_element : 0.1007"  # scripted group (container) (typed FeaturePython)
  n = 0.319614
FEATURE [App::DocumentObjectGroupPython] G4_LUCITE  # scripted group (container) (typed FeaturePython)
  Dunit = g/cm3
  Dvalue = 1.19
  Group = -> [H_element667,C_element717,O_element628]
  conduct = 2
  density = 1
  expand = 3
  formula = G4_LUCITE
  name = G4_LUCITE
  specific = 4
FEATURE [App::DocumentObjectGroupPython] Cu_element014  label="Cu_element : 097"  # scripted group (container) (typed FeaturePython)
  n = 62
  ref = Cu_element
FEATURE [App::DocumentObjectGroupPython] Zn_element014  label="Zn_element : 043"  # scripted group (container) (typed FeaturePython)
  n = 35
  ref = Zn_element
FEATURE [App::DocumentObjectGroupPython] Pb_element029  label="Pb_element : 014"  # scripted group (container) (typed FeaturePython)
  n = 3
  ref = Pb_element
FEATURE [App::DocumentObjectGroupPython] G4_BRASS  # scripted group (container) (typed FeaturePython)
  Dunit = g/cm3
  Dvalue = 8.52
  Group = -> [Cu_element014,Zn_element014,Pb_element029]
  conduct = 2
  density = 1
  expand = 3
  formula = G4_BRASS
  name = G4_BRASS
  specific = 4
FEATURE [App::DocumentObjectGroupPython] Cu_element015  label="Cu_element : 098"  # scripted group (container) (typed FeaturePython)
  n = 89
  ref = Cu_element
FEATURE [App::DocumentObjectGroupPython] Zn_element015  label="Zn_element : 044"  # scripted group (container) (typed FeaturePython)
  n = 9
  ref = Zn_element
FEATURE [App::DocumentObjectGroupPython] Pb_element030  label="Pb_element : 015"  # scripted group (container) (typed FeaturePython)
  n = 2
  ref = Pb_element
FEATURE [App::DocumentObjectGroupPython] G4_BRONZE  # scripted group (container) (typed FeaturePython)
  Dunit = g/cm3
  Dvalue = 8.82
  Group = -> [Cu_element015,Zn_element015,Pb_element030]
  conduct = 2
  density = 1
  expand = 3
  formula = G4_BRONZE
  name = G4_BRONZE
  specific = 4
FEATURE [App::DocumentObjectGroupPython] Fe_element040  label="Fe_element : 021"  # scripted group (container) (typed FeaturePython)
  n = 74
  ref = Fe_element
FEATURE [App::DocumentObjectGroupPython] Cr_element010  label="Cr_element : 024"  # scripted group (container) (typed FeaturePython)
  n = 18
  ref = Cr_element
FEATURE [App::DocumentObjectGroupPython] Ni_element010  label="Ni_element : 014"  # scripted group (container) (typed FeaturePython)
  n = 8
  ref = Ni_element
FEATURE [App::DocumentObjectGroupPython] G4_STAINLESS_STEEL  label="G4_STAINLESS-STEEL"  # scripted group (container) (typed FeaturePython)
  Dunit = g/cm3
  Dvalue = 8
  Group = -> [Fe_element040,Cr_element010,Ni_element010]
  conduct = 2
  density = 1
  expand = 3
  formula = G4_STAINLESS-STEEL
  name = G4_STAINLESS-STEEL
  specific = 4
FEATURE [App::DocumentObjectGroupPython] H_element668  label="H_element : 432"  # scripted group (container) (typed FeaturePython)
  n = 18
  ref = H_element
FEATURE [App::DocumentObjectGroupPython] C_element718  label="C_element : 471"  # scripted group (container) (typed FeaturePython)
  n = 12
  ref = C_element
FEATURE [App::DocumentObjectGroupPython] O_element629  label="O_element : 401"  # scripted group (container) (typed FeaturePython)
  n = 7
  ref = O_element
FEATURE [App::DocumentObjectGroupPython] G4_CR39  # scripted group (container) (typed FeaturePython)
  Dunit = g/cm3
  Dvalue = 1.32
  Group = -> [H_element668,C_element718,O_element629]
  conduct = 2
  density = 1
  expand = 3
  formula = G4_CR39
  name = G4_CR39
  specific = 4
FEATURE [App::DocumentObjectGroupPython] H_element669  label="H_element : 433"  # scripted group (container) (typed FeaturePython)
  n = 38
  ref = H_element
FEATURE [App::DocumentObjectGroupPython] C_element719  label="C_element : 472"  # scripted group (container) (typed FeaturePython)
  n = 18
  ref = C_element
FEATURE [App::DocumentObjectGroupPython] O_element630  label="O_element : 402"  # scripted group (container) (typed FeaturePython)
  n = 1
  ref = O_element
FEATURE [App::DocumentObjectGroupPython] G4_OCTADECANOL  # scripted group (container) (typed FeaturePython)
  Dunit = g/cm3
  Dvalue = 0.812
  Group = -> [H_element669,C_element719,O_element630]
  conduct = 2
  density = 1
  expand = 3
  formula = G4_OCTADECANOL
  name = G4_OCTADECANOL
  specific = 4
FEATURE [App::DocumentObjectGroupPython] HEP  # scripted group (container) (typed FeaturePython)
  Group = -> [G4_lH2,G4_lN2,G4_lO2,G4_lAr,G4_lBr,G4_lKr,G4_lXe,G4_PbWO4,G4_Galactic,G4_GRAPHITE_POROUS,G4_LUCITE,G4_BRASS,G4_BRONZE,G4_STAINLESS_STEEL,G4_CR39,G4_OCTADECANOL]
FEATURE [App::DocumentObjectGroupPython] C_element720  label="C_element : 473"  # scripted group (container) (typed FeaturePython)
  n = 14
  ref = C_element
FEATURE [App::DocumentObjectGroupPython] H_element670  label="H_element : 434"  # scripted group (container) (typed FeaturePython)
  n = 10
  ref = H_element
FEATURE [App::DocumentObjectGroupPython] O_element631  label="O_element : 403"  # scripted group (container) (typed FeaturePython)
  n = 2
  ref = O_element
FEATURE [App::DocumentObjectGroupPython] N_element322  label="N_element : 174"  # scripted group (container) (typed FeaturePython)
  n = 2
  ref = N_element
FEATURE [App::DocumentObjectGroupPython] G4_KEVLAR  # scripted group (container) (typed FeaturePython)
  Dunit = g/cm3
  Dvalue = 1.44
  Group = -> [C_element720,H_element670,O_element631,N_element322]
  conduct = 2
  density = 1
  expand = 3
  formula = G4_KEVLAR
  name = G4_KEVLAR
  specific = 4
FEATURE [App::DocumentObjectGroupPython] C_element721  label="C_element : 474"  # scripted group (container) (typed FeaturePython)
  n = 10
  ref = C_element
FEATURE [App::DocumentObjectGroupPython] H_element671  label="H_element : 435"  # scripted group (container) (typed FeaturePython)
  n = 8
  ref = H_element
FEATURE [App::DocumentObjectGroupPython] O_element632  label="O_element : 404"  # scripted group (container) (typed FeaturePython)
  n = 4
  ref = O_element
FEATURE [App::DocumentObjectGroupPython] G4_DACRON  # scripted group (container) (typed FeaturePython)
  Dunit = g/cm3
  Dvalue = 1.4
  Group = -> [C_element721,H_element671,O_element632]
  conduct = 2
  density = 1
  expand = 3
  formula = G4_DACRON
  name = G4_DACRON
  specific = 4
FEATURE [App::DocumentObjectGroupPython] C_element722  label="C_element : 475"  # scripted group (container) (typed FeaturePython)
  n = 4
  ref = C_element
FEATURE [App::DocumentObjectGroupPython] H_element672  label="H_element : 436"  # scripted group (container) (typed FeaturePython)
  n = 5
  ref = H_element
FEATURE [App::DocumentObjectGroupPython] Cl_element150  label="Cl_element : 076"  # scripted group (container) (typed FeaturePython)
  n = 1
  ref = Cl_element
FEATURE [App::DocumentObjectGroupPython] G4_NEOPRENE  # scripted group (container) (typed FeaturePython)
  Dunit = g/cm3
  Dvalue = 1.23
  Group = -> [C_element722,H_element672,Cl_element150]
  conduct = 2
  density = 1
  expand = 3
  formula = G4_NEOPRENE
  name = G4_NEOPRENE
  specific = 4
FEATURE [App::DocumentObjectGroupPython] Space  # scripted group (container) (typed FeaturePython)
  Group = -> [G4_KEVLAR,G4_DACRON,G4_NEOPRENE]
FEATURE [App::DocumentObjectGroupPython] H_element673  label="H_element : 437"  # scripted group (container) (typed FeaturePython)
  n = 5
  ref = H_element
FEATURE [App::DocumentObjectGroupPython] C_element723  label="C_element : 476"  # scripted group (container) (typed FeaturePython)
  n = 4
  ref = C_element
FEATURE [App::DocumentObjectGroupPython] N_element323  label="N_element : 175"  # scripted group (container) (typed FeaturePython)
  n = 3
  ref = N_element
FEATURE [App::DocumentObjectGroupPython] O_element633  label="O_element : 405"  # scripted group (container) (typed FeaturePython)
  n = 1
  ref = O_element
FEATURE [App::DocumentObjectGroupPython] G4_CYTOSINE  # scripted group (container) (typed FeaturePython)
  Dunit = g/cm3
  Dvalue = 1.55
  Group = -> [H_element673,C_element723,N_element323,O_element633]
  conduct = 2
  density = 1
  expand = 3
  formula = G4_CYTOSINE
  name = G4_CYTOSINE
  specific = 4
FEATURE [App::DocumentObjectGroupPython] H_element674  label="H_element : 438"  # scripted group (container) (typed FeaturePython)
  n = 6
  ref = H_element
FEATURE [App::DocumentObjectGroupPython] C_element724  label="C_element : 477"  # scripted group (container) (typed FeaturePython)
  n = 5
  ref = C_element
FEATURE [App::DocumentObjectGroupPython] N_element324  label="N_element : 176"  # scripted group (container) (typed FeaturePython)
  n = 2
  ref = N_element
FEATURE [App::DocumentObjectGroupPython] O_element634  label="O_element : 406"  # scripted group (container) (typed FeaturePython)
  n = 2
  ref = O_element
FEATURE [App::DocumentObjectGroupPython] G4_THYMINE  # scripted group (container) (typed FeaturePython)
  Dunit = g/cm3
  Dvalue = 1.23
  Group = -> [H_element674,C_element724,N_element324,O_element634]
  conduct = 2
  density = 1
  expand = 3
  formula = G4_THYMINE
  name = G4_THYMINE
  specific = 4
FEATURE [App::DocumentObjectGroupPython] H_element675  label="H_element : 439"  # scripted group (container) (typed FeaturePython)
  n = 4
  ref = H_element
FEATURE [App::DocumentObjectGroupPython] C_element725  label="C_element : 478"  # scripted group (container) (typed FeaturePython)
  n = 4
  ref = C_element
FEATURE [App::DocumentObjectGroupPython] N_element325  label="N_element : 177"  # scripted group (container) (typed FeaturePython)
  n = 2
  ref = N_element
FEATURE [App::DocumentObjectGroupPython] O_element635  label="O_element : 407"  # scripted group (container) (typed FeaturePython)
  n = 2
  ref = O_element
FEATURE [App::DocumentObjectGroupPython] G4_URACIL  # scripted group (container) (typed FeaturePython)
  Dunit = g/cm3
  Dvalue = 1.32
  Group = -> [H_element675,C_element725,N_element325,O_element635]
  conduct = 2
  density = 1
  expand = 3
  formula = G4_URACIL
  name = G4_URACIL
  specific = 4
FEATURE [App::DocumentObjectGroupPython] H_element676  label="H_element : 440"  # scripted group (container) (typed FeaturePython)
  n = 4
  ref = H_element
FEATURE [App::DocumentObjectGroupPython] C_element726  label="C_element : 479"  # scripted group (container) (typed FeaturePython)
  n = 5
  ref = C_element
FEATURE [App::DocumentObjectGroupPython] N_element326  label="N_element : 178"  # scripted group (container) (typed FeaturePython)
  n = 5
  ref = N_element
FEATURE [App::DocumentObjectGroupPython] G4_DNA_ADENINE  # scripted group (container) (typed FeaturePython)
  Dunit = g/cm3
  Dvalue = 1
  Group = -> [H_element676,C_element726,N_element326]
  conduct = 2
  density = 1
  expand = 3
  formula = G4_DNA_ADENINE
  name = G4_DNA_ADENINE
  specific = 4
FEATURE [App::DocumentObjectGroupPython] H_element677  label="H_element : 441"  # scripted group (container) (typed FeaturePython)
  n = 4
  ref = H_element
FEATURE [App::DocumentObjectGroupPython] C_element727  label="C_element : 480"  # scripted group (container) (typed FeaturePython)
  n = 5
  ref = C_element
FEATURE [App::DocumentObjectGroupPython] N_element327  label="N_element : 179"  # scripted group (container) (typed FeaturePython)
  n = 5
  ref = N_element
FEATURE [App::DocumentObjectGroupPython] O_element636  label="O_element : 408"  # scripted group (container) (typed FeaturePython)
  n = 1
  ref = O_element
FEATURE [App::DocumentObjectGroupPython] G4_DNA_GUANINE  # scripted group (container) (typed FeaturePython)
  Dunit = g/cm3
  Dvalue = 1
  Group = -> [H_element677,C_element727,N_element327,O_element636]
  conduct = 2
  density = 1
  expand = 3
  formula = G4_DNA_GUANINE
  name = G4_DNA_GUANINE
  specific = 4
FEATURE [App::DocumentObjectGroupPython] H_element678  label="H_element : 442"  # scripted group (container) (typed FeaturePython)
  n = 4
  ref = H_element
FEATURE [App::DocumentObjectGroupPython] C_element728  label="C_element : 481"  # scripted group (container) (typed FeaturePython)
  n = 4
  ref = C_element
FEATURE [App::DocumentObjectGroupPython] N_element328  label="N_element : 180"  # scripted group (container) (typed FeaturePython)
  n = 3
  ref = N_element
FEATURE [App::DocumentObjectGroupPython] O_element637  label="O_element : 409"  # scripted group (container) (typed FeaturePython)
  n = 1
  ref = O_element
FEATURE [App::DocumentObjectGroupPython] G4_DNA_CYTOSINE  # scripted group (container) (typed FeaturePython)
  Dunit = g/cm3
  Dvalue = 1
  Group = -> [H_element678,C_element728,N_element328,O_element637]
  conduct = 2
  density = 1
  expand = 3
  formula = G4_DNA_CYTOSINE
  name = G4_DNA_CYTOSINE
  specific = 4
FEATURE [App::DocumentObjectGroupPython] H_element679  label="H_element : 443"  # scripted group (container) (typed FeaturePython)
  n = 5
  ref = H_element
FEATURE [App::DocumentObjectGroupPython] C_element729  label="C_element : 482"  # scripted group (container) (typed FeaturePython)
  n = 5
  ref = C_element
FEATURE [App::DocumentObjectGroupPython] N_element329  label="N_element : 181"  # scripted group (container) (typed FeaturePython)
  n = 2
  ref = N_element
FEATURE [App::DocumentObjectGroupPython] O_element638  label="O_element : 410"  # scripted group (container) (typed FeaturePython)
  n = 2
  ref = O_element
FEATURE [App::DocumentObjectGroupPython] G4_DNA_THYMINE  # scripted group (container) (typed FeaturePython)
  Dunit = g/cm3
  Dvalue = 1
  Group = -> [H_element679,C_element729,N_element329,O_element638]
  conduct = 2
  density = 1
  expand = 3
  formula = G4_DNA_THYMINE
  name = G4_DNA_THYMINE
  specific = 4
FEATURE [App::DocumentObjectGroupPython] H_element680  label="H_element : 444"  # scripted group (container) (typed FeaturePython)
  n = 3
  ref = H_element
FEATURE [App::DocumentObjectGroupPython] C_element730  label="C_element : 483"  # scripted group (container) (typed FeaturePython)
  n = 4
  ref = C_element
FEATURE [App::DocumentObjectGroupPython] N_element330  label="N_element : 182"  # scripted group (container) (typed FeaturePython)
  n = 2
  ref = N_element
FEATURE [App::DocumentObjectGroupPython] O_element639  label="O_element : 411"  # scripted group (container) (typed FeaturePython)
  n = 2
  ref = O_element
FEATURE [App::DocumentObjectGroupPython] G4_DNA_URACIL  # scripted group (container) (typed FeaturePython)
  Dunit = g/cm3
  Dvalue = 1
  Group = -> [H_element680,C_element730,N_element330,O_element639]
  conduct = 2
  density = 1
  expand = 3
  formula = G4_DNA_URACIL
  name = G4_DNA_URACIL
  specific = 4
FEATURE [App::DocumentObjectGroupPython] H_element681  label="H_element : 445"  # scripted group (container) (typed FeaturePython)
  n = 10
  ref = H_element
FEATURE [App::DocumentObjectGroupPython] C_element731  label="C_element : 484"  # scripted group (container) (typed FeaturePython)
  n = 10
  ref = C_element
FEATURE [App::DocumentObjectGroupPython] N_element331  label="N_element : 183"  # scripted group (container) (typed FeaturePython)
  n = 5
  ref = N_element
FEATURE [App::DocumentObjectGroupPython] O_element640  label="O_element : 412"  # scripted group (container) (typed FeaturePython)
  n = 4
  ref = O_element
FEATURE [App::DocumentObjectGroupPython] G4_DNA_ADENOSINE  # scripted group (container) (typed FeaturePython)
  Dunit = g/cm3
  Dvalue = 1
  Group = -> [H_element681,C_element731,N_element331,O_element640]
  conduct = 2
  density = 1
  expand = 3
  formula = G4_DNA_ADENOSINE
  name = G4_DNA_ADENOSINE
  specific = 4
FEATURE [App::DocumentObjectGroupPython] H_element682  label="H_element : 446"  # scripted group (container) (typed FeaturePython)
  n = 10
  ref = H_element
FEATURE [App::DocumentObjectGroupPython] C_element732  label="C_element : 485"  # scripted group (container) (typed FeaturePython)
  n = 10
  ref = C_element
FEATURE [App::DocumentObjectGroupPython] N_element332  label="N_element : 184"  # scripted group (container) (typed FeaturePython)
  n = 5
  ref = N_element
FEATURE [App::DocumentObjectGroupPython] O_element641  label="O_element : 413"  # scripted group (container) (typed FeaturePython)
  n = 5
  ref = O_element
FEATURE [App::DocumentObjectGroupPython] G4_DNA_GUANOSINE  # scripted group (container) (typed FeaturePython)
  Dunit = g/cm3
  Dvalue = 1
  Group = -> [H_element682,C_element732,N_element332,O_element641]
  conduct = 2
  density = 1
  expand = 3
  formula = G4_DNA_GUANOSINE
  name = G4_DNA_GUANOSINE
  specific = 4
FEATURE [App::DocumentObjectGroupPython] H_element683  label="H_element : 447"  # scripted group (container) (typed FeaturePython)
  n = 10
  ref = H_element
FEATURE [App::DocumentObjectGroupPython] C_element733  label="C_element : 486"  # scripted group (container) (typed FeaturePython)
  n = 9
  ref = C_element
FEATURE [App::DocumentObjectGroupPython] N_element333  label="N_element : 185"  # scripted group (container) (typed FeaturePython)
  n = 3
  ref = N_element
FEATURE [App::DocumentObjectGroupPython] O_element642  label="O_element : 414"  # scripted group (container) (typed FeaturePython)
  n = 5
  ref = O_element
FEATURE [App::DocumentObjectGroupPython] G4_DNA_CYTIDINE  # scripted group (container) (typed FeaturePython)
  Dunit = g/cm3
  Dvalue = 1
  Group = -> [H_element683,C_element733,N_element333,O_element642]
  conduct = 2
  density = 1
  expand = 3
  formula = G4_DNA_CYTIDINE
  name = G4_DNA_CYTIDINE
  specific = 4
FEATURE [App::DocumentObjectGroupPython] H_element684  label="H_element : 448"  # scripted group (container) (typed FeaturePython)
  n = 9
  ref = H_element
FEATURE [App::DocumentObjectGroupPython] C_element734  label="C_element : 487"  # scripted group (container) (typed FeaturePython)
  n = 9
  ref = C_element
FEATURE [App::DocumentObjectGroupPython] N_element334  label="N_element : 186"  # scripted group (container) (typed FeaturePython)
  n = 2
  ref = N_element
FEATURE [App::DocumentObjectGroupPython] O_element643  label="O_element : 415"  # scripted group (container) (typed FeaturePython)
  n = 6
  ref = O_element
FEATURE [App::DocumentObjectGroupPython] G4_DNA_URIDINE  # scripted group (container) (typed FeaturePython)
  Dunit = g/cm3
  Dvalue = 1
  Group = -> [H_element684,C_element734,N_element334,O_element643]
  conduct = 2
  density = 1
  expand = 3
  formula = G4_DNA_URIDINE
  name = G4_DNA_URIDINE
  specific = 4
FEATURE [App::DocumentObjectGroupPython] H_element685  label="H_element : 449"  # scripted group (container) (typed FeaturePython)
  n = 11
  ref = H_element
FEATURE [App::DocumentObjectGroupPython] C_element735  label="C_element : 488"  # scripted group (container) (typed FeaturePython)
  n = 10
  ref = C_element
FEATURE [App::DocumentObjectGroupPython] N_element335  label="N_element : 187"  # scripted group (container) (typed FeaturePython)
  n = 2
  ref = N_element
FEATURE [App::DocumentObjectGroupPython] O_element644  label="O_element : 416"  # scripted group (container) (typed FeaturePython)
  n = 6
  ref = O_element
FEATURE [App::DocumentObjectGroupPython] G4_DNA_METHYLURIDINE  # scripted group (container) (typed FeaturePython)
  Dunit = g/cm3
  Dvalue = 1
  Group = -> [H_element685,C_element735,N_element335,O_element644]
  conduct = 2
  density = 1
  expand = 3
  formula = G4_DNA_METHYLURIDINE
  name = G4_DNA_METHYLURIDINE
  specific = 4
FEATURE [App::DocumentObjectGroupPython] P_element090  label="P_element : 034"  # scripted group (container) (typed FeaturePython)
  n = 1
  ref = P_element
FEATURE [App::DocumentObjectGroupPython] O_element645  label="O_element : 417"  # scripted group (container) (typed FeaturePython)
  n = 3
  ref = O_element
FEATURE [App::DocumentObjectGroupPython] G4_DNA_MONOPHOSPHATE  # scripted group (container) (typed FeaturePython)
  Dunit = g/cm3
  Dvalue = 1
  Group = -> [P_element090,O_element645]
  conduct = 2
  density = 1
  expand = 3
  formula = G4_DNA_MONOPHOSPHATE
  name = G4_DNA_MONOPHOSPHATE
  specific = 4
FEATURE [App::DocumentObjectGroupPython] H_element686  label="H_element : 450"  # scripted group (container) (typed FeaturePython)
  n = 10
  ref = H_element
FEATURE [App::DocumentObjectGroupPython] C_element736  label="C_element : 489"  # scripted group (container) (typed FeaturePython)
  n = 10
  ref = C_element
FEATURE [App::DocumentObjectGroupPython] N_element336  label="N_element : 188"  # scripted group (container) (typed FeaturePython)
  n = 5
  ref = N_element
FEATURE [App::DocumentObjectGroupPython] O_element646  label="O_element : 418"  # scripted group (container) (typed FeaturePython)
  n = 7
  ref = O_element
FEATURE [App::DocumentObjectGroupPython] P_element091  label="P_element : 035"  # scripted group (container) (typed FeaturePython)
  n = 1
  ref = P_element
FEATURE [App::DocumentObjectGroupPython] G4_DNA_A  # scripted group (container) (typed FeaturePython)
  Dunit = g/cm3
  Dvalue = 1
  Group = -> [H_element686,C_element736,N_element336,O_element646,P_element091]
  conduct = 2
  density = 1
  expand = 3
  formula = G4_DNA_A
  name = G4_DNA_A
  specific = 4
FEATURE [App::DocumentObjectGroupPython] H_element687  label="H_element : 451"  # scripted group (container) (typed FeaturePython)
  n = 10
  ref = H_element
FEATURE [App::DocumentObjectGroupPython] C_element737  label="C_element : 490"  # scripted group (container) (typed FeaturePython)
  n = 10
  ref = C_element
FEATURE [App::DocumentObjectGroupPython] N_element337  label="N_element : 189"  # scripted group (container) (typed FeaturePython)
  n = 5
  ref = N_element
FEATURE [App::DocumentObjectGroupPython] O_element647  label="O_element : 419"  # scripted group (container) (typed FeaturePython)
  n = 8
  ref = O_element
FEATURE [App::DocumentObjectGroupPython] P_element092  label="P_element : 036"  # scripted group (container) (typed FeaturePython)
  n = 1
  ref = P_element
FEATURE [App::DocumentObjectGroupPython] G4_DNA_G  # scripted group (container) (typed FeaturePython)
  Dunit = g/cm3
  Dvalue = 1
  Group = -> [H_element687,C_element737,N_element337,O_element647,P_element092]
  conduct = 2
  density = 1
  expand = 3
  formula = G4_DNA_G
  name = G4_DNA_G
  specific = 4
FEATURE [App::DocumentObjectGroupPython] H_element688  label="H_element : 452"  # scripted group (container) (typed FeaturePython)
  n = 10
  ref = H_element
FEATURE [App::DocumentObjectGroupPython] C_element738  label="C_element : 491"  # scripted group (container) (typed FeaturePython)
  n = 9
  ref = C_element
FEATURE [App::DocumentObjectGroupPython] N_element338  label="N_element : 190"  # scripted group (container) (typed FeaturePython)
  n = 3
  ref = N_element
FEATURE [App::DocumentObjectGroupPython] O_element648  label="O_element : 420"  # scripted group (container) (typed FeaturePython)
  n = 8
  ref = O_element
FEATURE [App::DocumentObjectGroupPython] P_element093  label="P_element : 037"  # scripted group (container) (typed FeaturePython)
  n = 1
  ref = P_element
FEATURE [App::DocumentObjectGroupPython] G4_DNA_C  # scripted group (container) (typed FeaturePython)
  Dunit = g/cm3
  Dvalue = 1
  Group = -> [H_element688,C_element738,N_element338,O_element648,P_element093]
  conduct = 2
  density = 1
  expand = 3
  formula = G4_DNA_C
  name = G4_DNA_C
  specific = 4
FEATURE [App::DocumentObjectGroupPython] H_element689  label="H_element : 453"  # scripted group (container) (typed FeaturePython)
  n = 9
  ref = H_element
FEATURE [App::DocumentObjectGroupPython] C_element739  label="C_element : 492"  # scripted group (container) (typed FeaturePython)
  n = 9
  ref = C_element
FEATURE [App::DocumentObjectGroupPython] N_element339  label="N_element : 191"  # scripted group (container) (typed FeaturePython)
  n = 2
  ref = N_element
FEATURE [App::DocumentObjectGroupPython] O_element649  label="O_element : 421"  # scripted group (container) (typed FeaturePython)
  n = 9
  ref = O_element
FEATURE [App::DocumentObjectGroupPython] P_element094  label="P_element : 038"  # scripted group (container) (typed FeaturePython)
  n = 1
  ref = P_element
FEATURE [App::DocumentObjectGroupPython] G4_DNA_U  # scripted group (container) (typed FeaturePython)
  Dunit = g/cm3
  Dvalue = 1
  Group = -> [H_element689,C_element739,N_element339,O_element649,P_element094]
  conduct = 2
  density = 1
  expand = 3
  formula = G4_DNA_U
  name = G4_DNA_U
  specific = 4
FEATURE [App::DocumentObjectGroupPython] H_element690  label="H_element : 454"  # scripted group (container) (typed FeaturePython)
  n = 11
  ref = H_element
FEATURE [App::DocumentObjectGroupPython] C_element740  label="C_element : 493"  # scripted group (container) (typed FeaturePython)
  n = 10
  ref = C_element
FEATURE [App::DocumentObjectGroupPython] N_element340  label="N_element : 192"  # scripted group (container) (typed FeaturePython)
  n = 2
  ref = N_element
FEATURE [App::DocumentObjectGroupPython] O_element650  label="O_element : 422"  # scripted group (container) (typed FeaturePython)
  n = 9
  ref = O_element
FEATURE [App::DocumentObjectGroupPython] P_element095  label="P_element : 039"  # scripted group (container) (typed FeaturePython)
  n = 1
  ref = P_element
FEATURE [App::DocumentObjectGroupPython] G4_DNA_MU  # scripted group (container) (typed FeaturePython)
  Dunit = g/cm3
  Dvalue = 1
  Group = -> [H_element690,C_element740,N_element340,O_element650,P_element095]
  conduct = 2
  density = 1
  expand = 3
  formula = G4_DNA_MU
  name = G4_DNA_MU
  specific = 4
FEATURE [App::DocumentObjectGroupPython] BioChemical  # scripted group (container) (typed FeaturePython)
  Group = -> [G4_CYTOSINE,G4_THYMINE,G4_URACIL,G4_DNA_ADENINE,G4_DNA_GUANINE,G4_DNA_CYTOSINE,G4_DNA_THYMINE,G4_DNA_URACIL,G4_DNA_ADENOSINE,G4_DNA_GUANOSINE,G4_DNA_CYTIDINE,G4_DNA_URIDINE,G4_DNA_METHYLURIDINE,G4_DNA_MONOPHOSPHATE,G4_DNA_A,G4_DNA_G,G4_DNA_C,G4_DNA_U,G4_DNA_MU]
FEATURE [App::DocumentObjectGroupPython] G4Materials  # scripted group (container) (typed FeaturePython)
  Group = -> [NIST,Element,HEP,Space,BioChemical]
FEATURE [App::DocumentObjectGroupPython] Geant4  # scripted group (container) (typed FeaturePython)
  Group = -> [G4Isotopes,G4Elements,G4Materials]
FEATURE [App::DocumentObjectGroupPython] Materials  # scripted group (container) (typed FeaturePython)
  Group = -> [Geant4]
